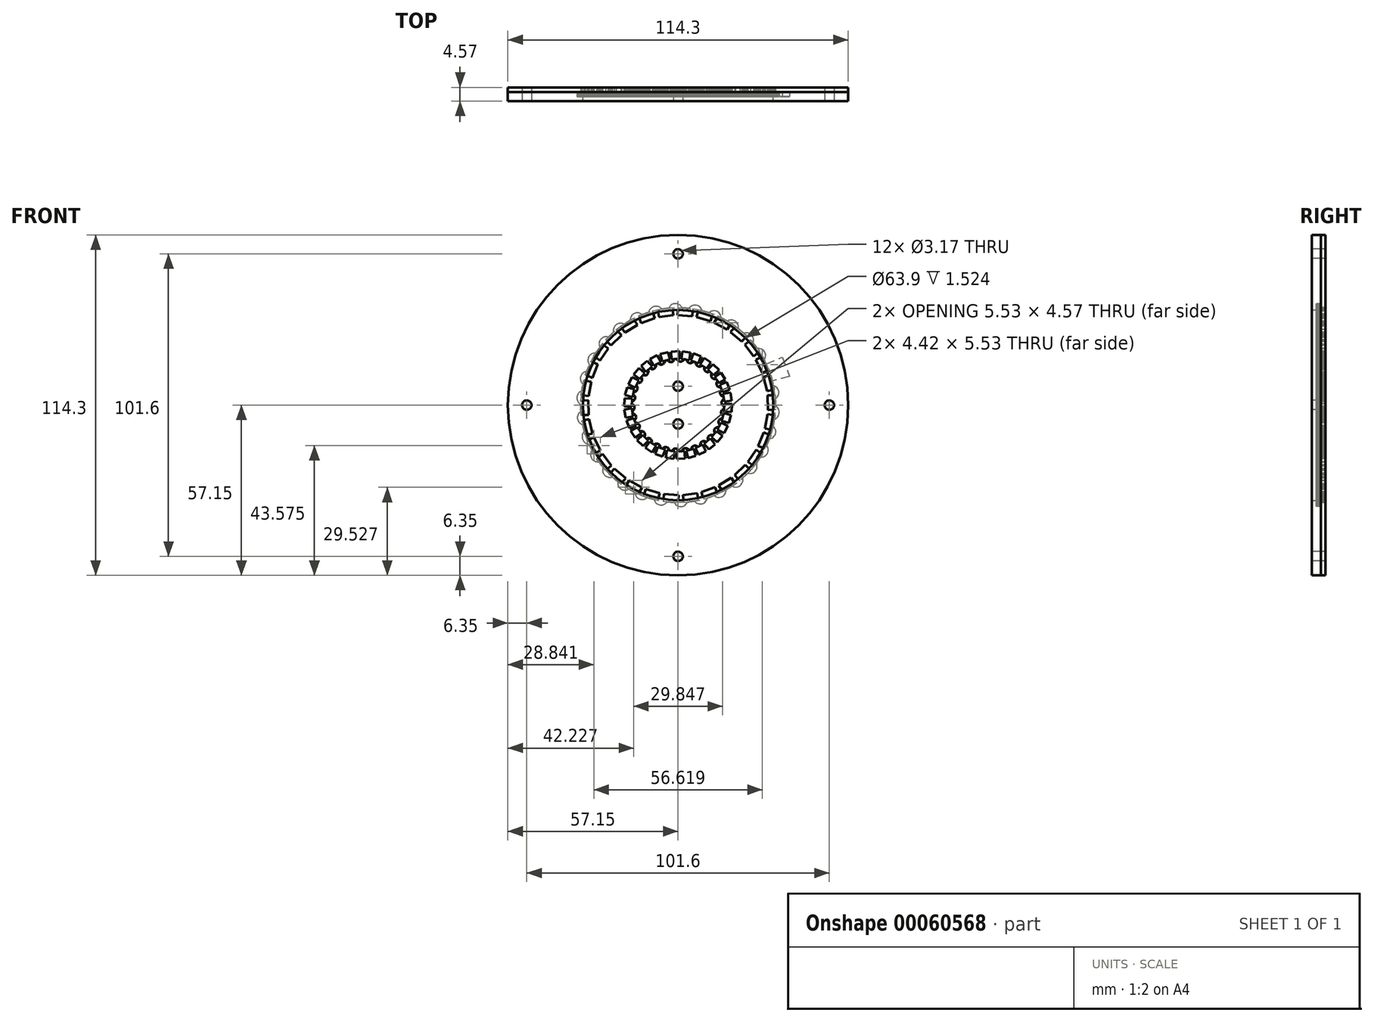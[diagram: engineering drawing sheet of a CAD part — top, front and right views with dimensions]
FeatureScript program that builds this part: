
annotation { "Feature Type Name" : "Feature", "Feature Type Description" : "" }
export const myFeature = defineFeature(function(context is Context, id is Id, definition is map)
    precondition{}
    {
        {
            var Q0;
            Q0=qCreatedBy(makeId("Front.planeOp"),FACE);
            var sketch = newSketch(context, id + "F0", { "sketchPlane" : qUnion([Q0])});
            skCircle(sketch, "E0", {"center": v(0, 0) * mm, "radius": 57.15 * mm});
            skCircle(sketch, "E1", {"center": v(50.8, 0) * mm, "radius": 1.59 * mm});
            skCircle(sketch, "E2", {"center": v(-50.8, 0) * mm, "radius": 1.59 * mm});
            skCircle(sketch, "E3", {"center": v(0, -50.8) * mm, "radius": 1.59 * mm});
            skCircle(sketch, "E4", {"center": v(0, 50.8) * mm, "radius": 1.59 * mm});
            skCircle(sketch, "E5", {"center": v(0, 6.35) * mm, "radius": 1.59 * mm});
            skCircle(sketch, "E6", {"center": v(0, -6.35) * mm, "radius": 1.59 * mm});
            skLineSegment(sketch, "E7", {"start": v(15.83, -1.28) * mm, "end": v(15.67, -1.27) * mm});
            skLineSegment(sketch, "E8", {"start": v(15.67, -1.27) * mm, "end": v(15.51, -1.27) * mm});
            skLineSegment(sketch, "E9", {"start": v(15.51, -1.27) * mm, "end": v(15.36, -1.3) * mm});
            skLineSegment(sketch, "E10", {"start": v(15.36, -1.3) * mm, "end": v(15.2, -1.35) * mm});
            skLineSegment(sketch, "E11", {"start": v(15.2, -1.35) * mm, "end": v(15.06, -1.41) * mm});
            skLineSegment(sketch, "E12", {"start": v(15.06, -1.41) * mm, "end": v(14.93, -1.5) * mm});
            skLineSegment(sketch, "E13", {"start": v(14.93, -1.5) * mm, "end": v(14.8, -1.6) * mm});
            skLineSegment(sketch, "E14", {"start": v(14.8, -1.6) * mm, "end": v(14.7, -1.71) * mm});
            skLineSegment(sketch, "E15", {"start": v(14.7, -1.71) * mm, "end": v(14.6, -1.85) * mm});
            skLineSegment(sketch, "E16", {"start": v(14.6, -1.85) * mm, "end": v(14.53, -1.99) * mm});
            skLineSegment(sketch, "E17", {"start": v(14.53, -1.99) * mm, "end": v(14.48, -2.13) * mm});
            skLineSegment(sketch, "E18", {"start": v(14.48, -2.13) * mm, "end": v(14.44, -2.29) * mm});
            skLineSegment(sketch, "E19", {"start": v(14.44, -2.29) * mm, "end": v(14.43, -2.44) * mm});
            skLineSegment(sketch, "E20", {"start": v(14.43, -2.44) * mm, "end": v(14.44, -2.6) * mm});
            skLineSegment(sketch, "E21", {"start": v(14.44, -2.6) * mm, "end": v(14.46, -2.76) * mm});
            skLineSegment(sketch, "E22", {"start": v(14.46, -2.76) * mm, "end": v(14.5, -2.91) * mm});
            skLineSegment(sketch, "E23", {"start": v(14.5, -2.91) * mm, "end": v(14.58, -3.06) * mm});
            skLineSegment(sketch, "E24", {"start": v(14.58, -3.06) * mm, "end": v(14.66, -3.2) * mm});
            skLineSegment(sketch, "E25", {"start": v(14.66, -3.2) * mm, "end": v(14.76, -3.31) * mm});
            skLineSegment(sketch, "E26", {"start": v(14.76, -3.31) * mm, "end": v(14.88, -3.42) * mm});
            skLineSegment(sketch, "E27", {"start": v(14.88, -3.42) * mm, "end": v(15, -3.5) * mm});
            skLineSegment(sketch, "E28", {"start": v(15, -3.5) * mm, "end": v(15.15, -3.58) * mm});
            skLineSegment(sketch, "E29", {"start": v(15.15, -3.58) * mm, "end": v(15.3, -3.64) * mm});
            skLineSegment(sketch, "E30", {"start": v(15.3, -3.64) * mm, "end": v(15.45, -3.67) * mm});
            skLineSegment(sketch, "E31", {"start": v(31.7, 1.8) * mm, "end": v(32.19, 1.91) * mm});
            skLineSegment(sketch, "E32", {"start": v(32.19, 1.91) * mm, "end": v(32.62, 2.11) * mm});
            skLineSegment(sketch, "E33", {"start": v(32.62, 2.11) * mm, "end": v(33, 2.39) * mm});
            skLineSegment(sketch, "E34", {"start": v(33, 2.39) * mm, "end": v(33.31, 2.73) * mm});
            skLineSegment(sketch, "E35", {"start": v(33.31, 2.73) * mm, "end": v(33.56, 3.12) * mm});
            skLineSegment(sketch, "E36", {"start": v(33.56, 3.12) * mm, "end": v(33.73, 3.56) * mm});
            skLineSegment(sketch, "E37", {"start": v(33.73, 3.56) * mm, "end": v(33.8, 4.03) * mm});
            skLineSegment(sketch, "E38", {"start": v(33.8, 4.03) * mm, "end": v(33.8, 4.52) * mm});
            skLineSegment(sketch, "E39", {"start": v(33.8, 4.52) * mm, "end": v(33.68, 5) * mm});
            skLineSegment(sketch, "E40", {"start": v(33.68, 5) * mm, "end": v(33.48, 5.43) * mm});
            skLineSegment(sketch, "E41", {"start": v(33.48, 5.43) * mm, "end": v(33.2, 5.8) * mm});
            skLineSegment(sketch, "E42", {"start": v(33.2, 5.8) * mm, "end": v(32.86, 6.12) * mm});
            skLineSegment(sketch, "E43", {"start": v(32.86, 6.12) * mm, "end": v(32.47, 6.37) * mm});
            skLineSegment(sketch, "E44", {"start": v(32.47, 6.37) * mm, "end": v(32.03, 6.54) * mm});
            skLineSegment(sketch, "E45", {"start": v(32.03, 6.54) * mm, "end": v(31.56, 6.62) * mm});
            skLineSegment(sketch, "E46", {"start": v(31.56, 6.62) * mm, "end": v(31.07, 6.6) * mm});
            skLineSegment(sketch, "E47", {"start": v(15.22, -4.54) * mm, "end": v(15.06, -4.5) * mm});
            skLineSegment(sketch, "E48", {"start": v(15.06, -4.5) * mm, "end": v(14.9, -4.47) * mm});
            skLineSegment(sketch, "E49", {"start": v(14.9, -4.47) * mm, "end": v(14.75, -4.46) * mm});
            skLineSegment(sketch, "E50", {"start": v(14.75, -4.46) * mm, "end": v(14.6, -4.48) * mm});
            skLineSegment(sketch, "E51", {"start": v(14.6, -4.48) * mm, "end": v(14.44, -4.51) * mm});
            skLineSegment(sketch, "E52", {"start": v(14.44, -4.51) * mm, "end": v(14.3, -4.57) * mm});
            skLineSegment(sketch, "E53", {"start": v(14.3, -4.57) * mm, "end": v(14.15, -4.64) * mm});
            skLineSegment(sketch, "E54", {"start": v(14.15, -4.64) * mm, "end": v(14.02, -4.73) * mm});
            skLineSegment(sketch, "E55", {"start": v(14.02, -4.73) * mm, "end": v(13.9, -4.84) * mm});
            skLineSegment(sketch, "E56", {"start": v(13.9, -4.84) * mm, "end": v(13.8, -4.96) * mm});
            skLineSegment(sketch, "E57", {"start": v(13.8, -4.96) * mm, "end": v(13.72, -5.1) * mm});
            skLineSegment(sketch, "E58", {"start": v(13.72, -5.1) * mm, "end": v(13.65, -5.24) * mm});
            skLineSegment(sketch, "E59", {"start": v(13.65, -5.24) * mm, "end": v(13.6, -5.39) * mm});
            skLineSegment(sketch, "E60", {"start": v(13.6, -5.39) * mm, "end": v(13.58, -5.54) * mm});
            skLineSegment(sketch, "E61", {"start": v(13.58, -5.54) * mm, "end": v(13.57, -5.7) * mm});
            skLineSegment(sketch, "E62", {"start": v(13.57, -5.7) * mm, "end": v(13.59, -5.86) * mm});
            skLineSegment(sketch, "E63", {"start": v(13.59, -5.86) * mm, "end": v(13.62, -6.02) * mm});
            skLineSegment(sketch, "E64", {"start": v(13.62, -6.02) * mm, "end": v(13.68, -6.17) * mm});
            skLineSegment(sketch, "E65", {"start": v(13.68, -6.17) * mm, "end": v(13.75, -6.3) * mm});
            skLineSegment(sketch, "E66", {"start": v(13.75, -6.3) * mm, "end": v(13.84, -6.44) * mm});
            skLineSegment(sketch, "E67", {"start": v(13.84, -6.44) * mm, "end": v(13.95, -6.55) * mm});
            skLineSegment(sketch, "E68", {"start": v(13.95, -6.55) * mm, "end": v(14.07, -6.65) * mm});
            skLineSegment(sketch, "E69", {"start": v(14.07, -6.65) * mm, "end": v(14.2, -6.74) * mm});
            skLineSegment(sketch, "E70", {"start": v(14.2, -6.74) * mm, "end": v(14.35, -6.8) * mm});
            skLineSegment(sketch, "E71", {"start": v(31.4, -4.83) * mm, "end": v(31.88, -4.82) * mm});
            skLineSegment(sketch, "E72", {"start": v(31.88, -4.82) * mm, "end": v(32.35, -4.72) * mm});
            skLineSegment(sketch, "E73", {"start": v(32.35, -4.72) * mm, "end": v(32.77, -4.53) * mm});
            skLineSegment(sketch, "E74", {"start": v(32.77, -4.53) * mm, "end": v(33.15, -4.26) * mm});
            skLineSegment(sketch, "E75", {"start": v(33.15, -4.26) * mm, "end": v(33.48, -3.92) * mm});
            skLineSegment(sketch, "E76", {"start": v(33.48, -3.92) * mm, "end": v(33.73, -3.53) * mm});
            skLineSegment(sketch, "E77", {"start": v(33.73, -3.53) * mm, "end": v(33.9, -3.09) * mm});
            skLineSegment(sketch, "E78", {"start": v(33.9, -3.09) * mm, "end": v(34, -2.6) * mm});
            skLineSegment(sketch, "E79", {"start": v(34, -2.6) * mm, "end": v(33.98, -2.11) * mm});
            skLineSegment(sketch, "E80", {"start": v(33.98, -2.11) * mm, "end": v(33.87, -1.65) * mm});
            skLineSegment(sketch, "E81", {"start": v(33.87, -1.65) * mm, "end": v(33.68, -1.22) * mm});
            skLineSegment(sketch, "E82", {"start": v(33.68, -1.22) * mm, "end": v(33.41, -0.84) * mm});
            skLineSegment(sketch, "E83", {"start": v(33.41, -0.84) * mm, "end": v(33.08, -0.52) * mm});
            skLineSegment(sketch, "E84", {"start": v(33.08, -0.52) * mm, "end": v(32.69, -0.27) * mm});
            skLineSegment(sketch, "E85", {"start": v(32.69, -0.27) * mm, "end": v(32.24, -0.09) * mm});
            skLineSegment(sketch, "E86", {"start": v(32.24, -0.09) * mm, "end": v(31.76, 0) * mm});
            skLineSegment(sketch, "E87", {"start": v(13.94, -7.6) * mm, "end": v(13.8, -7.53) * mm});
            skLineSegment(sketch, "E88", {"start": v(13.8, -7.53) * mm, "end": v(13.65, -7.47) * mm});
            skLineSegment(sketch, "E89", {"start": v(13.65, -7.47) * mm, "end": v(13.5, -7.43) * mm});
            skLineSegment(sketch, "E90", {"start": v(13.5, -7.43) * mm, "end": v(13.34, -7.41) * mm});
            skLineSegment(sketch, "E91", {"start": v(13.34, -7.41) * mm, "end": v(13.19, -7.42) * mm});
            skLineSegment(sketch, "E92", {"start": v(13.19, -7.42) * mm, "end": v(13.03, -7.44) * mm});
            skLineSegment(sketch, "E93", {"start": v(13.03, -7.44) * mm, "end": v(12.88, -7.48) * mm});
            skLineSegment(sketch, "E94", {"start": v(12.88, -7.48) * mm, "end": v(12.73, -7.54) * mm});
            skLineSegment(sketch, "E95", {"start": v(12.73, -7.54) * mm, "end": v(12.6, -7.63) * mm});
            skLineSegment(sketch, "E96", {"start": v(12.6, -7.63) * mm, "end": v(12.47, -7.73) * mm});
            skLineSegment(sketch, "E97", {"start": v(12.47, -7.73) * mm, "end": v(12.36, -7.84) * mm});
            skLineSegment(sketch, "E98", {"start": v(12.36, -7.84) * mm, "end": v(12.26, -7.96) * mm});
            skLineSegment(sketch, "E99", {"start": v(12.26, -7.96) * mm, "end": v(12.19, -8.1) * mm});
            skLineSegment(sketch, "E100", {"start": v(12.19, -8.1) * mm, "end": v(12.13, -8.25) * mm});
            skLineSegment(sketch, "E101", {"start": v(12.13, -8.25) * mm, "end": v(12.1, -8.4) * mm});
            skLineSegment(sketch, "E102", {"start": v(12.1, -8.4) * mm, "end": v(12.07, -8.56) * mm});
            skLineSegment(sketch, "E103", {"start": v(12.07, -8.56) * mm, "end": v(12.07, -8.72) * mm});
            skLineSegment(sketch, "E104", {"start": v(12.07, -8.72) * mm, "end": v(12.1, -8.88) * mm});
            skLineSegment(sketch, "E105", {"start": v(12.1, -8.88) * mm, "end": v(12.14, -9.03) * mm});
            skLineSegment(sketch, "E106", {"start": v(12.14, -9.03) * mm, "end": v(12.2, -9.17) * mm});
            skLineSegment(sketch, "E107", {"start": v(12.2, -9.17) * mm, "end": v(12.28, -9.3) * mm});
            skLineSegment(sketch, "E108", {"start": v(12.28, -9.3) * mm, "end": v(12.38, -9.43) * mm});
            skLineSegment(sketch, "E109", {"start": v(12.38, -9.43) * mm, "end": v(12.5, -9.54) * mm});
            skLineSegment(sketch, "E110", {"start": v(12.5, -9.54) * mm, "end": v(12.62, -9.64) * mm});
            skLineSegment(sketch, "E111", {"start": v(29.7, -11.25) * mm, "end": v(30.18, -11.35) * mm});
            skLineSegment(sketch, "E112", {"start": v(30.18, -11.35) * mm, "end": v(30.66, -11.34) * mm});
            skLineSegment(sketch, "E113", {"start": v(30.66, -11.34) * mm, "end": v(31.12, -11.24) * mm});
            skLineSegment(sketch, "E114", {"start": v(31.12, -11.24) * mm, "end": v(31.54, -11.06) * mm});
            skLineSegment(sketch, "E115", {"start": v(31.54, -11.06) * mm, "end": v(31.93, -10.8) * mm});
            skLineSegment(sketch, "E116", {"start": v(31.93, -10.8) * mm, "end": v(32.26, -10.46) * mm});
            skLineSegment(sketch, "E117", {"start": v(32.26, -10.46) * mm, "end": v(32.52, -10.07) * mm});
            skLineSegment(sketch, "E118", {"start": v(32.52, -10.07) * mm, "end": v(32.7, -9.61) * mm});
            skLineSegment(sketch, "E119", {"start": v(32.7, -9.61) * mm, "end": v(32.8, -9.13) * mm});
            skLineSegment(sketch, "E120", {"start": v(32.8, -9.13) * mm, "end": v(32.8, -8.66) * mm});
            skLineSegment(sketch, "E121", {"start": v(32.8, -8.66) * mm, "end": v(32.7, -8.2) * mm});
            skLineSegment(sketch, "E122", {"start": v(32.7, -8.2) * mm, "end": v(32.5, -7.77) * mm});
            skLineSegment(sketch, "E123", {"start": v(32.5, -7.77) * mm, "end": v(32.25, -7.39) * mm});
            skLineSegment(sketch, "E124", {"start": v(32.25, -7.39) * mm, "end": v(31.92, -7.05) * mm});
            skLineSegment(sketch, "E125", {"start": v(31.92, -7.05) * mm, "end": v(31.52, -6.8) * mm});
            skLineSegment(sketch, "E126", {"start": v(31.52, -6.8) * mm, "end": v(31.07, -6.6) * mm});
            skLineSegment(sketch, "E127", {"start": v(12.05, -10.34) * mm, "end": v(11.93, -10.23) * mm});
            skLineSegment(sketch, "E128", {"start": v(11.93, -10.23) * mm, "end": v(11.8, -10.15) * mm});
            skLineSegment(sketch, "E129", {"start": v(11.8, -10.15) * mm, "end": v(11.66, -10.08) * mm});
            skLineSegment(sketch, "E130", {"start": v(11.66, -10.08) * mm, "end": v(11.51, -10.03) * mm});
            skLineSegment(sketch, "E131", {"start": v(11.51, -10.03) * mm, "end": v(11.36, -10) * mm});
            skLineSegment(sketch, "E132", {"start": v(11.36, -10) * mm, "end": v(11.2, -9.98) * mm});
            skLineSegment(sketch, "E133", {"start": v(11.2, -9.98) * mm, "end": v(11.04, -10) * mm});
            skLineSegment(sketch, "E134", {"start": v(11.04, -10) * mm, "end": v(10.88, -10.03) * mm});
            skLineSegment(sketch, "E135", {"start": v(10.88, -10.03) * mm, "end": v(10.73, -10.08) * mm});
            skLineSegment(sketch, "E136", {"start": v(10.73, -10.08) * mm, "end": v(10.59, -10.15) * mm});
            skLineSegment(sketch, "E137", {"start": v(10.59, -10.15) * mm, "end": v(10.46, -10.24) * mm});
            skLineSegment(sketch, "E138", {"start": v(10.46, -10.24) * mm, "end": v(10.34, -10.34) * mm});
            skLineSegment(sketch, "E139", {"start": v(10.34, -10.34) * mm, "end": v(10.24, -10.46) * mm});
            skLineSegment(sketch, "E140", {"start": v(10.24, -10.46) * mm, "end": v(10.15, -10.59) * mm});
            skLineSegment(sketch, "E141", {"start": v(10.15, -10.59) * mm, "end": v(10.08, -10.73) * mm});
            skLineSegment(sketch, "E142", {"start": v(10.08, -10.73) * mm, "end": v(10.03, -10.88) * mm});
            skLineSegment(sketch, "E143", {"start": v(10.03, -10.88) * mm, "end": v(10, -11.04) * mm});
            skLineSegment(sketch, "E144", {"start": v(10, -11.04) * mm, "end": v(9.99, -11.2) * mm});
            skLineSegment(sketch, "E145", {"start": v(9.99, -11.2) * mm, "end": v(10, -11.36) * mm});
            skLineSegment(sketch, "E146", {"start": v(10, -11.36) * mm, "end": v(10.03, -11.5) * mm});
            skLineSegment(sketch, "E147", {"start": v(10.03, -11.5) * mm, "end": v(10.08, -11.66) * mm});
            skLineSegment(sketch, "E148", {"start": v(10.08, -11.66) * mm, "end": v(10.15, -11.8) * mm});
            skLineSegment(sketch, "E149", {"start": v(10.15, -11.8) * mm, "end": v(10.24, -11.93) * mm});
            skLineSegment(sketch, "E150", {"start": v(10.24, -11.93) * mm, "end": v(10.34, -12.05) * mm});
            skLineSegment(sketch, "E151", {"start": v(26.71, -17.18) * mm, "end": v(27.16, -17.37) * mm});
            skLineSegment(sketch, "E152", {"start": v(27.16, -17.37) * mm, "end": v(27.63, -17.46) * mm});
            skLineSegment(sketch, "E153", {"start": v(27.63, -17.46) * mm, "end": v(28.1, -17.46) * mm});
            skLineSegment(sketch, "E154", {"start": v(28.1, -17.46) * mm, "end": v(28.56, -17.37) * mm});
            skLineSegment(sketch, "E155", {"start": v(28.56, -17.37) * mm, "end": v(28.99, -17.2) * mm});
            skLineSegment(sketch, "E156", {"start": v(28.99, -17.2) * mm, "end": v(29.38, -16.94) * mm});
            skLineSegment(sketch, "E157", {"start": v(29.38, -16.94) * mm, "end": v(29.72, -16.6) * mm});
            skLineSegment(sketch, "E158", {"start": v(29.72, -16.6) * mm, "end": v(30, -16.2) * mm});
            skLineSegment(sketch, "E159", {"start": v(30, -16.2) * mm, "end": v(30.18, -15.75) * mm});
            skLineSegment(sketch, "E160", {"start": v(30.18, -15.75) * mm, "end": v(30.27, -15.28) * mm});
            skLineSegment(sketch, "E161", {"start": v(30.27, -15.28) * mm, "end": v(30.27, -14.82) * mm});
            skLineSegment(sketch, "E162", {"start": v(30.27, -14.82) * mm, "end": v(30.18, -14.36) * mm});
            skLineSegment(sketch, "E163", {"start": v(30.18, -14.36) * mm, "end": v(30, -13.93) * mm});
            skLineSegment(sketch, "E164", {"start": v(30, -13.93) * mm, "end": v(29.75, -13.54) * mm});
            skLineSegment(sketch, "E165", {"start": v(29.75, -13.54) * mm, "end": v(29.42, -13.2) * mm});
            skLineSegment(sketch, "E166", {"start": v(29.42, -13.2) * mm, "end": v(29.01, -12.92) * mm});
            skLineSegment(sketch, "E167", {"start": v(9.64, -12.62) * mm, "end": v(9.54, -12.5) * mm});
            skLineSegment(sketch, "E168", {"start": v(9.54, -12.5) * mm, "end": v(9.43, -12.38) * mm});
            skLineSegment(sketch, "E169", {"start": v(9.43, -12.38) * mm, "end": v(9.31, -12.28) * mm});
            skLineSegment(sketch, "E170", {"start": v(9.31, -12.28) * mm, "end": v(9.18, -12.2) * mm});
            skLineSegment(sketch, "E171", {"start": v(9.18, -12.2) * mm, "end": v(9.03, -12.14) * mm});
            skLineSegment(sketch, "E172", {"start": v(9.03, -12.14) * mm, "end": v(8.88, -12.1) * mm});
            skLineSegment(sketch, "E173", {"start": v(8.88, -12.1) * mm, "end": v(8.72, -12.07) * mm});
            skLineSegment(sketch, "E174", {"start": v(8.72, -12.07) * mm, "end": v(8.56, -12.07) * mm});
            skLineSegment(sketch, "E175", {"start": v(8.56, -12.07) * mm, "end": v(8.4, -12.09) * mm});
            skLineSegment(sketch, "E176", {"start": v(8.4, -12.09) * mm, "end": v(8.25, -12.13) * mm});
            skLineSegment(sketch, "E177", {"start": v(8.25, -12.13) * mm, "end": v(8.1, -12.19) * mm});
            skLineSegment(sketch, "E178", {"start": v(8.1, -12.19) * mm, "end": v(7.97, -12.26) * mm});
            skLineSegment(sketch, "E179", {"start": v(7.97, -12.26) * mm, "end": v(7.84, -12.36) * mm});
            skLineSegment(sketch, "E180", {"start": v(7.84, -12.36) * mm, "end": v(7.73, -12.47) * mm});
            skLineSegment(sketch, "E181", {"start": v(7.73, -12.47) * mm, "end": v(7.63, -12.6) * mm});
            skLineSegment(sketch, "E182", {"start": v(7.63, -12.6) * mm, "end": v(7.55, -12.73) * mm});
            skLineSegment(sketch, "E183", {"start": v(7.55, -12.73) * mm, "end": v(7.48, -12.88) * mm});
            skLineSegment(sketch, "E184", {"start": v(7.48, -12.88) * mm, "end": v(7.44, -13.03) * mm});
            skLineSegment(sketch, "E185", {"start": v(7.44, -13.03) * mm, "end": v(7.42, -13.19) * mm});
            skLineSegment(sketch, "E186", {"start": v(7.42, -13.19) * mm, "end": v(7.42, -13.34) * mm});
            skLineSegment(sketch, "E187", {"start": v(7.42, -13.34) * mm, "end": v(7.43, -13.5) * mm});
            skLineSegment(sketch, "E188", {"start": v(7.43, -13.5) * mm, "end": v(7.47, -13.65) * mm});
            skLineSegment(sketch, "E189", {"start": v(7.47, -13.65) * mm, "end": v(7.53, -13.8) * mm});
            skLineSegment(sketch, "E190", {"start": v(7.53, -13.8) * mm, "end": v(7.6, -13.94) * mm});
            skLineSegment(sketch, "E191", {"start": v(22.55, -22.36) * mm, "end": v(22.96, -22.64) * mm});
            skLineSegment(sketch, "E192", {"start": v(22.96, -22.64) * mm, "end": v(23.4, -22.83) * mm});
            skLineSegment(sketch, "E193", {"start": v(23.4, -22.83) * mm, "end": v(23.85, -22.92) * mm});
            skLineSegment(sketch, "E194", {"start": v(23.85, -22.92) * mm, "end": v(24.32, -22.93) * mm});
            skLineSegment(sketch, "E195", {"start": v(24.32, -22.93) * mm, "end": v(24.78, -22.85) * mm});
            skLineSegment(sketch, "E196", {"start": v(24.78, -22.85) * mm, "end": v(25.21, -22.68) * mm});
            skLineSegment(sketch, "E197", {"start": v(25.21, -22.68) * mm, "end": v(25.62, -22.43) * mm});
            skLineSegment(sketch, "E198", {"start": v(25.62, -22.43) * mm, "end": v(25.97, -22.09) * mm});
            skLineSegment(sketch, "E199", {"start": v(25.97, -22.09) * mm, "end": v(26.25, -21.68) * mm});
            skLineSegment(sketch, "E200", {"start": v(26.25, -21.68) * mm, "end": v(26.44, -21.24) * mm});
            skLineSegment(sketch, "E201", {"start": v(26.44, -21.24) * mm, "end": v(26.53, -20.79) * mm});
            skLineSegment(sketch, "E202", {"start": v(26.53, -20.79) * mm, "end": v(26.54, -20.32) * mm});
            skLineSegment(sketch, "E203", {"start": v(26.54, -20.32) * mm, "end": v(26.46, -19.86) * mm});
            skLineSegment(sketch, "E204", {"start": v(26.46, -19.86) * mm, "end": v(26.29, -19.43) * mm});
            skLineSegment(sketch, "E205", {"start": v(26.29, -19.43) * mm, "end": v(26.03, -19.02) * mm});
            skLineSegment(sketch, "E206", {"start": v(26.03, -19.02) * mm, "end": v(25.7, -18.67) * mm});
            skLineSegment(sketch, "E207", {"start": v(6.8, -14.35) * mm, "end": v(6.74, -14.2) * mm});
            skLineSegment(sketch, "E208", {"start": v(6.74, -14.2) * mm, "end": v(6.65, -14.07) * mm});
            skLineSegment(sketch, "E209", {"start": v(6.65, -14.07) * mm, "end": v(6.55, -13.95) * mm});
            skLineSegment(sketch, "E210", {"start": v(6.55, -13.95) * mm, "end": v(6.44, -13.84) * mm});
            skLineSegment(sketch, "E211", {"start": v(6.44, -13.84) * mm, "end": v(6.31, -13.75) * mm});
            skLineSegment(sketch, "E212", {"start": v(6.31, -13.75) * mm, "end": v(6.17, -13.68) * mm});
            skLineSegment(sketch, "E213", {"start": v(6.17, -13.68) * mm, "end": v(6.02, -13.62) * mm});
            skLineSegment(sketch, "E214", {"start": v(6.02, -13.62) * mm, "end": v(5.87, -13.59) * mm});
            skLineSegment(sketch, "E215", {"start": v(5.87, -13.59) * mm, "end": v(5.7, -13.57) * mm});
            skLineSegment(sketch, "E216", {"start": v(5.7, -13.57) * mm, "end": v(5.55, -13.58) * mm});
            skLineSegment(sketch, "E217", {"start": v(5.55, -13.58) * mm, "end": v(5.4, -13.6) * mm});
            skLineSegment(sketch, "E218", {"start": v(5.4, -13.6) * mm, "end": v(5.24, -13.65) * mm});
            skLineSegment(sketch, "E219", {"start": v(5.24, -13.65) * mm, "end": v(5.1, -13.72) * mm});
            skLineSegment(sketch, "E220", {"start": v(5.1, -13.72) * mm, "end": v(4.97, -13.8) * mm});
            skLineSegment(sketch, "E221", {"start": v(4.97, -13.8) * mm, "end": v(4.84, -13.9) * mm});
            skLineSegment(sketch, "E222", {"start": v(4.84, -13.9) * mm, "end": v(4.73, -14.02) * mm});
            skLineSegment(sketch, "E223", {"start": v(4.73, -14.02) * mm, "end": v(4.64, -14.15) * mm});
            skLineSegment(sketch, "E224", {"start": v(4.64, -14.15) * mm, "end": v(4.57, -14.3) * mm});
            skLineSegment(sketch, "E225", {"start": v(4.57, -14.3) * mm, "end": v(4.51, -14.44) * mm});
            skLineSegment(sketch, "E226", {"start": v(4.51, -14.44) * mm, "end": v(4.48, -14.6) * mm});
            skLineSegment(sketch, "E227", {"start": v(4.48, -14.6) * mm, "end": v(4.47, -14.75) * mm});
            skLineSegment(sketch, "E228", {"start": v(4.47, -14.75) * mm, "end": v(4.47, -14.9) * mm});
            skLineSegment(sketch, "E229", {"start": v(4.47, -14.9) * mm, "end": v(4.5, -15.06) * mm});
            skLineSegment(sketch, "E230", {"start": v(4.5, -15.06) * mm, "end": v(4.55, -15.22) * mm});
            skLineSegment(sketch, "E231", {"start": v(17.41, -26.56) * mm, "end": v(17.75, -26.92) * mm});
            skLineSegment(sketch, "E232", {"start": v(17.75, -26.92) * mm, "end": v(18.14, -27.2) * mm});
            skLineSegment(sketch, "E233", {"start": v(18.14, -27.2) * mm, "end": v(18.57, -27.38) * mm});
            skLineSegment(sketch, "E234", {"start": v(18.57, -27.38) * mm, "end": v(19.02, -27.49) * mm});
            skLineSegment(sketch, "E235", {"start": v(19.02, -27.49) * mm, "end": v(19.49, -27.5) * mm});
            skLineSegment(sketch, "E236", {"start": v(19.49, -27.5) * mm, "end": v(19.95, -27.43) * mm});
            skLineSegment(sketch, "E237", {"start": v(19.95, -27.43) * mm, "end": v(20.4, -27.26) * mm});
            skLineSegment(sketch, "E238", {"start": v(20.4, -27.26) * mm, "end": v(20.81, -27) * mm});
            skLineSegment(sketch, "E239", {"start": v(20.81, -27) * mm, "end": v(21.17, -26.66) * mm});
            skLineSegment(sketch, "E240", {"start": v(21.17, -26.66) * mm, "end": v(21.44, -26.28) * mm});
            skLineSegment(sketch, "E241", {"start": v(21.44, -26.28) * mm, "end": v(21.63, -25.85) * mm});
            skLineSegment(sketch, "E242", {"start": v(21.63, -25.85) * mm, "end": v(21.73, -25.4) * mm});
            skLineSegment(sketch, "E243", {"start": v(21.73, -25.4) * mm, "end": v(21.75, -24.93) * mm});
            skLineSegment(sketch, "E244", {"start": v(21.75, -24.93) * mm, "end": v(21.68, -24.47) * mm});
            skLineSegment(sketch, "E245", {"start": v(21.68, -24.47) * mm, "end": v(21.5, -24.02) * mm});
            skLineSegment(sketch, "E246", {"start": v(21.5, -24.02) * mm, "end": v(21.25, -23.6) * mm});
            skLineSegment(sketch, "E247", {"start": v(3.68, -15.45) * mm, "end": v(3.64, -15.3) * mm});
            skLineSegment(sketch, "E248", {"start": v(3.64, -15.3) * mm, "end": v(3.58, -15.14) * mm});
            skLineSegment(sketch, "E249", {"start": v(3.58, -15.14) * mm, "end": v(3.51, -15) * mm});
            skLineSegment(sketch, "E250", {"start": v(3.51, -15) * mm, "end": v(3.42, -14.88) * mm});
            skLineSegment(sketch, "E251", {"start": v(3.42, -14.88) * mm, "end": v(3.31, -14.76) * mm});
            skLineSegment(sketch, "E252", {"start": v(3.31, -14.76) * mm, "end": v(3.2, -14.66) * mm});
            skLineSegment(sketch, "E253", {"start": v(3.2, -14.66) * mm, "end": v(3.06, -14.58) * mm});
            skLineSegment(sketch, "E254", {"start": v(3.06, -14.58) * mm, "end": v(2.91, -14.5) * mm});
            skLineSegment(sketch, "E255", {"start": v(2.91, -14.5) * mm, "end": v(2.76, -14.46) * mm});
            skLineSegment(sketch, "E256", {"start": v(2.76, -14.46) * mm, "end": v(2.6, -14.43) * mm});
            skLineSegment(sketch, "E257", {"start": v(2.6, -14.43) * mm, "end": v(2.45, -14.43) * mm});
            skLineSegment(sketch, "E258", {"start": v(2.45, -14.43) * mm, "end": v(2.29, -14.44) * mm});
            skLineSegment(sketch, "E259", {"start": v(2.29, -14.44) * mm, "end": v(2.14, -14.48) * mm});
            skLineSegment(sketch, "E260", {"start": v(2.14, -14.48) * mm, "end": v(1.99, -14.53) * mm});
            skLineSegment(sketch, "E261", {"start": v(1.99, -14.53) * mm, "end": v(1.85, -14.6) * mm});
            skLineSegment(sketch, "E262", {"start": v(1.85, -14.6) * mm, "end": v(1.72, -14.7) * mm});
            skLineSegment(sketch, "E263", {"start": v(1.72, -14.7) * mm, "end": v(1.6, -14.8) * mm});
            skLineSegment(sketch, "E264", {"start": v(1.6, -14.8) * mm, "end": v(1.5, -14.93) * mm});
            skLineSegment(sketch, "E265", {"start": v(1.5, -14.93) * mm, "end": v(1.41, -15.06) * mm});
            skLineSegment(sketch, "E266", {"start": v(1.41, -15.06) * mm, "end": v(1.35, -15.2) * mm});
            skLineSegment(sketch, "E267", {"start": v(1.35, -15.2) * mm, "end": v(1.3, -15.35) * mm});
            skLineSegment(sketch, "E268", {"start": v(1.3, -15.35) * mm, "end": v(1.27, -15.5) * mm});
            skLineSegment(sketch, "E269", {"start": v(1.27, -15.5) * mm, "end": v(1.27, -15.67) * mm});
            skLineSegment(sketch, "E270", {"start": v(1.27, -15.67) * mm, "end": v(1.28, -15.83) * mm});
            skLineSegment(sketch, "E271", {"start": v(11.5, -29.6) * mm, "end": v(11.77, -30.02) * mm});
            skLineSegment(sketch, "E272", {"start": v(11.77, -30.02) * mm, "end": v(12.09, -30.37) * mm});
            skLineSegment(sketch, "E273", {"start": v(12.09, -30.37) * mm, "end": v(12.47, -30.64) * mm});
            skLineSegment(sketch, "E274", {"start": v(12.47, -30.64) * mm, "end": v(12.9, -30.84) * mm});
            skLineSegment(sketch, "E275", {"start": v(12.9, -30.84) * mm, "end": v(13.34, -30.95) * mm});
            skLineSegment(sketch, "E276", {"start": v(13.34, -30.95) * mm, "end": v(13.8, -30.97) * mm});
            skLineSegment(sketch, "E277", {"start": v(13.8, -30.97) * mm, "end": v(14.28, -30.9) * mm});
            skLineSegment(sketch, "E278", {"start": v(14.28, -30.9) * mm, "end": v(14.74, -30.74) * mm});
            skLineSegment(sketch, "E279", {"start": v(14.74, -30.74) * mm, "end": v(15.16, -30.48) * mm});
            skLineSegment(sketch, "E280", {"start": v(15.16, -30.48) * mm, "end": v(15.5, -30.16) * mm});
            skLineSegment(sketch, "E281", {"start": v(15.5, -30.16) * mm, "end": v(15.78, -29.78) * mm});
            skLineSegment(sketch, "E282", {"start": v(15.78, -29.78) * mm, "end": v(15.98, -29.36) * mm});
            skLineSegment(sketch, "E283", {"start": v(15.98, -29.36) * mm, "end": v(16.1, -28.9) * mm});
            skLineSegment(sketch, "E284", {"start": v(16.1, -28.9) * mm, "end": v(16.11, -28.44) * mm});
            skLineSegment(sketch, "E285", {"start": v(16.11, -28.44) * mm, "end": v(16.05, -27.97) * mm});
            skLineSegment(sketch, "E286", {"start": v(16.05, -27.97) * mm, "end": v(15.88, -27.5) * mm});
            skLineSegment(sketch, "E287", {"start": v(0.38, -15.88) * mm, "end": v(0.37, -15.63) * mm});
            skLineSegment(sketch, "E288", {"start": v(0.37, -15.63) * mm, "end": v(0.31, -15.4) * mm});
            skLineSegment(sketch, "E289", {"start": v(0.31, -15.4) * mm, "end": v(0.21, -15.19) * mm});
            skLineSegment(sketch, "E290", {"start": v(0.21, -15.19) * mm, "end": v(0.07, -15) * mm});
            skLineSegment(sketch, "E291", {"start": v(0.07, -15) * mm, "end": v(-0.1, -14.84) * mm});
            skLineSegment(sketch, "E292", {"start": v(-0.1, -14.84) * mm, "end": v(-0.3, -14.72) * mm});
            skLineSegment(sketch, "E293", {"start": v(-0.3, -14.72) * mm, "end": v(-0.52, -14.64) * mm});
            skLineSegment(sketch, "E294", {"start": v(-0.52, -14.64) * mm, "end": v(-0.76, -14.6) * mm});
            skLineSegment(sketch, "E295", {"start": v(-0.76, -14.6) * mm, "end": v(-1, -14.61) * mm});
            skLineSegment(sketch, "E296", {"start": v(-1, -14.61) * mm, "end": v(-1.24, -14.67) * mm});
            skLineSegment(sketch, "E297", {"start": v(-1.24, -14.67) * mm, "end": v(-1.45, -14.77) * mm});
            skLineSegment(sketch, "E298", {"start": v(-1.45, -14.77) * mm, "end": v(-1.64, -14.91) * mm});
            skLineSegment(sketch, "E299", {"start": v(-1.64, -14.91) * mm, "end": v(-1.8, -15.08) * mm});
            skLineSegment(sketch, "E300", {"start": v(-1.8, -15.08) * mm, "end": v(-1.92, -15.28) * mm});
            skLineSegment(sketch, "E301", {"start": v(-1.92, -15.28) * mm, "end": v(-2, -15.5) * mm});
            skLineSegment(sketch, "E302", {"start": v(-2, -15.5) * mm, "end": v(-2.04, -15.75) * mm});
            skLineSegment(sketch, "E303", {"start": v(5.1, -31.35) * mm, "end": v(5.27, -31.8) * mm});
            skLineSegment(sketch, "E304", {"start": v(5.27, -31.8) * mm, "end": v(5.51, -32.22) * mm});
            skLineSegment(sketch, "E305", {"start": v(5.51, -32.22) * mm, "end": v(5.83, -32.57) * mm});
            skLineSegment(sketch, "E306", {"start": v(5.83, -32.57) * mm, "end": v(6.2, -32.84) * mm});
            skLineSegment(sketch, "E307", {"start": v(6.2, -32.84) * mm, "end": v(6.62, -33.05) * mm});
            skLineSegment(sketch, "E308", {"start": v(6.62, -33.05) * mm, "end": v(7.07, -33.17) * mm});
            skLineSegment(sketch, "E309", {"start": v(7.07, -33.17) * mm, "end": v(7.54, -33.2) * mm});
            skLineSegment(sketch, "E310", {"start": v(7.54, -33.2) * mm, "end": v(8.03, -33.13) * mm});
            skLineSegment(sketch, "E311", {"start": v(8.03, -33.13) * mm, "end": v(8.5, -32.97) * mm});
            skLineSegment(sketch, "E312", {"start": v(8.5, -32.97) * mm, "end": v(8.9, -32.72) * mm});
            skLineSegment(sketch, "E313", {"start": v(8.9, -32.72) * mm, "end": v(9.25, -32.4) * mm});
            skLineSegment(sketch, "E314", {"start": v(9.25, -32.4) * mm, "end": v(9.53, -32.04) * mm});
            skLineSegment(sketch, "E315", {"start": v(9.53, -32.04) * mm, "end": v(9.73, -31.62) * mm});
            skLineSegment(sketch, "E316", {"start": v(9.73, -31.62) * mm, "end": v(9.85, -31.17) * mm});
            skLineSegment(sketch, "E317", {"start": v(9.85, -31.17) * mm, "end": v(9.88, -30.7) * mm});
            skLineSegment(sketch, "E318", {"start": v(9.88, -30.7) * mm, "end": v(9.81, -30.2) * mm});
            skLineSegment(sketch, "E319", {"start": v(-2.93, -15.6) * mm, "end": v(-2.89, -15.37) * mm});
            skLineSegment(sketch, "E320", {"start": v(-2.89, -15.37) * mm, "end": v(-2.9, -15.13) * mm});
            skLineSegment(sketch, "E321", {"start": v(-2.9, -15.13) * mm, "end": v(-2.95, -14.9) * mm});
            skLineSegment(sketch, "E322", {"start": v(-2.95, -14.9) * mm, "end": v(-3.05, -14.69) * mm});
            skLineSegment(sketch, "E323", {"start": v(-3.05, -14.69) * mm, "end": v(-3.18, -14.5) * mm});
            skLineSegment(sketch, "E324", {"start": v(-3.18, -14.5) * mm, "end": v(-3.35, -14.34) * mm});
            skLineSegment(sketch, "E325", {"start": v(-3.35, -14.34) * mm, "end": v(-3.55, -14.21) * mm});
            skLineSegment(sketch, "E326", {"start": v(-3.55, -14.21) * mm, "end": v(-3.78, -14.12) * mm});
            skLineSegment(sketch, "E327", {"start": v(-3.78, -14.12) * mm, "end": v(-4.02, -14.08) * mm});
            skLineSegment(sketch, "E328", {"start": v(-4.02, -14.08) * mm, "end": v(-4.26, -14.1) * mm});
            skLineSegment(sketch, "E329", {"start": v(-4.26, -14.1) * mm, "end": v(-4.5, -14.15) * mm});
            skLineSegment(sketch, "E330", {"start": v(-4.5, -14.15) * mm, "end": v(-4.7, -14.24) * mm});
            skLineSegment(sketch, "E331", {"start": v(-4.7, -14.24) * mm, "end": v(-4.9, -14.38) * mm});
            skLineSegment(sketch, "E332", {"start": v(-4.9, -14.38) * mm, "end": v(-5.05, -14.55) * mm});
            skLineSegment(sketch, "E333", {"start": v(-5.05, -14.55) * mm, "end": v(-5.18, -14.75) * mm});
            skLineSegment(sketch, "E334", {"start": v(-5.18, -14.75) * mm, "end": v(-5.27, -14.98) * mm});
            skLineSegment(sketch, "E335", {"start": v(-1.52, -31.72) * mm, "end": v(-1.46, -32.2) * mm});
            skLineSegment(sketch, "E336", {"start": v(-1.46, -32.2) * mm, "end": v(-1.3, -32.66) * mm});
            skLineSegment(sketch, "E337", {"start": v(-1.3, -32.66) * mm, "end": v(-1.07, -33.06) * mm});
            skLineSegment(sketch, "E338", {"start": v(-1.07, -33.06) * mm, "end": v(-0.77, -33.41) * mm});
            skLineSegment(sketch, "E339", {"start": v(-0.77, -33.41) * mm, "end": v(-0.4, -33.7) * mm});
            skLineSegment(sketch, "E340", {"start": v(-0.4, -33.7) * mm, "end": v(0.02, -33.91) * mm});
            skLineSegment(sketch, "E341", {"start": v(0.02, -33.91) * mm, "end": v(0.48, -34.04) * mm});
            skLineSegment(sketch, "E342", {"start": v(0.48, -34.04) * mm, "end": v(0.97, -34.08) * mm});
            skLineSegment(sketch, "E343", {"start": v(0.97, -34.08) * mm, "end": v(1.45, -34.01) * mm});
            skLineSegment(sketch, "E344", {"start": v(1.45, -34.01) * mm, "end": v(1.9, -33.86) * mm});
            skLineSegment(sketch, "E345", {"start": v(1.9, -33.86) * mm, "end": v(2.3, -33.62) * mm});
            skLineSegment(sketch, "E346", {"start": v(2.3, -33.62) * mm, "end": v(2.66, -33.32) * mm});
            skLineSegment(sketch, "E347", {"start": v(2.66, -33.32) * mm, "end": v(2.94, -32.95) * mm});
            skLineSegment(sketch, "E348", {"start": v(2.94, -32.95) * mm, "end": v(3.15, -32.53) * mm});
            skLineSegment(sketch, "E349", {"start": v(3.15, -32.53) * mm, "end": v(3.28, -32.07) * mm});
            skLineSegment(sketch, "E350", {"start": v(3.28, -32.07) * mm, "end": v(3.32, -31.59) * mm});
            skLineSegment(sketch, "E351", {"start": v(-6.1, -14.66) * mm, "end": v(-6.02, -14.43) * mm});
            skLineSegment(sketch, "E352", {"start": v(-6.02, -14.43) * mm, "end": v(-5.98, -14.2) * mm});
            skLineSegment(sketch, "E353", {"start": v(-5.98, -14.2) * mm, "end": v(-5.98, -13.96) * mm});
            skLineSegment(sketch, "E354", {"start": v(-5.98, -13.96) * mm, "end": v(-6.03, -13.73) * mm});
            skLineSegment(sketch, "E355", {"start": v(-6.03, -13.73) * mm, "end": v(-6.13, -13.52) * mm});
            skLineSegment(sketch, "E356", {"start": v(-6.13, -13.52) * mm, "end": v(-6.26, -13.33) * mm});
            skLineSegment(sketch, "E357", {"start": v(-6.26, -13.33) * mm, "end": v(-6.43, -13.16) * mm});
            skLineSegment(sketch, "E358", {"start": v(-6.43, -13.16) * mm, "end": v(-6.64, -13.03) * mm});
            skLineSegment(sketch, "E359", {"start": v(-6.64, -13.03) * mm, "end": v(-6.87, -12.94) * mm});
            skLineSegment(sketch, "E360", {"start": v(-6.87, -12.94) * mm, "end": v(-7.1, -12.9) * mm});
            skLineSegment(sketch, "E361", {"start": v(-7.1, -12.9) * mm, "end": v(-7.33, -12.9) * mm});
            skLineSegment(sketch, "E362", {"start": v(-7.33, -12.9) * mm, "end": v(-7.56, -12.96) * mm});
            skLineSegment(sketch, "E363", {"start": v(-7.56, -12.96) * mm, "end": v(-7.77, -13.05) * mm});
            skLineSegment(sketch, "E364", {"start": v(-7.77, -13.05) * mm, "end": v(-7.97, -13.18) * mm});
            skLineSegment(sketch, "E365", {"start": v(-7.97, -13.18) * mm, "end": v(-8.13, -13.35) * mm});
            skLineSegment(sketch, "E366", {"start": v(-8.13, -13.35) * mm, "end": v(-8.27, -13.56) * mm});
            skLineSegment(sketch, "E367", {"start": v(-8.09, -30.71) * mm, "end": v(-8.12, -31.03) * mm});
            skLineSegment(sketch, "E368", {"start": v(-8.12, -31.03) * mm, "end": v(-8.12, -31.35) * mm});
            skLineSegment(sketch, "E369", {"start": v(-8.12, -31.35) * mm, "end": v(-8.07, -31.66) * mm});
            skLineSegment(sketch, "E370", {"start": v(-8.07, -31.66) * mm, "end": v(-7.99, -31.96) * mm});
            skLineSegment(sketch, "E371", {"start": v(-7.99, -31.96) * mm, "end": v(-7.86, -32.25) * mm});
            skLineSegment(sketch, "E372", {"start": v(-7.86, -32.25) * mm, "end": v(-7.7, -32.52) * mm});
            skLineSegment(sketch, "E373", {"start": v(-7.7, -32.52) * mm, "end": v(-7.5, -32.77) * mm});
            skLineSegment(sketch, "E374", {"start": v(-7.5, -32.77) * mm, "end": v(-7.27, -33) * mm});
            skLineSegment(sketch, "E375", {"start": v(-7.27, -33) * mm, "end": v(-7.02, -33.19) * mm});
            skLineSegment(sketch, "E376", {"start": v(-7.02, -33.19) * mm, "end": v(-6.74, -33.34) * mm});
            skLineSegment(sketch, "E377", {"start": v(-6.74, -33.34) * mm, "end": v(-6.44, -33.45) * mm});
            skLineSegment(sketch, "E378", {"start": v(-6.44, -33.45) * mm, "end": v(-6.14, -33.53) * mm});
            skLineSegment(sketch, "E379", {"start": v(-6.14, -33.53) * mm, "end": v(-5.83, -33.57) * mm});
            skLineSegment(sketch, "E380", {"start": v(-5.83, -33.57) * mm, "end": v(-5.51, -33.56) * mm});
            skLineSegment(sketch, "E381", {"start": v(-5.51, -33.56) * mm, "end": v(-5.2, -33.52) * mm});
            skLineSegment(sketch, "E382", {"start": v(-5.2, -33.52) * mm, "end": v(-4.9, -33.43) * mm});
            skLineSegment(sketch, "E383", {"start": v(-4.9, -33.43) * mm, "end": v(-4.6, -33.3) * mm});
            skLineSegment(sketch, "E384", {"start": v(-4.6, -33.3) * mm, "end": v(-4.32, -33.14) * mm});
            skLineSegment(sketch, "E385", {"start": v(-4.32, -33.14) * mm, "end": v(-4.08, -32.94) * mm});
            skLineSegment(sketch, "E386", {"start": v(-4.08, -32.94) * mm, "end": v(-3.86, -32.72) * mm});
            skLineSegment(sketch, "E387", {"start": v(-3.86, -32.72) * mm, "end": v(-3.67, -32.47) * mm});
            skLineSegment(sketch, "E388", {"start": v(-3.67, -32.47) * mm, "end": v(-3.52, -32.2) * mm});
            skLineSegment(sketch, "E389", {"start": v(-3.52, -32.2) * mm, "end": v(-3.4, -31.9) * mm});
            skLineSegment(sketch, "E390", {"start": v(-3.4, -31.9) * mm, "end": v(-3.32, -31.58) * mm});
            skLineSegment(sketch, "E391", {"start": v(-9.02, -13.07) * mm, "end": v(-8.89, -12.86) * mm});
            skLineSegment(sketch, "E392", {"start": v(-8.89, -12.86) * mm, "end": v(-8.8, -12.64) * mm});
            skLineSegment(sketch, "E393", {"start": v(-8.8, -12.64) * mm, "end": v(-8.76, -12.41) * mm});
            skLineSegment(sketch, "E394", {"start": v(-8.76, -12.41) * mm, "end": v(-8.76, -12.18) * mm});
            skLineSegment(sketch, "E395", {"start": v(-8.76, -12.18) * mm, "end": v(-8.8, -11.95) * mm});
            skLineSegment(sketch, "E396", {"start": v(-8.8, -11.95) * mm, "end": v(-8.9, -11.73) * mm});
            skLineSegment(sketch, "E397", {"start": v(-8.9, -11.73) * mm, "end": v(-9.03, -11.54) * mm});
            skLineSegment(sketch, "E398", {"start": v(-9.03, -11.54) * mm, "end": v(-9.2, -11.36) * mm});
            skLineSegment(sketch, "E399", {"start": v(-9.2, -11.36) * mm, "end": v(-9.4, -11.23) * mm});
            skLineSegment(sketch, "E400", {"start": v(-9.4, -11.23) * mm, "end": v(-9.63, -11.14) * mm});
            skLineSegment(sketch, "E401", {"start": v(-9.63, -11.14) * mm, "end": v(-9.86, -11.1) * mm});
            skLineSegment(sketch, "E402", {"start": v(-9.86, -11.1) * mm, "end": v(-10.09, -11.1) * mm});
            skLineSegment(sketch, "E403", {"start": v(-10.09, -11.1) * mm, "end": v(-10.32, -11.15) * mm});
            skLineSegment(sketch, "E404", {"start": v(-10.32, -11.15) * mm, "end": v(-10.53, -11.24) * mm});
            skLineSegment(sketch, "E405", {"start": v(-10.53, -11.24) * mm, "end": v(-10.73, -11.37) * mm});
            skLineSegment(sketch, "E406", {"start": v(-10.73, -11.37) * mm, "end": v(-10.9, -11.54) * mm});
            skLineSegment(sketch, "E407", {"start": v(-14.3, -28.36) * mm, "end": v(-14.4, -28.66) * mm});
            skLineSegment(sketch, "E408", {"start": v(-14.4, -28.66) * mm, "end": v(-14.46, -28.98) * mm});
            skLineSegment(sketch, "E409", {"start": v(-14.46, -28.98) * mm, "end": v(-14.48, -29.29) * mm});
            skLineSegment(sketch, "E410", {"start": v(-14.48, -29.29) * mm, "end": v(-14.46, -29.6) * mm});
            skLineSegment(sketch, "E411", {"start": v(-14.46, -29.6) * mm, "end": v(-14.4, -29.91) * mm});
            skLineSegment(sketch, "E412", {"start": v(-14.4, -29.91) * mm, "end": v(-14.3, -30.2) * mm});
            skLineSegment(sketch, "E413", {"start": v(-14.3, -30.2) * mm, "end": v(-14.15, -30.5) * mm});
            skLineSegment(sketch, "E414", {"start": v(-14.15, -30.5) * mm, "end": v(-13.97, -30.76) * mm});
            skLineSegment(sketch, "E415", {"start": v(-13.97, -30.76) * mm, "end": v(-13.76, -31) * mm});
            skLineSegment(sketch, "E416", {"start": v(-13.76, -31) * mm, "end": v(-13.52, -31.2) * mm});
            skLineSegment(sketch, "E417", {"start": v(-13.52, -31.2) * mm, "end": v(-13.26, -31.38) * mm});
            skLineSegment(sketch, "E418", {"start": v(-13.26, -31.38) * mm, "end": v(-12.98, -31.52) * mm});
            skLineSegment(sketch, "E419", {"start": v(-12.98, -31.52) * mm, "end": v(-12.68, -31.62) * mm});
            skLineSegment(sketch, "E420", {"start": v(-12.68, -31.62) * mm, "end": v(-12.37, -31.68) * mm});
            skLineSegment(sketch, "E421", {"start": v(-12.37, -31.68) * mm, "end": v(-12.06, -31.7) * mm});
            skLineSegment(sketch, "E422", {"start": v(-12.06, -31.7) * mm, "end": v(-11.73, -31.68) * mm});
            skLineSegment(sketch, "E423", {"start": v(-11.73, -31.68) * mm, "end": v(-11.42, -31.62) * mm});
            skLineSegment(sketch, "E424", {"start": v(-11.42, -31.62) * mm, "end": v(-11.12, -31.52) * mm});
            skLineSegment(sketch, "E425", {"start": v(-11.12, -31.52) * mm, "end": v(-10.84, -31.38) * mm});
            skLineSegment(sketch, "E426", {"start": v(-10.84, -31.38) * mm, "end": v(-10.58, -31.2) * mm});
            skLineSegment(sketch, "E427", {"start": v(-10.58, -31.2) * mm, "end": v(-10.34, -31) * mm});
            skLineSegment(sketch, "E428", {"start": v(-10.34, -31) * mm, "end": v(-10.13, -30.76) * mm});
            skLineSegment(sketch, "E429", {"start": v(-10.13, -30.76) * mm, "end": v(-9.96, -30.5) * mm});
            skLineSegment(sketch, "E430", {"start": v(-9.96, -30.5) * mm, "end": v(-9.82, -30.2) * mm});
            skLineSegment(sketch, "E431", {"start": v(-11.54, -10.9) * mm, "end": v(-11.37, -10.73) * mm});
            skLineSegment(sketch, "E432", {"start": v(-11.37, -10.73) * mm, "end": v(-11.23, -10.53) * mm});
            skLineSegment(sketch, "E433", {"start": v(-11.23, -10.53) * mm, "end": v(-11.14, -10.32) * mm});
            skLineSegment(sketch, "E434", {"start": v(-11.14, -10.32) * mm, "end": v(-11.1, -10.1) * mm});
            skLineSegment(sketch, "E435", {"start": v(-11.1, -10.1) * mm, "end": v(-11.1, -9.86) * mm});
            skLineSegment(sketch, "E436", {"start": v(-11.1, -9.86) * mm, "end": v(-11.14, -9.63) * mm});
            skLineSegment(sketch, "E437", {"start": v(-11.14, -9.63) * mm, "end": v(-11.23, -9.4) * mm});
            skLineSegment(sketch, "E438", {"start": v(-11.23, -9.4) * mm, "end": v(-11.36, -9.2) * mm});
            skLineSegment(sketch, "E439", {"start": v(-11.36, -9.2) * mm, "end": v(-11.53, -9.03) * mm});
            skLineSegment(sketch, "E440", {"start": v(-11.53, -9.03) * mm, "end": v(-11.73, -8.9) * mm});
            skLineSegment(sketch, "E441", {"start": v(-11.73, -8.9) * mm, "end": v(-11.95, -8.8) * mm});
            skLineSegment(sketch, "E442", {"start": v(-11.95, -8.8) * mm, "end": v(-12.18, -8.76) * mm});
            skLineSegment(sketch, "E443", {"start": v(-12.18, -8.76) * mm, "end": v(-12.4, -8.76) * mm});
            skLineSegment(sketch, "E444", {"start": v(-12.4, -8.76) * mm, "end": v(-12.64, -8.8) * mm});
            skLineSegment(sketch, "E445", {"start": v(-12.64, -8.8) * mm, "end": v(-12.86, -8.89) * mm});
            skLineSegment(sketch, "E446", {"start": v(-12.86, -8.89) * mm, "end": v(-13.07, -9.02) * mm});
            skLineSegment(sketch, "E447", {"start": v(-19.88, -24.77) * mm, "end": v(-20.04, -25.04) * mm});
            skLineSegment(sketch, "E448", {"start": v(-20.04, -25.04) * mm, "end": v(-20.17, -25.34) * mm});
            skLineSegment(sketch, "E449", {"start": v(-20.17, -25.34) * mm, "end": v(-20.25, -25.64) * mm});
            skLineSegment(sketch, "E450", {"start": v(-20.25, -25.64) * mm, "end": v(-20.3, -25.95) * mm});
            skLineSegment(sketch, "E451", {"start": v(-20.3, -25.95) * mm, "end": v(-20.3, -26.26) * mm});
            skLineSegment(sketch, "E452", {"start": v(-20.3, -26.26) * mm, "end": v(-20.26, -26.58) * mm});
            skLineSegment(sketch, "E453", {"start": v(-20.26, -26.58) * mm, "end": v(-20.18, -26.88) * mm});
            skLineSegment(sketch, "E454", {"start": v(-20.18, -26.88) * mm, "end": v(-20.06, -27.18) * mm});
            skLineSegment(sketch, "E455", {"start": v(-20.06, -27.18) * mm, "end": v(-19.9, -27.46) * mm});
            skLineSegment(sketch, "E456", {"start": v(-19.9, -27.46) * mm, "end": v(-19.72, -27.72) * mm});
            skLineSegment(sketch, "E457", {"start": v(-19.72, -27.72) * mm, "end": v(-19.5, -27.94) * mm});
            skLineSegment(sketch, "E458", {"start": v(-19.5, -27.94) * mm, "end": v(-19.25, -28.13) * mm});
            skLineSegment(sketch, "E459", {"start": v(-19.25, -28.13) * mm, "end": v(-18.98, -28.3) * mm});
            skLineSegment(sketch, "E460", {"start": v(-18.98, -28.3) * mm, "end": v(-18.69, -28.42) * mm});
            skLineSegment(sketch, "E461", {"start": v(-18.69, -28.42) * mm, "end": v(-18.38, -28.5) * mm});
            skLineSegment(sketch, "E462", {"start": v(-18.38, -28.5) * mm, "end": v(-18.07, -28.55) * mm});
            skLineSegment(sketch, "E463", {"start": v(-18.07, -28.55) * mm, "end": v(-17.74, -28.55) * mm});
            skLineSegment(sketch, "E464", {"start": v(-17.74, -28.55) * mm, "end": v(-17.43, -28.52) * mm});
            skLineSegment(sketch, "E465", {"start": v(-17.43, -28.52) * mm, "end": v(-17.12, -28.44) * mm});
            skLineSegment(sketch, "E466", {"start": v(-17.12, -28.44) * mm, "end": v(-16.83, -28.32) * mm});
            skLineSegment(sketch, "E467", {"start": v(-16.83, -28.32) * mm, "end": v(-16.56, -28.17) * mm});
            skLineSegment(sketch, "E468", {"start": v(-16.56, -28.17) * mm, "end": v(-16.3, -27.98) * mm});
            skLineSegment(sketch, "E469", {"start": v(-16.3, -27.98) * mm, "end": v(-16.08, -27.76) * mm});
            skLineSegment(sketch, "E470", {"start": v(-16.08, -27.76) * mm, "end": v(-15.88, -27.5) * mm});
            skLineSegment(sketch, "E471", {"start": v(-13.56, -8.27) * mm, "end": v(-13.35, -8.13) * mm});
            skLineSegment(sketch, "E472", {"start": v(-13.35, -8.13) * mm, "end": v(-13.18, -7.97) * mm});
            skLineSegment(sketch, "E473", {"start": v(-13.18, -7.97) * mm, "end": v(-13.05, -7.78) * mm});
            skLineSegment(sketch, "E474", {"start": v(-13.05, -7.78) * mm, "end": v(-12.95, -7.56) * mm});
            skLineSegment(sketch, "E475", {"start": v(-12.95, -7.56) * mm, "end": v(-12.9, -7.34) * mm});
            skLineSegment(sketch, "E476", {"start": v(-12.9, -7.34) * mm, "end": v(-12.9, -7.1) * mm});
            skLineSegment(sketch, "E477", {"start": v(-12.9, -7.1) * mm, "end": v(-12.94, -6.87) * mm});
            skLineSegment(sketch, "E478", {"start": v(-12.94, -6.87) * mm, "end": v(-13.03, -6.64) * mm});
            skLineSegment(sketch, "E479", {"start": v(-13.03, -6.64) * mm, "end": v(-13.16, -6.43) * mm});
            skLineSegment(sketch, "E480", {"start": v(-13.16, -6.43) * mm, "end": v(-13.33, -6.26) * mm});
            skLineSegment(sketch, "E481", {"start": v(-13.33, -6.26) * mm, "end": v(-13.52, -6.13) * mm});
            skLineSegment(sketch, "E482", {"start": v(-13.52, -6.13) * mm, "end": v(-13.73, -6.04) * mm});
            skLineSegment(sketch, "E483", {"start": v(-13.73, -6.04) * mm, "end": v(-13.96, -5.99) * mm});
            skLineSegment(sketch, "E484", {"start": v(-13.96, -5.99) * mm, "end": v(-14.2, -5.98) * mm});
            skLineSegment(sketch, "E485", {"start": v(-14.2, -5.98) * mm, "end": v(-14.43, -6.02) * mm});
            skLineSegment(sketch, "E486", {"start": v(-14.43, -6.02) * mm, "end": v(-14.66, -6.1) * mm});
            skLineSegment(sketch, "E487", {"start": v(-24.6, -20.1) * mm, "end": v(-24.81, -20.33) * mm});
            skLineSegment(sketch, "E488", {"start": v(-24.81, -20.33) * mm, "end": v(-25, -20.59) * mm});
            skLineSegment(sketch, "E489", {"start": v(-25, -20.59) * mm, "end": v(-25.14, -20.87) * mm});
            skLineSegment(sketch, "E490", {"start": v(-25.14, -20.87) * mm, "end": v(-25.25, -21.16) * mm});
            skLineSegment(sketch, "E491", {"start": v(-25.25, -21.16) * mm, "end": v(-25.32, -21.47) * mm});
            skLineSegment(sketch, "E492", {"start": v(-25.32, -21.47) * mm, "end": v(-25.34, -21.78) * mm});
            skLineSegment(sketch, "E493", {"start": v(-25.34, -21.78) * mm, "end": v(-25.33, -22.1) * mm});
            skLineSegment(sketch, "E494", {"start": v(-25.33, -22.1) * mm, "end": v(-25.28, -22.42) * mm});
            skLineSegment(sketch, "E495", {"start": v(-25.28, -22.42) * mm, "end": v(-25.18, -22.72) * mm});
            skLineSegment(sketch, "E496", {"start": v(-25.18, -22.72) * mm, "end": v(-25.05, -23.01) * mm});
            skLineSegment(sketch, "E497", {"start": v(-25.05, -23.01) * mm, "end": v(-24.88, -23.28) * mm});
            skLineSegment(sketch, "E498", {"start": v(-24.88, -23.28) * mm, "end": v(-24.68, -23.52) * mm});
            skLineSegment(sketch, "E499", {"start": v(-24.68, -23.52) * mm, "end": v(-24.45, -23.73) * mm});
            skLineSegment(sketch, "E500", {"start": v(-24.45, -23.73) * mm, "end": v(-24.19, -23.91) * mm});
            skLineSegment(sketch, "E501", {"start": v(-24.19, -23.91) * mm, "end": v(-23.9, -24.06) * mm});
            skLineSegment(sketch, "E502", {"start": v(-23.9, -24.06) * mm, "end": v(-23.6, -24.17) * mm});
            skLineSegment(sketch, "E503", {"start": v(-23.6, -24.17) * mm, "end": v(-23.3, -24.24) * mm});
            skLineSegment(sketch, "E504", {"start": v(-23.3, -24.24) * mm, "end": v(-22.98, -24.27) * mm});
            skLineSegment(sketch, "E505", {"start": v(-22.98, -24.27) * mm, "end": v(-22.66, -24.25) * mm});
            skLineSegment(sketch, "E506", {"start": v(-22.66, -24.25) * mm, "end": v(-22.35, -24.2) * mm});
            skLineSegment(sketch, "E507", {"start": v(-22.35, -24.2) * mm, "end": v(-22.05, -24.1) * mm});
            skLineSegment(sketch, "E508", {"start": v(-22.05, -24.1) * mm, "end": v(-21.77, -23.97) * mm});
            skLineSegment(sketch, "E509", {"start": v(-21.77, -23.97) * mm, "end": v(-21.5, -23.8) * mm});
            skLineSegment(sketch, "E510", {"start": v(-21.5, -23.8) * mm, "end": v(-21.25, -23.6) * mm});
            skLineSegment(sketch, "E511", {"start": v(-14.98, -5.27) * mm, "end": v(-14.75, -5.18) * mm});
            skLineSegment(sketch, "E512", {"start": v(-14.75, -5.18) * mm, "end": v(-14.55, -5.05) * mm});
            skLineSegment(sketch, "E513", {"start": v(-14.55, -5.05) * mm, "end": v(-14.38, -4.9) * mm});
            skLineSegment(sketch, "E514", {"start": v(-14.38, -4.9) * mm, "end": v(-14.24, -4.7) * mm});
            skLineSegment(sketch, "E515", {"start": v(-14.24, -4.7) * mm, "end": v(-14.15, -4.5) * mm});
            skLineSegment(sketch, "E516", {"start": v(-14.15, -4.5) * mm, "end": v(-14.1, -4.26) * mm});
            skLineSegment(sketch, "E517", {"start": v(-14.1, -4.26) * mm, "end": v(-14.08, -4.03) * mm});
            skLineSegment(sketch, "E518", {"start": v(-14.08, -4.03) * mm, "end": v(-14.12, -3.78) * mm});
            skLineSegment(sketch, "E519", {"start": v(-14.12, -3.78) * mm, "end": v(-14.2, -3.56) * mm});
            skLineSegment(sketch, "E520", {"start": v(-14.2, -3.56) * mm, "end": v(-14.34, -3.35) * mm});
            skLineSegment(sketch, "E521", {"start": v(-14.34, -3.35) * mm, "end": v(-14.5, -3.18) * mm});
            skLineSegment(sketch, "E522", {"start": v(-14.5, -3.18) * mm, "end": v(-14.69, -3.05) * mm});
            skLineSegment(sketch, "E523", {"start": v(-14.69, -3.05) * mm, "end": v(-14.9, -2.95) * mm});
            skLineSegment(sketch, "E524", {"start": v(-14.9, -2.95) * mm, "end": v(-15.13, -2.9) * mm});
            skLineSegment(sketch, "E525", {"start": v(-15.13, -2.9) * mm, "end": v(-15.36, -2.89) * mm});
            skLineSegment(sketch, "E526", {"start": v(-15.36, -2.89) * mm, "end": v(-15.6, -2.93) * mm});
            skLineSegment(sketch, "E527", {"start": v(-28.23, -14.54) * mm, "end": v(-28.5, -14.73) * mm});
            skLineSegment(sketch, "E528", {"start": v(-28.5, -14.73) * mm, "end": v(-28.73, -14.94) * mm});
            skLineSegment(sketch, "E529", {"start": v(-28.73, -14.94) * mm, "end": v(-28.93, -15.18) * mm});
            skLineSegment(sketch, "E530", {"start": v(-28.93, -15.18) * mm, "end": v(-29.1, -15.45) * mm});
            skLineSegment(sketch, "E531", {"start": v(-29.1, -15.45) * mm, "end": v(-29.23, -15.74) * mm});
            skLineSegment(sketch, "E532", {"start": v(-29.23, -15.74) * mm, "end": v(-29.32, -16.04) * mm});
            skLineSegment(sketch, "E533", {"start": v(-29.32, -16.04) * mm, "end": v(-29.37, -16.35) * mm});
            skLineSegment(sketch, "E534", {"start": v(-29.37, -16.35) * mm, "end": v(-29.39, -16.67) * mm});
            skLineSegment(sketch, "E535", {"start": v(-29.39, -16.67) * mm, "end": v(-29.36, -17) * mm});
            skLineSegment(sketch, "E536", {"start": v(-29.36, -17) * mm, "end": v(-29.28, -17.3) * mm});
            skLineSegment(sketch, "E537", {"start": v(-29.28, -17.3) * mm, "end": v(-29.17, -17.6) * mm});
            skLineSegment(sketch, "E538", {"start": v(-29.17, -17.6) * mm, "end": v(-29.03, -17.87) * mm});
            skLineSegment(sketch, "E539", {"start": v(-29.03, -17.87) * mm, "end": v(-28.85, -18.13) * mm});
            skLineSegment(sketch, "E540", {"start": v(-28.85, -18.13) * mm, "end": v(-28.63, -18.36) * mm});
            skLineSegment(sketch, "E541", {"start": v(-28.63, -18.36) * mm, "end": v(-28.39, -18.56) * mm});
            skLineSegment(sketch, "E542", {"start": v(-28.39, -18.56) * mm, "end": v(-28.12, -18.73) * mm});
            skLineSegment(sketch, "E543", {"start": v(-28.12, -18.73) * mm, "end": v(-27.82, -18.87) * mm});
            skLineSegment(sketch, "E544", {"start": v(-27.82, -18.87) * mm, "end": v(-27.52, -18.96) * mm});
            skLineSegment(sketch, "E545", {"start": v(-27.52, -18.96) * mm, "end": v(-27.2, -19.01) * mm});
            skLineSegment(sketch, "E546", {"start": v(-27.2, -19.01) * mm, "end": v(-26.9, -19.02) * mm});
            skLineSegment(sketch, "E547", {"start": v(-26.9, -19.02) * mm, "end": v(-26.58, -19) * mm});
            skLineSegment(sketch, "E548", {"start": v(-26.58, -19) * mm, "end": v(-26.28, -18.93) * mm});
            skLineSegment(sketch, "E549", {"start": v(-26.28, -18.93) * mm, "end": v(-25.98, -18.82) * mm});
            skLineSegment(sketch, "E550", {"start": v(-25.98, -18.82) * mm, "end": v(-25.7, -18.66) * mm});
            skLineSegment(sketch, "E551", {"start": v(-15.75, -2.04) * mm, "end": v(-15.5, -2) * mm});
            skLineSegment(sketch, "E552", {"start": v(-15.5, -2) * mm, "end": v(-15.28, -1.92) * mm});
            skLineSegment(sketch, "E553", {"start": v(-15.28, -1.92) * mm, "end": v(-15.08, -1.8) * mm});
            skLineSegment(sketch, "E554", {"start": v(-15.08, -1.8) * mm, "end": v(-14.9, -1.64) * mm});
            skLineSegment(sketch, "E555", {"start": v(-14.9, -1.64) * mm, "end": v(-14.77, -1.45) * mm});
            skLineSegment(sketch, "E556", {"start": v(-14.77, -1.45) * mm, "end": v(-14.67, -1.24) * mm});
            skLineSegment(sketch, "E557", {"start": v(-14.67, -1.24) * mm, "end": v(-14.61, -1.01) * mm});
            skLineSegment(sketch, "E558", {"start": v(-14.61, -1.01) * mm, "end": v(-14.6, -0.77) * mm});
            skLineSegment(sketch, "E559", {"start": v(-14.6, -0.77) * mm, "end": v(-14.64, -0.52) * mm});
            skLineSegment(sketch, "E560", {"start": v(-14.64, -0.52) * mm, "end": v(-14.72, -0.3) * mm});
            skLineSegment(sketch, "E561", {"start": v(-14.72, -0.3) * mm, "end": v(-14.84, -0.1) * mm});
            skLineSegment(sketch, "E562", {"start": v(-14.84, -0.1) * mm, "end": v(-15, 0.07) * mm});
            skLineSegment(sketch, "E563", {"start": v(-15, 0.07) * mm, "end": v(-15.19, 0.2) * mm});
            skLineSegment(sketch, "E564", {"start": v(-15.19, 0.2) * mm, "end": v(-15.4, 0.31) * mm});
            skLineSegment(sketch, "E565", {"start": v(-15.4, 0.31) * mm, "end": v(-15.63, 0.37) * mm});
            skLineSegment(sketch, "E566", {"start": v(-15.63, 0.37) * mm, "end": v(-15.87, 0.38) * mm});
            skLineSegment(sketch, "E567", {"start": v(-30.64, -8.35) * mm, "end": v(-30.93, -8.48) * mm});
            skLineSegment(sketch, "E568", {"start": v(-30.93, -8.48) * mm, "end": v(-31.2, -8.64) * mm});
            skLineSegment(sketch, "E569", {"start": v(-31.2, -8.64) * mm, "end": v(-31.45, -8.84) * mm});
            skLineSegment(sketch, "E570", {"start": v(-31.45, -8.84) * mm, "end": v(-31.67, -9.06) * mm});
            skLineSegment(sketch, "E571", {"start": v(-31.67, -9.06) * mm, "end": v(-31.86, -9.31) * mm});
            skLineSegment(sketch, "E572", {"start": v(-31.86, -9.31) * mm, "end": v(-32.01, -9.59) * mm});
            skLineSegment(sketch, "E573", {"start": v(-32.01, -9.59) * mm, "end": v(-32.13, -9.88) * mm});
            skLineSegment(sketch, "E574", {"start": v(-32.13, -9.88) * mm, "end": v(-32.2, -10.2) * mm});
            skLineSegment(sketch, "E575", {"start": v(-32.2, -10.2) * mm, "end": v(-32.25, -10.52) * mm});
            skLineSegment(sketch, "E576", {"start": v(-32.25, -10.52) * mm, "end": v(-32.24, -10.83) * mm});
            skLineSegment(sketch, "E577", {"start": v(-32.24, -10.83) * mm, "end": v(-32.2, -11.14) * mm});
            skLineSegment(sketch, "E578", {"start": v(-32.2, -11.14) * mm, "end": v(-32.1, -11.45) * mm});
            skLineSegment(sketch, "E579", {"start": v(-32.1, -11.45) * mm, "end": v(-31.98, -11.73) * mm});
            skLineSegment(sketch, "E580", {"start": v(-31.98, -11.73) * mm, "end": v(-31.82, -12) * mm});
            skLineSegment(sketch, "E581", {"start": v(-31.82, -12) * mm, "end": v(-31.63, -12.25) * mm});
            skLineSegment(sketch, "E582", {"start": v(-31.63, -12.25) * mm, "end": v(-31.4, -12.48) * mm});
            skLineSegment(sketch, "E583", {"start": v(-31.4, -12.48) * mm, "end": v(-31.14, -12.67) * mm});
            skLineSegment(sketch, "E584", {"start": v(-31.14, -12.67) * mm, "end": v(-30.86, -12.82) * mm});
            skLineSegment(sketch, "E585", {"start": v(-30.86, -12.82) * mm, "end": v(-30.57, -12.94) * mm});
            skLineSegment(sketch, "E586", {"start": v(-30.57, -12.94) * mm, "end": v(-30.26, -13.02) * mm});
            skLineSegment(sketch, "E587", {"start": v(-30.26, -13.02) * mm, "end": v(-29.95, -13.05) * mm});
            skLineSegment(sketch, "E588", {"start": v(-29.95, -13.05) * mm, "end": v(-29.64, -13.05) * mm});
            skLineSegment(sketch, "E589", {"start": v(-29.64, -13.05) * mm, "end": v(-29.32, -13) * mm});
            skLineSegment(sketch, "E590", {"start": v(-29.32, -13) * mm, "end": v(-29.01, -12.91) * mm});
            skLineSegment(sketch, "E591", {"start": v(-15.83, 1.28) * mm, "end": v(-15.58, 1.27) * mm});
            skLineSegment(sketch, "E592", {"start": v(-15.58, 1.27) * mm, "end": v(-15.35, 1.3) * mm});
            skLineSegment(sketch, "E593", {"start": v(-15.35, 1.3) * mm, "end": v(-15.12, 1.38) * mm});
            skLineSegment(sketch, "E594", {"start": v(-15.12, 1.38) * mm, "end": v(-14.92, 1.5) * mm});
            skLineSegment(sketch, "E595", {"start": v(-14.92, 1.5) * mm, "end": v(-14.75, 1.65) * mm});
            skLineSegment(sketch, "E596", {"start": v(-14.75, 1.65) * mm, "end": v(-14.6, 1.84) * mm});
            skLineSegment(sketch, "E597", {"start": v(-14.6, 1.84) * mm, "end": v(-14.5, 2.05) * mm});
            skLineSegment(sketch, "E598", {"start": v(-14.5, 2.05) * mm, "end": v(-14.44, 2.29) * mm});
            skLineSegment(sketch, "E599", {"start": v(-14.44, 2.29) * mm, "end": v(-14.43, 2.53) * mm});
            skLineSegment(sketch, "E600", {"start": v(-14.43, 2.53) * mm, "end": v(-14.46, 2.77) * mm});
            skLineSegment(sketch, "E601", {"start": v(-14.46, 2.77) * mm, "end": v(-14.54, 2.99) * mm});
            skLineSegment(sketch, "E602", {"start": v(-14.54, 2.99) * mm, "end": v(-14.66, 3.19) * mm});
            skLineSegment(sketch, "E603", {"start": v(-14.66, 3.19) * mm, "end": v(-14.81, 3.36) * mm});
            skLineSegment(sketch, "E604", {"start": v(-14.81, 3.36) * mm, "end": v(-15, 3.5) * mm});
            skLineSegment(sketch, "E605", {"start": v(-15, 3.5) * mm, "end": v(-15.2, 3.61) * mm});
            skLineSegment(sketch, "E606", {"start": v(-15.2, 3.61) * mm, "end": v(-15.45, 3.67) * mm});
            skLineSegment(sketch, "E607", {"start": v(-31.7, -1.8) * mm, "end": v(-32.02, -1.86) * mm});
            skLineSegment(sketch, "E608", {"start": v(-32.02, -1.86) * mm, "end": v(-32.32, -1.96) * mm});
            skLineSegment(sketch, "E609", {"start": v(-32.32, -1.96) * mm, "end": v(-32.6, -2.1) * mm});
            skLineSegment(sketch, "E610", {"start": v(-32.6, -2.1) * mm, "end": v(-32.86, -2.28) * mm});
            skLineSegment(sketch, "E611", {"start": v(-32.86, -2.28) * mm, "end": v(-33.1, -2.49) * mm});
            skLineSegment(sketch, "E612", {"start": v(-33.1, -2.49) * mm, "end": v(-33.3, -2.72) * mm});
            skLineSegment(sketch, "E613", {"start": v(-33.3, -2.72) * mm, "end": v(-33.48, -2.99) * mm});
            skLineSegment(sketch, "E614", {"start": v(-33.48, -2.99) * mm, "end": v(-33.63, -3.28) * mm});
            skLineSegment(sketch, "E615", {"start": v(-33.63, -3.28) * mm, "end": v(-33.73, -3.58) * mm});
            skLineSegment(sketch, "E616", {"start": v(-33.73, -3.58) * mm, "end": v(-33.79, -3.9) * mm});
            skLineSegment(sketch, "E617", {"start": v(-33.79, -3.9) * mm, "end": v(-33.8, -4.2) * mm});
            skLineSegment(sketch, "E618", {"start": v(-33.8, -4.2) * mm, "end": v(-33.79, -4.52) * mm});
            skLineSegment(sketch, "E619", {"start": v(-33.79, -4.52) * mm, "end": v(-33.72, -4.83) * mm});
            skLineSegment(sketch, "E620", {"start": v(-33.72, -4.83) * mm, "end": v(-33.62, -5.13) * mm});
            skLineSegment(sketch, "E621", {"start": v(-33.62, -5.13) * mm, "end": v(-33.48, -5.41) * mm});
            skLineSegment(sketch, "E622", {"start": v(-33.48, -5.41) * mm, "end": v(-33.3, -5.68) * mm});
            skLineSegment(sketch, "E623", {"start": v(-33.3, -5.68) * mm, "end": v(-33.1, -5.92) * mm});
            skLineSegment(sketch, "E624", {"start": v(-33.1, -5.92) * mm, "end": v(-32.85, -6.13) * mm});
            skLineSegment(sketch, "E625", {"start": v(-32.85, -6.13) * mm, "end": v(-32.59, -6.3) * mm});
            skLineSegment(sketch, "E626", {"start": v(-32.59, -6.3) * mm, "end": v(-32.3, -6.44) * mm});
            skLineSegment(sketch, "E627", {"start": v(-32.3, -6.44) * mm, "end": v(-32.01, -6.54) * mm});
            skLineSegment(sketch, "E628", {"start": v(-32.01, -6.54) * mm, "end": v(-31.7, -6.6) * mm});
            skLineSegment(sketch, "E629", {"start": v(-31.7, -6.6) * mm, "end": v(-31.38, -6.62) * mm});
            skLineSegment(sketch, "E630", {"start": v(-31.38, -6.62) * mm, "end": v(-31.06, -6.6) * mm});
            skLineSegment(sketch, "E631", {"start": v(-15.21, 4.54) * mm, "end": v(-14.98, 4.48) * mm});
            skLineSegment(sketch, "E632", {"start": v(-14.98, 4.48) * mm, "end": v(-14.74, 4.46) * mm});
            skLineSegment(sketch, "E633", {"start": v(-14.74, 4.46) * mm, "end": v(-14.5, 4.5) * mm});
            skLineSegment(sketch, "E634", {"start": v(-14.5, 4.5) * mm, "end": v(-14.29, 4.57) * mm});
            skLineSegment(sketch, "E635", {"start": v(-14.29, 4.57) * mm, "end": v(-14.08, 4.68) * mm});
            skLineSegment(sketch, "E636", {"start": v(-14.08, 4.68) * mm, "end": v(-13.9, 4.83) * mm});
            skLineSegment(sketch, "E637", {"start": v(-13.9, 4.83) * mm, "end": v(-13.76, 5.02) * mm});
            skLineSegment(sketch, "E638", {"start": v(-13.76, 5.02) * mm, "end": v(-13.65, 5.24) * mm});
            skLineSegment(sketch, "E639", {"start": v(-13.65, 5.24) * mm, "end": v(-13.58, 5.48) * mm});
            skLineSegment(sketch, "E640", {"start": v(-13.58, 5.48) * mm, "end": v(-13.57, 5.71) * mm});
            skLineSegment(sketch, "E641", {"start": v(-13.57, 5.71) * mm, "end": v(-13.6, 5.95) * mm});
            skLineSegment(sketch, "E642", {"start": v(-13.6, 5.95) * mm, "end": v(-13.67, 6.17) * mm});
            skLineSegment(sketch, "E643", {"start": v(-13.67, 6.17) * mm, "end": v(-13.79, 6.37) * mm});
            skLineSegment(sketch, "E644", {"start": v(-13.79, 6.37) * mm, "end": v(-13.94, 6.55) * mm});
            skLineSegment(sketch, "E645", {"start": v(-13.94, 6.55) * mm, "end": v(-14.13, 6.7) * mm});
            skLineSegment(sketch, "E646", {"start": v(-14.13, 6.7) * mm, "end": v(-14.35, 6.8) * mm});
            skLineSegment(sketch, "E647", {"start": v(-31.39, 4.83) * mm, "end": v(-31.7, 4.84) * mm});
            skLineSegment(sketch, "E648", {"start": v(-31.7, 4.84) * mm, "end": v(-32.02, 4.8) * mm});
            skLineSegment(sketch, "E649", {"start": v(-32.02, 4.8) * mm, "end": v(-32.33, 4.72) * mm});
            skLineSegment(sketch, "E650", {"start": v(-32.33, 4.72) * mm, "end": v(-32.62, 4.6) * mm});
            skLineSegment(sketch, "E651", {"start": v(-32.62, 4.6) * mm, "end": v(-32.9, 4.45) * mm});
            skLineSegment(sketch, "E652", {"start": v(-32.9, 4.45) * mm, "end": v(-33.15, 4.26) * mm});
            skLineSegment(sketch, "E653", {"start": v(-33.15, 4.26) * mm, "end": v(-33.37, 4.04) * mm});
            skLineSegment(sketch, "E654", {"start": v(-33.37, 4.04) * mm, "end": v(-33.57, 3.79) * mm});
            skLineSegment(sketch, "E655", {"start": v(-33.57, 3.79) * mm, "end": v(-33.74, 3.5) * mm});
            skLineSegment(sketch, "E656", {"start": v(-33.74, 3.5) * mm, "end": v(-33.86, 3.22) * mm});
            skLineSegment(sketch, "E657", {"start": v(-33.86, 3.22) * mm, "end": v(-33.94, 2.91) * mm});
            skLineSegment(sketch, "E658", {"start": v(-33.94, 2.91) * mm, "end": v(-33.99, 2.6) * mm});
            skLineSegment(sketch, "E659", {"start": v(-33.99, 2.6) * mm, "end": v(-34, 2.3) * mm});
            skLineSegment(sketch, "E660", {"start": v(-34, 2.3) * mm, "end": v(-33.95, 1.98) * mm});
            skLineSegment(sketch, "E661", {"start": v(-33.95, 1.98) * mm, "end": v(-33.88, 1.67) * mm});
            skLineSegment(sketch, "E662", {"start": v(-33.88, 1.67) * mm, "end": v(-33.76, 1.37) * mm});
            skLineSegment(sketch, "E663", {"start": v(-33.76, 1.37) * mm, "end": v(-33.6, 1.1) * mm});
            skLineSegment(sketch, "E664", {"start": v(-33.6, 1.1) * mm, "end": v(-33.4, 0.84) * mm});
            skLineSegment(sketch, "E665", {"start": v(-33.4, 0.84) * mm, "end": v(-33.19, 0.61) * mm});
            skLineSegment(sketch, "E666", {"start": v(-33.19, 0.61) * mm, "end": v(-32.94, 0.42) * mm});
            skLineSegment(sketch, "E667", {"start": v(-32.94, 0.42) * mm, "end": v(-32.67, 0.26) * mm});
            skLineSegment(sketch, "E668", {"start": v(-32.67, 0.26) * mm, "end": v(-32.38, 0.14) * mm});
            skLineSegment(sketch, "E669", {"start": v(-32.38, 0.14) * mm, "end": v(-32.08, 0.05) * mm});
            skLineSegment(sketch, "E670", {"start": v(-32.08, 0.05) * mm, "end": v(-31.76, 0) * mm});
            skLineSegment(sketch, "E671", {"start": v(-13.94, 7.6) * mm, "end": v(-13.72, 7.5) * mm});
            skLineSegment(sketch, "E672", {"start": v(-13.72, 7.5) * mm, "end": v(-13.49, 7.43) * mm});
            skLineSegment(sketch, "E673", {"start": v(-13.49, 7.43) * mm, "end": v(-13.26, 7.41) * mm});
            skLineSegment(sketch, "E674", {"start": v(-13.26, 7.41) * mm, "end": v(-13.03, 7.44) * mm});
            skLineSegment(sketch, "E675", {"start": v(-13.03, 7.44) * mm, "end": v(-12.8, 7.5) * mm});
            skLineSegment(sketch, "E676", {"start": v(-12.8, 7.5) * mm, "end": v(-12.6, 7.62) * mm});
            skLineSegment(sketch, "E677", {"start": v(-12.6, 7.62) * mm, "end": v(-12.41, 7.77) * mm});
            skLineSegment(sketch, "E678", {"start": v(-12.41, 7.77) * mm, "end": v(-12.26, 7.96) * mm});
            skLineSegment(sketch, "E679", {"start": v(-12.26, 7.96) * mm, "end": v(-12.15, 8.18) * mm});
            skLineSegment(sketch, "E680", {"start": v(-12.15, 8.18) * mm, "end": v(-12.08, 8.41) * mm});
            skLineSegment(sketch, "E681", {"start": v(-12.08, 8.41) * mm, "end": v(-12.07, 8.64) * mm});
            skLineSegment(sketch, "E682", {"start": v(-12.07, 8.64) * mm, "end": v(-12.1, 8.88) * mm});
            skLineSegment(sketch, "E683", {"start": v(-12.1, 8.88) * mm, "end": v(-12.16, 9.1) * mm});
            skLineSegment(sketch, "E684", {"start": v(-12.16, 9.1) * mm, "end": v(-12.27, 9.3) * mm});
            skLineSegment(sketch, "E685", {"start": v(-12.27, 9.3) * mm, "end": v(-12.43, 9.49) * mm});
            skLineSegment(sketch, "E686", {"start": v(-12.43, 9.49) * mm, "end": v(-12.62, 9.64) * mm});
            skLineSegment(sketch, "E687", {"start": v(-29.7, 11.25) * mm, "end": v(-30.01, 11.32) * mm});
            skLineSegment(sketch, "E688", {"start": v(-30.01, 11.32) * mm, "end": v(-30.33, 11.35) * mm});
            skLineSegment(sketch, "E689", {"start": v(-30.33, 11.35) * mm, "end": v(-30.64, 11.34) * mm});
            skLineSegment(sketch, "E690", {"start": v(-30.64, 11.34) * mm, "end": v(-30.95, 11.28) * mm});
            skLineSegment(sketch, "E691", {"start": v(-30.95, 11.28) * mm, "end": v(-31.25, 11.2) * mm});
            skLineSegment(sketch, "E692", {"start": v(-31.25, 11.2) * mm, "end": v(-31.54, 11.06) * mm});
            skLineSegment(sketch, "E693", {"start": v(-31.54, 11.06) * mm, "end": v(-31.8, 10.9) * mm});
            skLineSegment(sketch, "E694", {"start": v(-31.8, 10.9) * mm, "end": v(-32.05, 10.68) * mm});
            skLineSegment(sketch, "E695", {"start": v(-32.05, 10.68) * mm, "end": v(-32.27, 10.45) * mm});
            skLineSegment(sketch, "E696", {"start": v(-32.27, 10.45) * mm, "end": v(-32.45, 10.19) * mm});
            skLineSegment(sketch, "E697", {"start": v(-32.45, 10.19) * mm, "end": v(-32.6, 9.9) * mm});
            skLineSegment(sketch, "E698", {"start": v(-32.6, 9.9) * mm, "end": v(-32.7, 9.61) * mm});
            skLineSegment(sketch, "E699", {"start": v(-32.7, 9.61) * mm, "end": v(-32.77, 9.3) * mm});
            skLineSegment(sketch, "E700", {"start": v(-32.77, 9.3) * mm, "end": v(-32.8, 9) * mm});
            skLineSegment(sketch, "E701", {"start": v(-32.8, 9) * mm, "end": v(-32.79, 8.68) * mm});
            skLineSegment(sketch, "E702", {"start": v(-32.79, 8.68) * mm, "end": v(-32.73, 8.36) * mm});
            skLineSegment(sketch, "E703", {"start": v(-32.73, 8.36) * mm, "end": v(-32.64, 8.05) * mm});
            skLineSegment(sketch, "E704", {"start": v(-32.64, 8.05) * mm, "end": v(-32.5, 7.77) * mm});
            skLineSegment(sketch, "E705", {"start": v(-32.5, 7.77) * mm, "end": v(-32.33, 7.5) * mm});
            skLineSegment(sketch, "E706", {"start": v(-32.33, 7.5) * mm, "end": v(-32.13, 7.26) * mm});
            skLineSegment(sketch, "E707", {"start": v(-32.13, 7.26) * mm, "end": v(-31.9, 7.05) * mm});
            skLineSegment(sketch, "E708", {"start": v(-31.9, 7.05) * mm, "end": v(-31.65, 6.86) * mm});
            skLineSegment(sketch, "E709", {"start": v(-31.65, 6.86) * mm, "end": v(-31.36, 6.72) * mm});
            skLineSegment(sketch, "E710", {"start": v(-31.36, 6.72) * mm, "end": v(-31.06, 6.6) * mm});
            skLineSegment(sketch, "E711", {"start": v(-12.05, 10.34) * mm, "end": v(-11.86, 10.18) * mm});
            skLineSegment(sketch, "E712", {"start": v(-11.86, 10.18) * mm, "end": v(-11.65, 10.07) * mm});
            skLineSegment(sketch, "E713", {"start": v(-11.65, 10.07) * mm, "end": v(-11.43, 10) * mm});
            skLineSegment(sketch, "E714", {"start": v(-11.43, 10) * mm, "end": v(-11.2, 9.98) * mm});
            skLineSegment(sketch, "E715", {"start": v(-11.2, 9.98) * mm, "end": v(-10.96, 10) * mm});
            skLineSegment(sketch, "E716", {"start": v(-10.96, 10) * mm, "end": v(-10.74, 10.07) * mm});
            skLineSegment(sketch, "E717", {"start": v(-10.74, 10.07) * mm, "end": v(-10.53, 10.18) * mm});
            skLineSegment(sketch, "E718", {"start": v(-10.53, 10.18) * mm, "end": v(-10.34, 10.34) * mm});
            skLineSegment(sketch, "E719", {"start": v(-10.34, 10.34) * mm, "end": v(-10.18, 10.53) * mm});
            skLineSegment(sketch, "E720", {"start": v(-10.18, 10.53) * mm, "end": v(-10.07, 10.74) * mm});
            skLineSegment(sketch, "E721", {"start": v(-10.07, 10.74) * mm, "end": v(-10, 10.96) * mm});
            skLineSegment(sketch, "E722", {"start": v(-10, 10.96) * mm, "end": v(-9.98, 11.2) * mm});
            skLineSegment(sketch, "E723", {"start": v(-9.98, 11.2) * mm, "end": v(-10, 11.43) * mm});
            skLineSegment(sketch, "E724", {"start": v(-10, 11.43) * mm, "end": v(-10.07, 11.65) * mm});
            skLineSegment(sketch, "E725", {"start": v(-10.07, 11.65) * mm, "end": v(-10.18, 11.86) * mm});
            skLineSegment(sketch, "E726", {"start": v(-10.18, 11.86) * mm, "end": v(-10.34, 12.05) * mm});
            skLineSegment(sketch, "E727", {"start": v(-26.7, 17.18) * mm, "end": v(-27, 17.32) * mm});
            skLineSegment(sketch, "E728", {"start": v(-27, 17.32) * mm, "end": v(-27.3, 17.41) * mm});
            skLineSegment(sketch, "E729", {"start": v(-27.3, 17.41) * mm, "end": v(-27.61, 17.46) * mm});
            skLineSegment(sketch, "E730", {"start": v(-27.61, 17.46) * mm, "end": v(-27.93, 17.47) * mm});
            skLineSegment(sketch, "E731", {"start": v(-27.93, 17.47) * mm, "end": v(-28.24, 17.44) * mm});
            skLineSegment(sketch, "E732", {"start": v(-28.24, 17.44) * mm, "end": v(-28.55, 17.37) * mm});
            skLineSegment(sketch, "E733", {"start": v(-28.55, 17.37) * mm, "end": v(-28.84, 17.27) * mm});
            skLineSegment(sketch, "E734", {"start": v(-28.84, 17.27) * mm, "end": v(-29.13, 17.11) * mm});
            skLineSegment(sketch, "E735", {"start": v(-29.13, 17.11) * mm, "end": v(-29.4, 16.93) * mm});
            skLineSegment(sketch, "E736", {"start": v(-29.4, 16.93) * mm, "end": v(-29.62, 16.71) * mm});
            skLineSegment(sketch, "E737", {"start": v(-29.62, 16.71) * mm, "end": v(-29.82, 16.47) * mm});
            skLineSegment(sketch, "E738", {"start": v(-29.82, 16.47) * mm, "end": v(-30, 16.2) * mm});
            skLineSegment(sketch, "E739", {"start": v(-30, 16.2) * mm, "end": v(-30.12, 15.92) * mm});
            skLineSegment(sketch, "E740", {"start": v(-30.12, 15.92) * mm, "end": v(-30.21, 15.62) * mm});
            skLineSegment(sketch, "E741", {"start": v(-30.21, 15.62) * mm, "end": v(-30.27, 15.3) * mm});
            skLineSegment(sketch, "E742", {"start": v(-30.27, 15.3) * mm, "end": v(-30.28, 14.98) * mm});
            skLineSegment(sketch, "E743", {"start": v(-30.28, 14.98) * mm, "end": v(-30.25, 14.66) * mm});
            skLineSegment(sketch, "E744", {"start": v(-30.25, 14.66) * mm, "end": v(-30.18, 14.35) * mm});
            skLineSegment(sketch, "E745", {"start": v(-30.18, 14.35) * mm, "end": v(-30.07, 14.06) * mm});
            skLineSegment(sketch, "E746", {"start": v(-30.07, 14.06) * mm, "end": v(-29.92, 13.78) * mm});
            skLineSegment(sketch, "E747", {"start": v(-29.92, 13.78) * mm, "end": v(-29.74, 13.53) * mm});
            skLineSegment(sketch, "E748", {"start": v(-29.74, 13.53) * mm, "end": v(-29.53, 13.3) * mm});
            skLineSegment(sketch, "E749", {"start": v(-29.53, 13.3) * mm, "end": v(-29.28, 13.1) * mm});
            skLineSegment(sketch, "E750", {"start": v(-29.28, 13.1) * mm, "end": v(-29.01, 12.92) * mm});
            skLineSegment(sketch, "E751", {"start": v(-9.64, 12.62) * mm, "end": v(-9.48, 12.43) * mm});
            skLineSegment(sketch, "E752", {"start": v(-9.48, 12.43) * mm, "end": v(-9.3, 12.28) * mm});
            skLineSegment(sketch, "E753", {"start": v(-9.3, 12.28) * mm, "end": v(-9.1, 12.16) * mm});
            skLineSegment(sketch, "E754", {"start": v(-9.1, 12.16) * mm, "end": v(-8.87, 12.1) * mm});
            skLineSegment(sketch, "E755", {"start": v(-8.87, 12.1) * mm, "end": v(-8.64, 12.07) * mm});
            skLineSegment(sketch, "E756", {"start": v(-8.64, 12.07) * mm, "end": v(-8.4, 12.09) * mm});
            skLineSegment(sketch, "E757", {"start": v(-8.4, 12.09) * mm, "end": v(-8.18, 12.15) * mm});
            skLineSegment(sketch, "E758", {"start": v(-8.18, 12.15) * mm, "end": v(-7.96, 12.26) * mm});
            skLineSegment(sketch, "E759", {"start": v(-7.96, 12.26) * mm, "end": v(-7.77, 12.42) * mm});
            skLineSegment(sketch, "E760", {"start": v(-7.77, 12.42) * mm, "end": v(-7.62, 12.6) * mm});
            skLineSegment(sketch, "E761", {"start": v(-7.62, 12.6) * mm, "end": v(-7.5, 12.8) * mm});
            skLineSegment(sketch, "E762", {"start": v(-7.5, 12.8) * mm, "end": v(-7.44, 13.03) * mm});
            skLineSegment(sketch, "E763", {"start": v(-7.44, 13.03) * mm, "end": v(-7.41, 13.26) * mm});
            skLineSegment(sketch, "E764", {"start": v(-7.41, 13.26) * mm, "end": v(-7.43, 13.5) * mm});
            skLineSegment(sketch, "E765", {"start": v(-7.43, 13.5) * mm, "end": v(-7.5, 13.72) * mm});
            skLineSegment(sketch, "E766", {"start": v(-7.5, 13.72) * mm, "end": v(-7.6, 13.94) * mm});
            skLineSegment(sketch, "E767", {"start": v(-22.55, 22.36) * mm, "end": v(-22.8, 22.55) * mm});
            skLineSegment(sketch, "E768", {"start": v(-22.8, 22.55) * mm, "end": v(-23.09, 22.7) * mm});
            skLineSegment(sketch, "E769", {"start": v(-23.09, 22.7) * mm, "end": v(-23.38, 22.82) * mm});
            skLineSegment(sketch, "E770", {"start": v(-23.38, 22.82) * mm, "end": v(-23.68, 22.9) * mm});
            skLineSegment(sketch, "E771", {"start": v(-23.68, 22.9) * mm, "end": v(-24, 22.94) * mm});
            skLineSegment(sketch, "E772", {"start": v(-24, 22.94) * mm, "end": v(-24.31, 22.93) * mm});
            skLineSegment(sketch, "E773", {"start": v(-24.31, 22.93) * mm, "end": v(-24.62, 22.89) * mm});
            skLineSegment(sketch, "E774", {"start": v(-24.62, 22.89) * mm, "end": v(-24.93, 22.8) * mm});
            skLineSegment(sketch, "E775", {"start": v(-24.93, 22.8) * mm, "end": v(-25.23, 22.67) * mm});
            skLineSegment(sketch, "E776", {"start": v(-25.23, 22.67) * mm, "end": v(-25.5, 22.5) * mm});
            skLineSegment(sketch, "E777", {"start": v(-25.5, 22.5) * mm, "end": v(-25.75, 22.31) * mm});
            skLineSegment(sketch, "E778", {"start": v(-25.75, 22.31) * mm, "end": v(-25.97, 22.09) * mm});
            skLineSegment(sketch, "E779", {"start": v(-25.97, 22.09) * mm, "end": v(-26.15, 21.83) * mm});
            skLineSegment(sketch, "E780", {"start": v(-26.15, 21.83) * mm, "end": v(-26.3, 21.56) * mm});
            skLineSegment(sketch, "E781", {"start": v(-26.3, 21.56) * mm, "end": v(-26.42, 21.26) * mm});
            skLineSegment(sketch, "E782", {"start": v(-26.42, 21.26) * mm, "end": v(-26.5, 20.95) * mm});
            skLineSegment(sketch, "E783", {"start": v(-26.5, 20.95) * mm, "end": v(-26.54, 20.63) * mm});
            skLineSegment(sketch, "E784", {"start": v(-26.54, 20.63) * mm, "end": v(-26.53, 20.32) * mm});
            skLineSegment(sketch, "E785", {"start": v(-26.53, 20.32) * mm, "end": v(-26.49, 20) * mm});
            skLineSegment(sketch, "E786", {"start": v(-26.49, 20) * mm, "end": v(-26.4, 19.7) * mm});
            skLineSegment(sketch, "E787", {"start": v(-26.4, 19.7) * mm, "end": v(-26.28, 19.41) * mm});
            skLineSegment(sketch, "E788", {"start": v(-26.28, 19.41) * mm, "end": v(-26.12, 19.14) * mm});
            skLineSegment(sketch, "E789", {"start": v(-26.12, 19.14) * mm, "end": v(-25.92, 18.9) * mm});
            skLineSegment(sketch, "E790", {"start": v(-25.92, 18.9) * mm, "end": v(-25.7, 18.67) * mm});
            skLineSegment(sketch, "E791", {"start": v(-6.8, 14.35) * mm, "end": v(-6.7, 14.13) * mm});
            skLineSegment(sketch, "E792", {"start": v(-6.7, 14.13) * mm, "end": v(-6.55, 13.94) * mm});
            skLineSegment(sketch, "E793", {"start": v(-6.55, 13.94) * mm, "end": v(-6.37, 13.79) * mm});
            skLineSegment(sketch, "E794", {"start": v(-6.37, 13.79) * mm, "end": v(-6.17, 13.68) * mm});
            skLineSegment(sketch, "E795", {"start": v(-6.17, 13.68) * mm, "end": v(-5.94, 13.6) * mm});
            skLineSegment(sketch, "E796", {"start": v(-5.94, 13.6) * mm, "end": v(-5.71, 13.57) * mm});
            skLineSegment(sketch, "E797", {"start": v(-5.71, 13.57) * mm, "end": v(-5.47, 13.59) * mm});
            skLineSegment(sketch, "E798", {"start": v(-5.47, 13.59) * mm, "end": v(-5.24, 13.65) * mm});
            skLineSegment(sketch, "E799", {"start": v(-5.24, 13.65) * mm, "end": v(-5.02, 13.76) * mm});
            skLineSegment(sketch, "E800", {"start": v(-5.02, 13.76) * mm, "end": v(-4.83, 13.9) * mm});
            skLineSegment(sketch, "E801", {"start": v(-4.83, 13.9) * mm, "end": v(-4.68, 14.09) * mm});
            skLineSegment(sketch, "E802", {"start": v(-4.68, 14.09) * mm, "end": v(-4.57, 14.29) * mm});
            skLineSegment(sketch, "E803", {"start": v(-4.57, 14.29) * mm, "end": v(-4.5, 14.5) * mm});
            skLineSegment(sketch, "E804", {"start": v(-4.5, 14.5) * mm, "end": v(-4.46, 14.74) * mm});
            skLineSegment(sketch, "E805", {"start": v(-4.46, 14.74) * mm, "end": v(-4.48, 14.98) * mm});
            skLineSegment(sketch, "E806", {"start": v(-4.48, 14.98) * mm, "end": v(-4.54, 15.22) * mm});
            skLineSegment(sketch, "E807", {"start": v(-17.4, 26.56) * mm, "end": v(-17.62, 26.8) * mm});
            skLineSegment(sketch, "E808", {"start": v(-17.62, 26.8) * mm, "end": v(-17.86, 27.01) * mm});
            skLineSegment(sketch, "E809", {"start": v(-17.86, 27.01) * mm, "end": v(-18.12, 27.18) * mm});
            skLineSegment(sketch, "E810", {"start": v(-18.12, 27.18) * mm, "end": v(-18.4, 27.32) * mm});
            skLineSegment(sketch, "E811", {"start": v(-18.4, 27.32) * mm, "end": v(-18.7, 27.42) * mm});
            skLineSegment(sketch, "E812", {"start": v(-18.7, 27.42) * mm, "end": v(-19.01, 27.48) * mm});
            skLineSegment(sketch, "E813", {"start": v(-19.01, 27.48) * mm, "end": v(-19.33, 27.5) * mm});
            skLineSegment(sketch, "E814", {"start": v(-19.33, 27.5) * mm, "end": v(-19.65, 27.48) * mm});
            skLineSegment(sketch, "E815", {"start": v(-19.65, 27.48) * mm, "end": v(-19.96, 27.42) * mm});
            skLineSegment(sketch, "E816", {"start": v(-19.96, 27.42) * mm, "end": v(-20.26, 27.32) * mm});
            skLineSegment(sketch, "E817", {"start": v(-20.26, 27.32) * mm, "end": v(-20.55, 27.18) * mm});
            skLineSegment(sketch, "E818", {"start": v(-20.55, 27.18) * mm, "end": v(-20.8, 27) * mm});
            skLineSegment(sketch, "E819", {"start": v(-20.8, 27) * mm, "end": v(-21.04, 26.8) * mm});
            skLineSegment(sketch, "E820", {"start": v(-21.04, 26.8) * mm, "end": v(-21.25, 26.56) * mm});
            skLineSegment(sketch, "E821", {"start": v(-21.25, 26.56) * mm, "end": v(-21.43, 26.3) * mm});
            skLineSegment(sketch, "E822", {"start": v(-21.43, 26.3) * mm, "end": v(-21.57, 26) * mm});
            skLineSegment(sketch, "E823", {"start": v(-21.57, 26) * mm, "end": v(-21.67, 25.7) * mm});
            skLineSegment(sketch, "E824", {"start": v(-21.67, 25.7) * mm, "end": v(-21.73, 25.39) * mm});
            skLineSegment(sketch, "E825", {"start": v(-21.73, 25.39) * mm, "end": v(-21.75, 25.07) * mm});
            skLineSegment(sketch, "E826", {"start": v(-21.75, 25.07) * mm, "end": v(-21.73, 24.76) * mm});
            skLineSegment(sketch, "E827", {"start": v(-21.73, 24.76) * mm, "end": v(-21.67, 24.45) * mm});
            skLineSegment(sketch, "E828", {"start": v(-21.67, 24.45) * mm, "end": v(-21.57, 24.16) * mm});
            skLineSegment(sketch, "E829", {"start": v(-21.57, 24.16) * mm, "end": v(-21.43, 23.87) * mm});
            skLineSegment(sketch, "E830", {"start": v(-21.43, 23.87) * mm, "end": v(-21.25, 23.6) * mm});
            skLineSegment(sketch, "E831", {"start": v(-3.67, 15.45) * mm, "end": v(-3.6, 15.21) * mm});
            skLineSegment(sketch, "E832", {"start": v(-3.6, 15.21) * mm, "end": v(-3.5, 15) * mm});
            skLineSegment(sketch, "E833", {"start": v(-3.5, 15) * mm, "end": v(-3.36, 14.81) * mm});
            skLineSegment(sketch, "E834", {"start": v(-3.36, 14.81) * mm, "end": v(-3.19, 14.66) * mm});
            skLineSegment(sketch, "E835", {"start": v(-3.19, 14.66) * mm, "end": v(-2.99, 14.54) * mm});
            skLineSegment(sketch, "E836", {"start": v(-2.99, 14.54) * mm, "end": v(-2.77, 14.46) * mm});
            skLineSegment(sketch, "E837", {"start": v(-2.77, 14.46) * mm, "end": v(-2.53, 14.43) * mm});
            skLineSegment(sketch, "E838", {"start": v(-2.53, 14.43) * mm, "end": v(-2.29, 14.44) * mm});
            skLineSegment(sketch, "E839", {"start": v(-2.29, 14.44) * mm, "end": v(-2.05, 14.5) * mm});
            skLineSegment(sketch, "E840", {"start": v(-2.05, 14.5) * mm, "end": v(-1.83, 14.6) * mm});
            skLineSegment(sketch, "E841", {"start": v(-1.83, 14.6) * mm, "end": v(-1.65, 14.75) * mm});
            skLineSegment(sketch, "E842", {"start": v(-1.65, 14.75) * mm, "end": v(-1.5, 14.93) * mm});
            skLineSegment(sketch, "E843", {"start": v(-1.5, 14.93) * mm, "end": v(-1.38, 15.13) * mm});
            skLineSegment(sketch, "E844", {"start": v(-1.38, 15.13) * mm, "end": v(-1.3, 15.35) * mm});
            skLineSegment(sketch, "E845", {"start": v(-1.3, 15.35) * mm, "end": v(-1.26, 15.58) * mm});
            skLineSegment(sketch, "E846", {"start": v(-1.26, 15.58) * mm, "end": v(-1.28, 15.83) * mm});
            skLineSegment(sketch, "E847", {"start": v(-11.5, 29.6) * mm, "end": v(-11.66, 29.88) * mm});
            skLineSegment(sketch, "E848", {"start": v(-11.66, 29.88) * mm, "end": v(-11.86, 30.13) * mm});
            skLineSegment(sketch, "E849", {"start": v(-11.86, 30.13) * mm, "end": v(-12.08, 30.36) * mm});
            skLineSegment(sketch, "E850", {"start": v(-12.08, 30.36) * mm, "end": v(-12.32, 30.55) * mm});
            skLineSegment(sketch, "E851", {"start": v(-12.32, 30.55) * mm, "end": v(-12.6, 30.71) * mm});
            skLineSegment(sketch, "E852", {"start": v(-12.6, 30.71) * mm, "end": v(-12.88, 30.84) * mm});
            skLineSegment(sketch, "E853", {"start": v(-12.88, 30.84) * mm, "end": v(-13.19, 30.92) * mm});
            skLineSegment(sketch, "E854", {"start": v(-13.19, 30.92) * mm, "end": v(-13.5, 30.97) * mm});
            skLineSegment(sketch, "E855", {"start": v(-13.5, 30.97) * mm, "end": v(-13.83, 30.97) * mm});
            skLineSegment(sketch, "E856", {"start": v(-13.83, 30.97) * mm, "end": v(-14.14, 30.93) * mm});
            skLineSegment(sketch, "E857", {"start": v(-14.14, 30.93) * mm, "end": v(-14.45, 30.85) * mm});
            skLineSegment(sketch, "E858", {"start": v(-14.45, 30.85) * mm, "end": v(-14.74, 30.74) * mm});
            skLineSegment(sketch, "E859", {"start": v(-14.74, 30.74) * mm, "end": v(-15.01, 30.58) * mm});
            skLineSegment(sketch, "E860", {"start": v(-15.01, 30.58) * mm, "end": v(-15.26, 30.4) * mm});
            skLineSegment(sketch, "E861", {"start": v(-15.26, 30.4) * mm, "end": v(-15.5, 30.17) * mm});
            skLineSegment(sketch, "E862", {"start": v(-15.5, 30.17) * mm, "end": v(-15.7, 29.92) * mm});
            skLineSegment(sketch, "E863", {"start": v(-15.7, 29.92) * mm, "end": v(-15.85, 29.64) * mm});
            skLineSegment(sketch, "E864", {"start": v(-15.85, 29.64) * mm, "end": v(-15.98, 29.35) * mm});
            skLineSegment(sketch, "E865", {"start": v(-15.98, 29.35) * mm, "end": v(-16.06, 29.05) * mm});
            skLineSegment(sketch, "E866", {"start": v(-16.06, 29.05) * mm, "end": v(-16.1, 28.74) * mm});
            skLineSegment(sketch, "E867", {"start": v(-16.1, 28.74) * mm, "end": v(-16.1, 28.42) * mm});
            skLineSegment(sketch, "E868", {"start": v(-16.1, 28.42) * mm, "end": v(-16.07, 28.11) * mm});
            skLineSegment(sketch, "E869", {"start": v(-16.07, 28.11) * mm, "end": v(-16, 27.8) * mm});
            skLineSegment(sketch, "E870", {"start": v(-16, 27.8) * mm, "end": v(-15.88, 27.5) * mm});
            skLineSegment(sketch, "E871", {"start": v(-0.38, 15.88) * mm, "end": v(-0.38, 15.71) * mm});
            skLineSegment(sketch, "E872", {"start": v(-0.38, 15.71) * mm, "end": v(-0.35, 15.56) * mm});
            skLineSegment(sketch, "E873", {"start": v(-0.35, 15.56) * mm, "end": v(-0.31, 15.4) * mm});
            skLineSegment(sketch, "E874", {"start": v(-0.31, 15.4) * mm, "end": v(-0.25, 15.26) * mm});
            skLineSegment(sketch, "E875", {"start": v(-0.25, 15.26) * mm, "end": v(-0.17, 15.13) * mm});
            skLineSegment(sketch, "E876", {"start": v(-0.17, 15.13) * mm, "end": v(-0.07, 15) * mm});
            skLineSegment(sketch, "E877", {"start": v(-0.07, 15) * mm, "end": v(0.04, 14.9) * mm});
            skLineSegment(sketch, "E878", {"start": v(0.04, 14.9) * mm, "end": v(0.17, 14.8) * mm});
            skLineSegment(sketch, "E879", {"start": v(0.17, 14.8) * mm, "end": v(0.31, 14.72) * mm});
            skLineSegment(sketch, "E880", {"start": v(0.31, 14.72) * mm, "end": v(0.46, 14.66) * mm});
            skLineSegment(sketch, "E881", {"start": v(0.46, 14.66) * mm, "end": v(0.61, 14.62) * mm});
            skLineSegment(sketch, "E882", {"start": v(0.61, 14.62) * mm, "end": v(0.77, 14.6) * mm});
            skLineSegment(sketch, "E883", {"start": v(0.77, 14.6) * mm, "end": v(0.92, 14.6) * mm});
            skLineSegment(sketch, "E884", {"start": v(0.92, 14.6) * mm, "end": v(1.08, 14.63) * mm});
            skLineSegment(sketch, "E885", {"start": v(1.08, 14.63) * mm, "end": v(1.23, 14.67) * mm});
            skLineSegment(sketch, "E886", {"start": v(1.23, 14.67) * mm, "end": v(1.38, 14.73) * mm});
            skLineSegment(sketch, "E887", {"start": v(1.38, 14.73) * mm, "end": v(1.52, 14.81) * mm});
            skLineSegment(sketch, "E888", {"start": v(1.52, 14.81) * mm, "end": v(1.64, 14.91) * mm});
            skLineSegment(sketch, "E889", {"start": v(1.64, 14.91) * mm, "end": v(1.75, 15.03) * mm});
            skLineSegment(sketch, "E890", {"start": v(1.75, 15.03) * mm, "end": v(1.85, 15.15) * mm});
            skLineSegment(sketch, "E891", {"start": v(1.85, 15.15) * mm, "end": v(1.92, 15.29) * mm});
            skLineSegment(sketch, "E892", {"start": v(1.92, 15.29) * mm, "end": v(1.98, 15.43) * mm});
            skLineSegment(sketch, "E893", {"start": v(1.98, 15.43) * mm, "end": v(2.02, 15.59) * mm});
            skLineSegment(sketch, "E894", {"start": v(2.02, 15.59) * mm, "end": v(2.04, 15.75) * mm});
            skLineSegment(sketch, "E895", {"start": v(-5.1, 31.35) * mm, "end": v(-5.2, 31.65) * mm});
            skLineSegment(sketch, "E896", {"start": v(-5.2, 31.65) * mm, "end": v(-5.33, 31.94) * mm});
            skLineSegment(sketch, "E897", {"start": v(-5.33, 31.94) * mm, "end": v(-5.5, 32.2) * mm});
            skLineSegment(sketch, "E898", {"start": v(-5.5, 32.2) * mm, "end": v(-5.7, 32.45) * mm});
            skLineSegment(sketch, "E899", {"start": v(-5.7, 32.45) * mm, "end": v(-5.93, 32.66) * mm});
            skLineSegment(sketch, "E900", {"start": v(-5.93, 32.66) * mm, "end": v(-6.19, 32.84) * mm});
            skLineSegment(sketch, "E901", {"start": v(-6.19, 32.84) * mm, "end": v(-6.47, 32.99) * mm});
            skLineSegment(sketch, "E902", {"start": v(-6.47, 32.99) * mm, "end": v(-6.77, 33.1) * mm});
            skLineSegment(sketch, "E903", {"start": v(-6.77, 33.1) * mm, "end": v(-7.09, 33.17) * mm});
            skLineSegment(sketch, "E904", {"start": v(-7.09, 33.17) * mm, "end": v(-7.4, 33.2) * mm});
            skLineSegment(sketch, "E905", {"start": v(-7.4, 33.2) * mm, "end": v(-7.72, 33.18) * mm});
            skLineSegment(sketch, "E906", {"start": v(-7.72, 33.18) * mm, "end": v(-8.03, 33.13) * mm});
            skLineSegment(sketch, "E907", {"start": v(-8.03, 33.13) * mm, "end": v(-8.32, 33.04) * mm});
            skLineSegment(sketch, "E908", {"start": v(-8.32, 33.04) * mm, "end": v(-8.61, 32.9) * mm});
            skLineSegment(sketch, "E909", {"start": v(-8.61, 32.9) * mm, "end": v(-8.88, 32.74) * mm});
            skLineSegment(sketch, "E910", {"start": v(-8.88, 32.74) * mm, "end": v(-9.13, 32.53) * mm});
            skLineSegment(sketch, "E911", {"start": v(-9.13, 32.53) * mm, "end": v(-9.34, 32.3) * mm});
            skLineSegment(sketch, "E912", {"start": v(-9.34, 32.3) * mm, "end": v(-9.53, 32.03) * mm});
            skLineSegment(sketch, "E913", {"start": v(-9.53, 32.03) * mm, "end": v(-9.67, 31.75) * mm});
            skLineSegment(sketch, "E914", {"start": v(-9.67, 31.75) * mm, "end": v(-9.78, 31.46) * mm});
            skLineSegment(sketch, "E915", {"start": v(-9.78, 31.46) * mm, "end": v(-9.85, 31.15) * mm});
            skLineSegment(sketch, "E916", {"start": v(-9.85, 31.15) * mm, "end": v(-9.88, 30.84) * mm});
            skLineSegment(sketch, "E917", {"start": v(-9.88, 30.84) * mm, "end": v(-9.86, 30.52) * mm});
            skLineSegment(sketch, "E918", {"start": v(-9.86, 30.52) * mm, "end": v(-9.8, 30.2) * mm});
            skLineSegment(sketch, "E919", {"start": v(2.93, 15.6) * mm, "end": v(2.9, 15.45) * mm});
            skLineSegment(sketch, "E920", {"start": v(2.9, 15.45) * mm, "end": v(2.89, 15.3) * mm});
            skLineSegment(sketch, "E921", {"start": v(2.89, 15.3) * mm, "end": v(2.9, 15.13) * mm});
            skLineSegment(sketch, "E922", {"start": v(2.9, 15.13) * mm, "end": v(2.93, 14.98) * mm});
            skLineSegment(sketch, "E923", {"start": v(2.93, 14.98) * mm, "end": v(2.98, 14.83) * mm});
            skLineSegment(sketch, "E924", {"start": v(2.98, 14.83) * mm, "end": v(3.05, 14.7) * mm});
            skLineSegment(sketch, "E925", {"start": v(3.05, 14.7) * mm, "end": v(3.14, 14.56) * mm});
            skLineSegment(sketch, "E926", {"start": v(3.14, 14.56) * mm, "end": v(3.24, 14.44) * mm});
            skLineSegment(sketch, "E927", {"start": v(3.24, 14.44) * mm, "end": v(3.36, 14.33) * mm});
            skLineSegment(sketch, "E928", {"start": v(3.36, 14.33) * mm, "end": v(3.5, 14.24) * mm});
            skLineSegment(sketch, "E929", {"start": v(3.5, 14.24) * mm, "end": v(3.64, 14.17) * mm});
            skLineSegment(sketch, "E930", {"start": v(3.64, 14.17) * mm, "end": v(3.79, 14.12) * mm});
            skLineSegment(sketch, "E931", {"start": v(3.79, 14.12) * mm, "end": v(3.94, 14.1) * mm});
            skLineSegment(sketch, "E932", {"start": v(3.94, 14.1) * mm, "end": v(4.1, 14.08) * mm});
            skLineSegment(sketch, "E933", {"start": v(4.1, 14.08) * mm, "end": v(4.26, 14.1) * mm});
            skLineSegment(sketch, "E934", {"start": v(4.26, 14.1) * mm, "end": v(4.41, 14.12) * mm});
            skLineSegment(sketch, "E935", {"start": v(4.41, 14.12) * mm, "end": v(4.57, 14.18) * mm});
            skLineSegment(sketch, "E936", {"start": v(4.57, 14.18) * mm, "end": v(4.7, 14.25) * mm});
            skLineSegment(sketch, "E937", {"start": v(4.7, 14.25) * mm, "end": v(4.84, 14.33) * mm});
            skLineSegment(sketch, "E938", {"start": v(4.84, 14.33) * mm, "end": v(4.96, 14.44) * mm});
            skLineSegment(sketch, "E939", {"start": v(4.96, 14.44) * mm, "end": v(5.06, 14.56) * mm});
            skLineSegment(sketch, "E940", {"start": v(5.06, 14.56) * mm, "end": v(5.15, 14.69) * mm});
            skLineSegment(sketch, "E941", {"start": v(5.15, 14.69) * mm, "end": v(5.22, 14.83) * mm});
            skLineSegment(sketch, "E942", {"start": v(5.22, 14.83) * mm, "end": v(5.27, 14.98) * mm});
            skLineSegment(sketch, "E943", {"start": v(1.53, 31.72) * mm, "end": v(1.5, 32.04) * mm});
            skLineSegment(sketch, "E944", {"start": v(1.5, 32.04) * mm, "end": v(1.43, 32.35) * mm});
            skLineSegment(sketch, "E945", {"start": v(1.43, 32.35) * mm, "end": v(1.32, 32.65) * mm});
            skLineSegment(sketch, "E946", {"start": v(1.32, 32.65) * mm, "end": v(1.17, 32.92) * mm});
            skLineSegment(sketch, "E947", {"start": v(1.17, 32.92) * mm, "end": v(0.99, 33.18) * mm});
            skLineSegment(sketch, "E948", {"start": v(0.99, 33.18) * mm, "end": v(0.77, 33.41) * mm});
            skLineSegment(sketch, "E949", {"start": v(0.77, 33.41) * mm, "end": v(0.53, 33.61) * mm});
            skLineSegment(sketch, "E950", {"start": v(0.53, 33.61) * mm, "end": v(0.26, 33.79) * mm});
            skLineSegment(sketch, "E951", {"start": v(0.26, 33.79) * mm, "end": v(-0.03, 33.92) * mm});
            skLineSegment(sketch, "E952", {"start": v(-0.03, 33.92) * mm, "end": v(-0.34, 34.01) * mm});
            skLineSegment(sketch, "E953", {"start": v(-0.34, 34.01) * mm, "end": v(-0.65, 34.06) * mm});
            skLineSegment(sketch, "E954", {"start": v(-0.65, 34.06) * mm, "end": v(-0.96, 34.08) * mm});
            skLineSegment(sketch, "E955", {"start": v(-0.96, 34.08) * mm, "end": v(-1.27, 34.05) * mm});
            skLineSegment(sketch, "E956", {"start": v(-1.27, 34.05) * mm, "end": v(-1.58, 33.98) * mm});
            skLineSegment(sketch, "E957", {"start": v(-1.58, 33.98) * mm, "end": v(-1.88, 33.87) * mm});
            skLineSegment(sketch, "E958", {"start": v(-1.88, 33.87) * mm, "end": v(-2.16, 33.72) * mm});
            skLineSegment(sketch, "E959", {"start": v(-2.16, 33.72) * mm, "end": v(-2.43, 33.53) * mm});
            skLineSegment(sketch, "E960", {"start": v(-2.43, 33.53) * mm, "end": v(-2.66, 33.31) * mm});
            skLineSegment(sketch, "E961", {"start": v(-2.66, 33.31) * mm, "end": v(-2.86, 33.07) * mm});
            skLineSegment(sketch, "E962", {"start": v(-2.86, 33.07) * mm, "end": v(-3.02, 32.8) * mm});
            skLineSegment(sketch, "E963", {"start": v(-3.02, 32.8) * mm, "end": v(-3.16, 32.52) * mm});
            skLineSegment(sketch, "E964", {"start": v(-3.16, 32.52) * mm, "end": v(-3.25, 32.22) * mm});
            skLineSegment(sketch, "E965", {"start": v(-3.25, 32.22) * mm, "end": v(-3.3, 31.9) * mm});
            skLineSegment(sketch, "E966", {"start": v(-3.3, 31.9) * mm, "end": v(-3.31, 31.59) * mm});
            skLineSegment(sketch, "E967", {"start": v(6.11, 14.66) * mm, "end": v(6.05, 14.5) * mm});
            skLineSegment(sketch, "E968", {"start": v(6.05, 14.5) * mm, "end": v(6, 14.36) * mm});
            skLineSegment(sketch, "E969", {"start": v(6, 14.36) * mm, "end": v(5.98, 14.2) * mm});
            skLineSegment(sketch, "E970", {"start": v(5.98, 14.2) * mm, "end": v(5.98, 14.04) * mm});
            skLineSegment(sketch, "E971", {"start": v(5.98, 14.04) * mm, "end": v(6, 13.89) * mm});
            skLineSegment(sketch, "E972", {"start": v(6, 13.89) * mm, "end": v(6.04, 13.74) * mm});
            skLineSegment(sketch, "E973", {"start": v(6.04, 13.74) * mm, "end": v(6.1, 13.59) * mm});
            skLineSegment(sketch, "E974", {"start": v(6.1, 13.59) * mm, "end": v(6.17, 13.45) * mm});
            skLineSegment(sketch, "E975", {"start": v(6.17, 13.45) * mm, "end": v(6.27, 13.32) * mm});
            skLineSegment(sketch, "E976", {"start": v(6.27, 13.32) * mm, "end": v(6.38, 13.2) * mm});
            skLineSegment(sketch, "E977", {"start": v(6.38, 13.2) * mm, "end": v(6.5, 13.1) * mm});
            skLineSegment(sketch, "E978", {"start": v(6.5, 13.1) * mm, "end": v(6.64, 13.03) * mm});
            skLineSegment(sketch, "E979", {"start": v(6.64, 13.03) * mm, "end": v(6.78, 12.97) * mm});
            skLineSegment(sketch, "E980", {"start": v(6.78, 12.97) * mm, "end": v(6.94, 12.92) * mm});
            skLineSegment(sketch, "E981", {"start": v(6.94, 12.92) * mm, "end": v(7.1, 12.9) * mm});
            skLineSegment(sketch, "E982", {"start": v(7.1, 12.9) * mm, "end": v(7.25, 12.9) * mm});
            skLineSegment(sketch, "E983", {"start": v(7.25, 12.9) * mm, "end": v(7.41, 12.92) * mm});
            skLineSegment(sketch, "E984", {"start": v(7.41, 12.92) * mm, "end": v(7.57, 12.96) * mm});
            skLineSegment(sketch, "E985", {"start": v(7.57, 12.96) * mm, "end": v(7.71, 13.02) * mm});
            skLineSegment(sketch, "E986", {"start": v(7.71, 13.02) * mm, "end": v(7.85, 13.1) * mm});
            skLineSegment(sketch, "E987", {"start": v(7.85, 13.1) * mm, "end": v(7.98, 13.19) * mm});
            skLineSegment(sketch, "E988", {"start": v(7.98, 13.19) * mm, "end": v(8.09, 13.3) * mm});
            skLineSegment(sketch, "E989", {"start": v(8.09, 13.3) * mm, "end": v(8.19, 13.42) * mm});
            skLineSegment(sketch, "E990", {"start": v(8.19, 13.42) * mm, "end": v(8.27, 13.56) * mm});
            skLineSegment(sketch, "E991", {"start": v(8.1, 30.71) * mm, "end": v(8.13, 31.2) * mm});
            skLineSegment(sketch, "E992", {"start": v(8.13, 31.2) * mm, "end": v(8.07, 31.67) * mm});
            skLineSegment(sketch, "E993", {"start": v(8.07, 31.67) * mm, "end": v(7.93, 32.12) * mm});
            skLineSegment(sketch, "E994", {"start": v(7.93, 32.12) * mm, "end": v(7.7, 32.52) * mm});
            skLineSegment(sketch, "E995", {"start": v(7.7, 32.52) * mm, "end": v(7.4, 32.88) * mm});
            skLineSegment(sketch, "E996", {"start": v(7.4, 32.88) * mm, "end": v(7.04, 33.17) * mm});
            skLineSegment(sketch, "E997", {"start": v(7.04, 33.17) * mm, "end": v(6.62, 33.4) * mm});
            skLineSegment(sketch, "E998", {"start": v(6.62, 33.4) * mm, "end": v(6.14, 33.53) * mm});
            skLineSegment(sketch, "E999", {"start": v(6.14, 33.53) * mm, "end": v(5.66, 33.57) * mm});
            skLineSegment(sketch, "E1000", {"start": v(5.66, 33.57) * mm, "end": v(5.18, 33.51) * mm});
            skLineSegment(sketch, "E1001", {"start": v(5.18, 33.51) * mm, "end": v(4.74, 33.37) * mm});
            skLineSegment(sketch, "E1002", {"start": v(4.74, 33.37) * mm, "end": v(4.33, 33.14) * mm});
            skLineSegment(sketch, "E1003", {"start": v(4.33, 33.14) * mm, "end": v(3.98, 32.84) * mm});
            skLineSegment(sketch, "E1004", {"start": v(3.98, 32.84) * mm, "end": v(3.68, 32.48) * mm});
            skLineSegment(sketch, "E1005", {"start": v(3.68, 32.48) * mm, "end": v(3.46, 32.06) * mm});
            skLineSegment(sketch, "E1006", {"start": v(3.46, 32.06) * mm, "end": v(3.32, 31.59) * mm});
            skLineSegment(sketch, "E1007", {"start": v(9.02, 13.07) * mm, "end": v(8.93, 12.94) * mm});
            skLineSegment(sketch, "E1008", {"start": v(8.93, 12.94) * mm, "end": v(8.86, 12.8) * mm});
            skLineSegment(sketch, "E1009", {"start": v(8.86, 12.8) * mm, "end": v(8.8, 12.65) * mm});
            skLineSegment(sketch, "E1010", {"start": v(8.8, 12.65) * mm, "end": v(8.77, 12.5) * mm});
            skLineSegment(sketch, "E1011", {"start": v(8.77, 12.5) * mm, "end": v(8.76, 12.34) * mm});
            skLineSegment(sketch, "E1012", {"start": v(8.76, 12.34) * mm, "end": v(8.76, 12.18) * mm});
            skLineSegment(sketch, "E1013", {"start": v(8.76, 12.18) * mm, "end": v(8.79, 12.02) * mm});
            skLineSegment(sketch, "E1014", {"start": v(8.79, 12.02) * mm, "end": v(8.84, 11.87) * mm});
            skLineSegment(sketch, "E1015", {"start": v(8.84, 11.87) * mm, "end": v(8.9, 11.72) * mm});
            skLineSegment(sketch, "E1016", {"start": v(8.9, 11.72) * mm, "end": v(8.99, 11.6) * mm});
            skLineSegment(sketch, "E1017", {"start": v(8.99, 11.6) * mm, "end": v(9.09, 11.47) * mm});
            skLineSegment(sketch, "E1018", {"start": v(9.09, 11.47) * mm, "end": v(9.2, 11.36) * mm});
            skLineSegment(sketch, "E1019", {"start": v(9.2, 11.36) * mm, "end": v(9.33, 11.27) * mm});
            skLineSegment(sketch, "E1020", {"start": v(9.33, 11.27) * mm, "end": v(9.47, 11.2) * mm});
            skLineSegment(sketch, "E1021", {"start": v(9.47, 11.2) * mm, "end": v(9.62, 11.14) * mm});
            skLineSegment(sketch, "E1022", {"start": v(9.62, 11.14) * mm, "end": v(9.78, 11.1) * mm});
            skLineSegment(sketch, "E1023", {"start": v(9.78, 11.1) * mm, "end": v(9.94, 11.1) * mm});
            skLineSegment(sketch, "E1024", {"start": v(9.94, 11.1) * mm, "end": v(10.1, 11.1) * mm});
            skLineSegment(sketch, "E1025", {"start": v(10.1, 11.1) * mm, "end": v(10.25, 11.13) * mm});
            skLineSegment(sketch, "E1026", {"start": v(10.25, 11.13) * mm, "end": v(10.4, 11.17) * mm});
            skLineSegment(sketch, "E1027", {"start": v(10.4, 11.17) * mm, "end": v(10.54, 11.24) * mm});
            skLineSegment(sketch, "E1028", {"start": v(10.54, 11.24) * mm, "end": v(10.68, 11.32) * mm});
            skLineSegment(sketch, "E1029", {"start": v(10.68, 11.32) * mm, "end": v(10.8, 11.42) * mm});
            skLineSegment(sketch, "E1030", {"start": v(10.8, 11.42) * mm, "end": v(10.9, 11.54) * mm});
            skLineSegment(sketch, "E1031", {"start": v(14.3, 28.36) * mm, "end": v(14.44, 28.83) * mm});
            skLineSegment(sketch, "E1032", {"start": v(14.44, 28.83) * mm, "end": v(14.48, 29.3) * mm});
            skLineSegment(sketch, "E1033", {"start": v(14.48, 29.3) * mm, "end": v(14.43, 29.77) * mm});
            skLineSegment(sketch, "E1034", {"start": v(14.43, 29.77) * mm, "end": v(14.3, 30.21) * mm});
            skLineSegment(sketch, "E1035", {"start": v(14.3, 30.21) * mm, "end": v(14.08, 30.62) * mm});
            skLineSegment(sketch, "E1036", {"start": v(14.08, 30.62) * mm, "end": v(13.78, 30.99) * mm});
            skLineSegment(sketch, "E1037", {"start": v(13.78, 30.99) * mm, "end": v(13.41, 31.3) * mm});
            skLineSegment(sketch, "E1038", {"start": v(13.41, 31.3) * mm, "end": v(12.98, 31.52) * mm});
            skLineSegment(sketch, "E1039", {"start": v(12.98, 31.52) * mm, "end": v(12.51, 31.66) * mm});
            skLineSegment(sketch, "E1040", {"start": v(12.51, 31.66) * mm, "end": v(12.04, 31.7) * mm});
            skLineSegment(sketch, "E1041", {"start": v(12.04, 31.7) * mm, "end": v(11.57, 31.65) * mm});
            skLineSegment(sketch, "E1042", {"start": v(11.57, 31.65) * mm, "end": v(11.13, 31.52) * mm});
            skLineSegment(sketch, "E1043", {"start": v(11.13, 31.52) * mm, "end": v(10.72, 31.3) * mm});
            skLineSegment(sketch, "E1044", {"start": v(10.72, 31.3) * mm, "end": v(10.35, 31) * mm});
            skLineSegment(sketch, "E1045", {"start": v(10.35, 31) * mm, "end": v(10.05, 30.64) * mm});
            skLineSegment(sketch, "E1046", {"start": v(10.05, 30.64) * mm, "end": v(9.82, 30.2) * mm});
            skLineSegment(sketch, "E1047", {"start": v(11.54, 10.9) * mm, "end": v(11.43, 10.8) * mm});
            skLineSegment(sketch, "E1048", {"start": v(11.43, 10.8) * mm, "end": v(11.33, 10.67) * mm});
            skLineSegment(sketch, "E1049", {"start": v(11.33, 10.67) * mm, "end": v(11.24, 10.54) * mm});
            skLineSegment(sketch, "E1050", {"start": v(11.24, 10.54) * mm, "end": v(11.18, 10.4) * mm});
            skLineSegment(sketch, "E1051", {"start": v(11.18, 10.4) * mm, "end": v(11.13, 10.25) * mm});
            skLineSegment(sketch, "E1052", {"start": v(11.13, 10.25) * mm, "end": v(11.1, 10.1) * mm});
            skLineSegment(sketch, "E1053", {"start": v(11.1, 10.1) * mm, "end": v(11.1, 9.93) * mm});
            skLineSegment(sketch, "E1054", {"start": v(11.1, 9.93) * mm, "end": v(11.11, 9.77) * mm});
            skLineSegment(sketch, "E1055", {"start": v(11.11, 9.77) * mm, "end": v(11.15, 9.62) * mm});
            skLineSegment(sketch, "E1056", {"start": v(11.15, 9.62) * mm, "end": v(11.2, 9.47) * mm});
            skLineSegment(sketch, "E1057", {"start": v(11.2, 9.47) * mm, "end": v(11.27, 9.33) * mm});
            skLineSegment(sketch, "E1058", {"start": v(11.27, 9.33) * mm, "end": v(11.37, 9.2) * mm});
            skLineSegment(sketch, "E1059", {"start": v(11.37, 9.2) * mm, "end": v(11.47, 9.09) * mm});
            skLineSegment(sketch, "E1060", {"start": v(11.47, 9.09) * mm, "end": v(11.6, 8.99) * mm});
            skLineSegment(sketch, "E1061", {"start": v(11.6, 8.99) * mm, "end": v(11.73, 8.9) * mm});
            skLineSegment(sketch, "E1062", {"start": v(11.73, 8.9) * mm, "end": v(11.87, 8.83) * mm});
            skLineSegment(sketch, "E1063", {"start": v(11.87, 8.83) * mm, "end": v(12.03, 8.79) * mm});
            skLineSegment(sketch, "E1064", {"start": v(12.03, 8.79) * mm, "end": v(12.18, 8.76) * mm});
            skLineSegment(sketch, "E1065", {"start": v(12.18, 8.76) * mm, "end": v(12.34, 8.75) * mm});
            skLineSegment(sketch, "E1066", {"start": v(12.34, 8.75) * mm, "end": v(12.5, 8.77) * mm});
            skLineSegment(sketch, "E1067", {"start": v(12.5, 8.77) * mm, "end": v(12.65, 8.8) * mm});
            skLineSegment(sketch, "E1068", {"start": v(12.65, 8.8) * mm, "end": v(12.8, 8.86) * mm});
            skLineSegment(sketch, "E1069", {"start": v(12.8, 8.86) * mm, "end": v(12.94, 8.93) * mm});
            skLineSegment(sketch, "E1070", {"start": v(12.94, 8.93) * mm, "end": v(13.07, 9.02) * mm});
            skLineSegment(sketch, "E1071", {"start": v(19.88, 24.77) * mm, "end": v(20.12, 25.2) * mm});
            skLineSegment(sketch, "E1072", {"start": v(20.12, 25.2) * mm, "end": v(20.26, 25.65) * mm});
            skLineSegment(sketch, "E1073", {"start": v(20.26, 25.65) * mm, "end": v(20.3, 26.12) * mm});
            skLineSegment(sketch, "E1074", {"start": v(20.3, 26.12) * mm, "end": v(20.26, 26.58) * mm});
            skLineSegment(sketch, "E1075", {"start": v(20.26, 26.58) * mm, "end": v(20.14, 27.03) * mm});
            skLineSegment(sketch, "E1076", {"start": v(20.14, 27.03) * mm, "end": v(19.92, 27.44) * mm});
            skLineSegment(sketch, "E1077", {"start": v(19.92, 27.44) * mm, "end": v(19.63, 27.82) * mm});
            skLineSegment(sketch, "E1078", {"start": v(19.63, 27.82) * mm, "end": v(19.25, 28.13) * mm});
            skLineSegment(sketch, "E1079", {"start": v(19.25, 28.13) * mm, "end": v(18.82, 28.37) * mm});
            skLineSegment(sketch, "E1080", {"start": v(18.82, 28.37) * mm, "end": v(18.37, 28.5) * mm});
            skLineSegment(sketch, "E1081", {"start": v(18.37, 28.5) * mm, "end": v(17.9, 28.56) * mm});
            skLineSegment(sketch, "E1082", {"start": v(17.9, 28.56) * mm, "end": v(17.44, 28.52) * mm});
            skLineSegment(sketch, "E1083", {"start": v(17.44, 28.52) * mm, "end": v(17, 28.39) * mm});
            skLineSegment(sketch, "E1084", {"start": v(17, 28.39) * mm, "end": v(16.57, 28.17) * mm});
            skLineSegment(sketch, "E1085", {"start": v(16.57, 28.17) * mm, "end": v(16.2, 27.88) * mm});
            skLineSegment(sketch, "E1086", {"start": v(16.2, 27.88) * mm, "end": v(15.88, 27.5) * mm});
            skLineSegment(sketch, "E1087", {"start": v(13.56, 8.27) * mm, "end": v(13.42, 8.19) * mm});
            skLineSegment(sketch, "E1088", {"start": v(13.42, 8.19) * mm, "end": v(13.3, 8.09) * mm});
            skLineSegment(sketch, "E1089", {"start": v(13.3, 8.09) * mm, "end": v(13.19, 7.97) * mm});
            skLineSegment(sketch, "E1090", {"start": v(13.19, 7.97) * mm, "end": v(13.1, 7.85) * mm});
            skLineSegment(sketch, "E1091", {"start": v(13.1, 7.85) * mm, "end": v(13.02, 7.71) * mm});
            skLineSegment(sketch, "E1092", {"start": v(13.02, 7.71) * mm, "end": v(12.96, 7.57) * mm});
            skLineSegment(sketch, "E1093", {"start": v(12.96, 7.57) * mm, "end": v(12.92, 7.41) * mm});
            skLineSegment(sketch, "E1094", {"start": v(12.92, 7.41) * mm, "end": v(12.9, 7.25) * mm});
            skLineSegment(sketch, "E1095", {"start": v(12.9, 7.25) * mm, "end": v(12.9, 7.1) * mm});
            skLineSegment(sketch, "E1096", {"start": v(12.9, 7.1) * mm, "end": v(12.93, 6.93) * mm});
            skLineSegment(sketch, "E1097", {"start": v(12.93, 6.93) * mm, "end": v(12.97, 6.78) * mm});
            skLineSegment(sketch, "E1098", {"start": v(12.97, 6.78) * mm, "end": v(13.03, 6.64) * mm});
            skLineSegment(sketch, "E1099", {"start": v(13.03, 6.64) * mm, "end": v(13.11, 6.5) * mm});
            skLineSegment(sketch, "E1100", {"start": v(13.11, 6.5) * mm, "end": v(13.2, 6.38) * mm});
            skLineSegment(sketch, "E1101", {"start": v(13.2, 6.38) * mm, "end": v(13.32, 6.27) * mm});
            skLineSegment(sketch, "E1102", {"start": v(13.32, 6.27) * mm, "end": v(13.45, 6.17) * mm});
            skLineSegment(sketch, "E1103", {"start": v(13.45, 6.17) * mm, "end": v(13.6, 6.1) * mm});
            skLineSegment(sketch, "E1104", {"start": v(13.6, 6.1) * mm, "end": v(13.74, 6.04) * mm});
            skLineSegment(sketch, "E1105", {"start": v(13.74, 6.04) * mm, "end": v(13.9, 6) * mm});
            skLineSegment(sketch, "E1106", {"start": v(13.9, 6) * mm, "end": v(14.05, 5.98) * mm});
            skLineSegment(sketch, "E1107", {"start": v(14.05, 5.98) * mm, "end": v(14.2, 5.98) * mm});
            skLineSegment(sketch, "E1108", {"start": v(14.2, 5.98) * mm, "end": v(14.36, 6) * mm});
            skLineSegment(sketch, "E1109", {"start": v(14.36, 6) * mm, "end": v(14.51, 6.05) * mm});
            skLineSegment(sketch, "E1110", {"start": v(14.51, 6.05) * mm, "end": v(14.66, 6.1) * mm});
            skLineSegment(sketch, "E1111", {"start": v(24.6, 20.1) * mm, "end": v(24.92, 20.46) * mm});
            skLineSegment(sketch, "E1112", {"start": v(24.92, 20.46) * mm, "end": v(25.15, 20.88) * mm});
            skLineSegment(sketch, "E1113", {"start": v(25.15, 20.88) * mm, "end": v(25.3, 21.33) * mm});
            skLineSegment(sketch, "E1114", {"start": v(25.3, 21.33) * mm, "end": v(25.35, 21.79) * mm});
            skLineSegment(sketch, "E1115", {"start": v(25.35, 21.79) * mm, "end": v(25.32, 22.25) * mm});
            skLineSegment(sketch, "E1116", {"start": v(25.32, 22.25) * mm, "end": v(25.2, 22.7) * mm});
            skLineSegment(sketch, "E1117", {"start": v(25.2, 22.7) * mm, "end": v(24.98, 23.13) * mm});
            skLineSegment(sketch, "E1118", {"start": v(24.98, 23.13) * mm, "end": v(24.68, 23.52) * mm});
            skLineSegment(sketch, "E1119", {"start": v(24.68, 23.52) * mm, "end": v(24.3, 23.84) * mm});
            skLineSegment(sketch, "E1120", {"start": v(24.3, 23.84) * mm, "end": v(23.9, 24.07) * mm});
            skLineSegment(sketch, "E1121", {"start": v(23.9, 24.07) * mm, "end": v(23.45, 24.21) * mm});
            skLineSegment(sketch, "E1122", {"start": v(23.45, 24.21) * mm, "end": v(22.99, 24.27) * mm});
            skLineSegment(sketch, "E1123", {"start": v(22.99, 24.27) * mm, "end": v(22.52, 24.23) * mm});
            skLineSegment(sketch, "E1124", {"start": v(22.52, 24.23) * mm, "end": v(22.07, 24.11) * mm});
            skLineSegment(sketch, "E1125", {"start": v(22.07, 24.11) * mm, "end": v(21.64, 23.9) * mm});
            skLineSegment(sketch, "E1126", {"start": v(21.64, 23.9) * mm, "end": v(21.26, 23.6) * mm});
            skLineSegment(sketch, "E1127", {"start": v(14.98, 5.27) * mm, "end": v(14.83, 5.22) * mm});
            skLineSegment(sketch, "E1128", {"start": v(14.83, 5.22) * mm, "end": v(14.69, 5.15) * mm});
            skLineSegment(sketch, "E1129", {"start": v(14.69, 5.15) * mm, "end": v(14.56, 5.06) * mm});
            skLineSegment(sketch, "E1130", {"start": v(14.56, 5.06) * mm, "end": v(14.44, 4.95) * mm});
            skLineSegment(sketch, "E1131", {"start": v(14.44, 4.95) * mm, "end": v(14.34, 4.84) * mm});
            skLineSegment(sketch, "E1132", {"start": v(14.34, 4.84) * mm, "end": v(14.25, 4.7) * mm});
            skLineSegment(sketch, "E1133", {"start": v(14.25, 4.7) * mm, "end": v(14.18, 4.56) * mm});
            skLineSegment(sketch, "E1134", {"start": v(14.18, 4.56) * mm, "end": v(14.13, 4.41) * mm});
            skLineSegment(sketch, "E1135", {"start": v(14.13, 4.41) * mm, "end": v(14.1, 4.25) * mm});
            skLineSegment(sketch, "E1136", {"start": v(14.1, 4.25) * mm, "end": v(14.08, 4.1) * mm});
            skLineSegment(sketch, "E1137", {"start": v(14.08, 4.1) * mm, "end": v(14.1, 3.94) * mm});
            skLineSegment(sketch, "E1138", {"start": v(14.1, 3.94) * mm, "end": v(14.13, 3.78) * mm});
            skLineSegment(sketch, "E1139", {"start": v(14.13, 3.78) * mm, "end": v(14.18, 3.64) * mm});
            skLineSegment(sketch, "E1140", {"start": v(14.18, 3.64) * mm, "end": v(14.25, 3.5) * mm});
            skLineSegment(sketch, "E1141", {"start": v(14.25, 3.5) * mm, "end": v(14.33, 3.36) * mm});
            skLineSegment(sketch, "E1142", {"start": v(14.33, 3.36) * mm, "end": v(14.44, 3.24) * mm});
            skLineSegment(sketch, "E1143", {"start": v(14.44, 3.24) * mm, "end": v(14.56, 3.14) * mm});
            skLineSegment(sketch, "E1144", {"start": v(14.56, 3.14) * mm, "end": v(14.7, 3.05) * mm});
            skLineSegment(sketch, "E1145", {"start": v(14.7, 3.05) * mm, "end": v(14.83, 2.98) * mm});
            skLineSegment(sketch, "E1146", {"start": v(14.83, 2.98) * mm, "end": v(14.98, 2.93) * mm});
            skLineSegment(sketch, "E1147", {"start": v(14.98, 2.93) * mm, "end": v(15.14, 2.9) * mm});
            skLineSegment(sketch, "E1148", {"start": v(15.14, 2.9) * mm, "end": v(15.3, 2.89) * mm});
            skLineSegment(sketch, "E1149", {"start": v(15.3, 2.89) * mm, "end": v(15.45, 2.9) * mm});
            skLineSegment(sketch, "E1150", {"start": v(15.45, 2.9) * mm, "end": v(15.6, 2.93) * mm});
            skLineSegment(sketch, "E1151", {"start": v(28.24, 14.54) * mm, "end": v(28.63, 14.84) * mm});
            skLineSegment(sketch, "E1152", {"start": v(28.63, 14.84) * mm, "end": v(28.94, 15.2) * mm});
            skLineSegment(sketch, "E1153", {"start": v(28.94, 15.2) * mm, "end": v(29.17, 15.6) * mm});
            skLineSegment(sketch, "E1154", {"start": v(29.17, 15.6) * mm, "end": v(29.32, 16.04) * mm});
            skLineSegment(sketch, "E1155", {"start": v(29.32, 16.04) * mm, "end": v(29.39, 16.5) * mm});
            skLineSegment(sketch, "E1156", {"start": v(29.39, 16.5) * mm, "end": v(29.36, 16.97) * mm});
            skLineSegment(sketch, "E1157", {"start": v(29.36, 16.97) * mm, "end": v(29.24, 17.43) * mm});
            skLineSegment(sketch, "E1158", {"start": v(29.24, 17.43) * mm, "end": v(29.03, 17.87) * mm});
            skLineSegment(sketch, "E1159", {"start": v(29.03, 17.87) * mm, "end": v(28.73, 18.26) * mm});
            skLineSegment(sketch, "E1160", {"start": v(28.73, 18.26) * mm, "end": v(28.37, 18.58) * mm});
            skLineSegment(sketch, "E1161", {"start": v(28.37, 18.58) * mm, "end": v(27.97, 18.8) * mm});
            skLineSegment(sketch, "E1162", {"start": v(27.97, 18.8) * mm, "end": v(27.53, 18.96) * mm});
            skLineSegment(sketch, "E1163", {"start": v(27.53, 18.96) * mm, "end": v(27.07, 19.02) * mm});
            skLineSegment(sketch, "E1164", {"start": v(27.07, 19.02) * mm, "end": v(26.6, 19) * mm});
            skLineSegment(sketch, "E1165", {"start": v(26.6, 19) * mm, "end": v(26.14, 18.88) * mm});
            skLineSegment(sketch, "E1166", {"start": v(26.14, 18.88) * mm, "end": v(25.7, 18.67) * mm});
            skLineSegment(sketch, "E1167", {"start": v(15.75, 2.04) * mm, "end": v(15.6, 2.02) * mm});
            skLineSegment(sketch, "E1168", {"start": v(15.6, 2.02) * mm, "end": v(15.44, 1.98) * mm});
            skLineSegment(sketch, "E1169", {"start": v(15.44, 1.98) * mm, "end": v(15.3, 1.92) * mm});
            skLineSegment(sketch, "E1170", {"start": v(15.3, 1.92) * mm, "end": v(15.15, 1.84) * mm});
            skLineSegment(sketch, "E1171", {"start": v(15.15, 1.84) * mm, "end": v(15.03, 1.75) * mm});
            skLineSegment(sketch, "E1172", {"start": v(15.03, 1.75) * mm, "end": v(14.92, 1.64) * mm});
            skLineSegment(sketch, "E1173", {"start": v(14.92, 1.64) * mm, "end": v(14.82, 1.52) * mm});
            skLineSegment(sketch, "E1174", {"start": v(14.82, 1.52) * mm, "end": v(14.73, 1.38) * mm});
            skLineSegment(sketch, "E1175", {"start": v(14.73, 1.38) * mm, "end": v(14.67, 1.23) * mm});
            skLineSegment(sketch, "E1176", {"start": v(14.67, 1.23) * mm, "end": v(14.63, 1.08) * mm});
            skLineSegment(sketch, "E1177", {"start": v(14.63, 1.08) * mm, "end": v(14.6, 0.92) * mm});
            skLineSegment(sketch, "E1178", {"start": v(14.6, 0.92) * mm, "end": v(14.6, 0.77) * mm});
            skLineSegment(sketch, "E1179", {"start": v(14.6, 0.77) * mm, "end": v(14.62, 0.6) * mm});
            skLineSegment(sketch, "E1180", {"start": v(14.62, 0.6) * mm, "end": v(14.66, 0.46) * mm});
            skLineSegment(sketch, "E1181", {"start": v(14.66, 0.46) * mm, "end": v(14.72, 0.3) * mm});
            skLineSegment(sketch, "E1182", {"start": v(14.72, 0.3) * mm, "end": v(14.8, 0.17) * mm});
            skLineSegment(sketch, "E1183", {"start": v(14.8, 0.17) * mm, "end": v(14.9, 0.04) * mm});
            skLineSegment(sketch, "E1184", {"start": v(14.9, 0.04) * mm, "end": v(15, -0.07) * mm});
            skLineSegment(sketch, "E1185", {"start": v(15, -0.07) * mm, "end": v(15.13, -0.17) * mm});
            skLineSegment(sketch, "E1186", {"start": v(15.13, -0.17) * mm, "end": v(15.26, -0.25) * mm});
            skLineSegment(sketch, "E1187", {"start": v(15.26, -0.25) * mm, "end": v(15.4, -0.31) * mm});
            skLineSegment(sketch, "E1188", {"start": v(15.4, -0.31) * mm, "end": v(15.56, -0.36) * mm});
            skLineSegment(sketch, "E1189", {"start": v(15.56, -0.36) * mm, "end": v(15.72, -0.38) * mm});
            skLineSegment(sketch, "E1190", {"start": v(15.72, -0.38) * mm, "end": v(15.88, -0.38) * mm});
            skArc(sketch, "E1191", {"start": v(32.03, 6.54) * mm, "mid": v(31.85, 7.35) * mm, "end": v(31.65, 8.15) * mm});
            skArc(sketch, "E1192.trimOffspring", {"start": v(32.69, -0.27) * mm, "mid": v(32.67, 0.92) * mm, "end": v(32.62, 2.11) * mm});
            skArc(sketch, "E1193.trimOffspring", {"start": v(31.92, -7.05) * mm, "mid": v(32.15, -5.89) * mm, "end": v(32.35, -4.72) * mm});
            skArc(sketch, "E1194.trimOffspring", {"start": v(29.75, -13.54) * mm, "mid": v(30.23, -12.45) * mm, "end": v(30.66, -11.34) * mm});
            skArc(sketch, "E1195.trimOffspring", {"start": v(26.29, -19.43) * mm, "mid": v(26.98, -18.46) * mm, "end": v(27.63, -17.46) * mm});
            skArc(sketch, "E1196.trimOffspring", {"start": v(21.68, -24.47) * mm, "mid": v(22.55, -23.66) * mm, "end": v(23.4, -22.83) * mm});
            skArc(sketch, "E1197.trimOffspring", {"start": v(16.11, -28.44) * mm, "mid": v(17.14, -27.83) * mm, "end": v(18.14, -27.2) * mm});
            skArc(sketch, "E1198.trimOffspring", {"start": v(9.85, -31.17) * mm, "mid": v(10.98, -30.79) * mm, "end": v(12.1, -30.37) * mm});
            skArc(sketch, "E1199.trimOffspring", {"start": v(3.15, -32.54) * mm, "mid": v(4.34, -32.4) * mm, "end": v(5.51, -32.22) * mm});
            skArc(sketch, "E1200.trimOffspring", {"start": v(-3.68, -32.48) * mm, "mid": v(-2.5, -32.6) * mm, "end": v(-1.3, -32.66) * mm});
            skArc(sketch, "E1201.trimOffspring", {"start": v(-10.35, -31) * mm, "mid": v(-9.22, -31.36) * mm, "end": v(-8.07, -31.68) * mm});
            skArc(sketch, "E1202.trimOffspring", {"start": v(-16.57, -28.17) * mm, "mid": v(-15.54, -28.76) * mm, "end": v(-14.48, -29.3) * mm});
            skArc(sketch, "E1203.trimOffspring", {"start": v(-22.07, -24.11) * mm, "mid": v(-21.18, -24.9) * mm, "end": v(-20.25, -25.66) * mm});
            skArc(sketch, "E1204.trimOffspring", {"start": v(-26.6, -19) * mm, "mid": v(-25.9, -19.95) * mm, "end": v(-25.15, -20.88) * mm});
            skArc(sketch, "E1205.trimOffspring", {"start": v(-29.97, -13.05) * mm, "mid": v(-29.47, -14.13) * mm, "end": v(-28.94, -15.2) * mm});
            skArc(sketch, "E1206.trimOffspring", {"start": v(-32.03, -6.53) * mm, "mid": v(-31.77, -7.7) * mm, "end": v(-31.47, -8.85) * mm});
            skArc(sketch, "E1207.trimOffspring", {"start": v(-32.69, 0.27) * mm, "mid": v(-32.67, -0.92) * mm, "end": v(-32.62, -2.12) * mm});
            skArc(sketch, "E1208.trimOffspring", {"start": v(-31.92, 7.06) * mm, "mid": v(-32.15, 5.9) * mm, "end": v(-32.35, 4.71) * mm});
            skArc(sketch, "E1209.trimOffspring", {"start": v(-29.75, 13.54) * mm, "mid": v(-30.23, 12.45) * mm, "end": v(-30.66, 11.34) * mm});
            skArc(sketch, "E1210.trimOffspring", {"start": v(-26.29, 19.43) * mm, "mid": v(-26.98, 18.46) * mm, "end": v(-27.63, 17.46) * mm});
            skArc(sketch, "E1211.trimOffspring", {"start": v(-21.67, 24.47) * mm, "mid": v(-22.55, 23.66) * mm, "end": v(-23.4, 22.83) * mm});
            skArc(sketch, "E1212.trimOffspring", {"start": v(-16.1, 28.44) * mm, "mid": v(-17.14, 27.84) * mm, "end": v(-18.14, 27.2) * mm});
            skArc(sketch, "E1213.trimOffspring", {"start": v(-9.84, 31.17) * mm, "mid": v(-10.97, 30.8) * mm, "end": v(-12.09, 30.37) * mm});
            skArc(sketch, "E1214.trimOffspring", {"start": v(-3.15, 32.54) * mm, "mid": v(-4.33, 32.4) * mm, "end": v(-5.51, 32.22) * mm});
            skArc(sketch, "E1215.trimOffspring", {"start": v(3.68, 32.48) * mm, "mid": v(2.5, 32.6) * mm, "end": v(1.3, 32.66) * mm});
            skArc(sketch, "E1216.trimOffspring", {"start": v(10.36, 31) * mm, "mid": v(9.22, 31.36) * mm, "end": v(8.07, 31.68) * mm});
            skArc(sketch, "E1217.trimOffspring", {"start": v(16.57, 28.17) * mm, "mid": v(15.54, 28.76) * mm, "end": v(14.48, 29.3) * mm});
            skArc(sketch, "E1218.trimOffspring", {"start": v(22.07, 24.11) * mm, "mid": v(21.18, 24.9) * mm, "end": v(20.26, 25.65) * mm});
            skArc(sketch, "E1219.trimOffspring", {"start": v(26.6, 19) * mm, "mid": v(25.9, 19.95) * mm, "end": v(25.15, 20.88) * mm});
            skArc(sketch, "E1220", {"start": v(15.46, -1.28) * mm, "mid": v(15.5, -0.81) * mm, "end": v(15.51, -0.34) * mm});
            skArc(sketch, "E1221.trimOffspring", {"start": v(15.4, 1.96) * mm, "mid": v(15.32, 2.43) * mm, "end": v(15.24, 2.89) * mm});
            skArc(sketch, "E1222.trimOffspring", {"start": v(14.65, 5.12) * mm, "mid": v(14.48, 5.56) * mm, "end": v(14.3, 6) * mm});
            skLineSegment(sketch, "E1223", {"start": v(29.6, 13.86) * mm, "end": v(35.06, 16.18) * mm});
            skLineSegment(sketch, "E1224", {"start": v(35.06, 16.18) * mm, "end": v(37.38, 9.63) * mm});
            skLineSegment(sketch, "E1225", {"start": v(37.38, 9.63) * mm, "end": v(31.65, 8.15) * mm});
            skArc(sketch, "E1226.trimOffspring", {"start": v(29.6, 13.86) * mm, "mid": v(29.28, 14.53) * mm, "end": v(28.94, 15.2) * mm});
            skArc(sketch, "E1227.trimOffspring", {"start": v(13.26, 8.05) * mm, "mid": v(13.01, 8.45) * mm, "end": v(12.75, 8.84) * mm});
            skArc(sketch, "E1228.trimOffspring", {"start": v(11.3, 10.63) * mm, "mid": v(10.97, 10.97) * mm, "end": v(10.63, 11.3) * mm});
            skArc(sketch, "E1229.trimOffspring", {"start": v(8.84, 12.75) * mm, "mid": v(8.45, 13.01) * mm, "end": v(8.05, 13.26) * mm});
            skArc(sketch, "E1230.trimOffspring", {"start": v(6, 14.3) * mm, "mid": v(5.56, 14.48) * mm, "end": v(5.12, 14.65) * mm});
            skArc(sketch, "E1231.trimOffspring", {"start": v(2.9, 15.24) * mm, "mid": v(2.43, 15.32) * mm, "end": v(1.96, 15.4) * mm});
            skArc(sketch, "E1232.trimOffspring", {"start": v(-0.34, 15.51) * mm, "mid": v(-0.81, 15.5) * mm, "end": v(-1.28, 15.46) * mm});
            skArc(sketch, "E1233.trimOffspring", {"start": v(-3.56, 15.1) * mm, "mid": v(-4.01, 14.99) * mm, "end": v(-4.47, 14.86) * mm});
            skArc(sketch, "E1234.trimOffspring", {"start": v(-6.62, 14.03) * mm, "mid": v(-7.04, 13.82) * mm, "end": v(-7.46, 13.6) * mm});
            skArc(sketch, "E1235.trimOffspring", {"start": v(-9.4, 12.35) * mm, "mid": v(-9.76, 12.06) * mm, "end": v(-10.13, 11.76) * mm});
            skArc(sketch, "E1236.trimOffspring", {"start": v(-11.75, 10.13) * mm, "mid": v(-12.06, 9.76) * mm, "end": v(-12.35, 9.4) * mm});
            skArc(sketch, "E1237.trimOffspring", {"start": v(-13.6, 7.46) * mm, "mid": v(-13.82, 7.04) * mm, "end": v(-14.03, 6.62) * mm});
            skArc(sketch, "E1238.trimOffspring", {"start": v(-14.86, 4.47) * mm, "mid": v(-14.99, 4.02) * mm, "end": v(-15.1, 3.56) * mm});
            skArc(sketch, "E1239.trimOffspring", {"start": v(-15.4, -1.96) * mm, "mid": v(-14.99, -4.02) * mm, "end": v(-14.3, -6) * mm});
            skArc(sketch, "E1240.trimOffspring", {"start": v(-13.26, -8.05) * mm, "mid": v(-13.01, -8.45) * mm, "end": v(-12.75, -8.84) * mm});
            skArc(sketch, "E1241.trimOffspring", {"start": v(-11.3, -10.63) * mm, "mid": v(-10.97, -10.97) * mm, "end": v(-10.63, -11.3) * mm});
            skArc(sketch, "E1242.trimOffspring", {"start": v(-8.84, -12.75) * mm, "mid": v(-8.45, -13.01) * mm, "end": v(-8.05, -13.26) * mm});
            skArc(sketch, "E1243.trimOffspring", {"start": v(-6, -14.3) * mm, "mid": v(-5.56, -14.49) * mm, "end": v(-5.11, -14.65) * mm});
            skArc(sketch, "E1244.trimOffspring", {"start": v(-2.9, -15.24) * mm, "mid": v(-2.43, -15.32) * mm, "end": v(-1.96, -15.4) * mm});
            skArc(sketch, "E1245.trimOffspring", {"start": v(0.34, -15.51) * mm, "mid": v(0.81, -15.5) * mm, "end": v(1.28, -15.46) * mm});
            skArc(sketch, "E1246.trimOffspring", {"start": v(3.56, -15.1) * mm, "mid": v(4.02, -14.99) * mm, "end": v(4.47, -14.86) * mm});
            skArc(sketch, "E1247.trimOffspring", {"start": v(6.62, -14.03) * mm, "mid": v(7.05, -13.82) * mm, "end": v(7.46, -13.6) * mm});
            skArc(sketch, "E1248.trimOffspring", {"start": v(9.4, -12.35) * mm, "mid": v(9.77, -12.06) * mm, "end": v(10.13, -11.76) * mm});
            skArc(sketch, "E1249.trimOffspring", {"start": v(11.76, -10.12) * mm, "mid": v(12.06, -9.76) * mm, "end": v(12.35, -9.4) * mm});
            skArc(sketch, "E1250.trimOffspring", {"start": v(13.6, -7.46) * mm, "mid": v(13.82, -7.04) * mm, "end": v(14.03, -6.62) * mm});
            skArc(sketch, "E1251.trimOffspring", {"start": v(14.86, -4.47) * mm, "mid": v(14.99, -4.02) * mm, "end": v(15.1, -3.56) * mm});
            skLineSegment(sketch, "E1252", {"start": v(-15.46, 1.28) * mm, "end": v(-15.51, 0.34) * mm});
            skSolve(sketch);
        }
        {
            var Q0;
            Q0=makeQuery(id+"F0.imprint","IMPRINT",FACE,{"disambiguationData":[TD([[makeQuery(id+"F0.imprint","IMPRINT",EDGE,{"derivedFrom":sQuery(id+"F0.wireOp",EDGE,"E0")}),1.0]])]});
            var Q1;
            Q1=makeQuery(id+"F0.imprint","IMPRINT",FACE,{"disambiguationData":[TD([[makeQuery(id+"F0.imprint","IMPRINT",EDGE,{"derivedFrom":sQuery(id+"F0.wireOp",EDGE,"E5")}),-1.0]])]});
            extrude(context, id + "F1", {"entities" : qUnion([Q0, Q1]), "oppositeDirection" : true, "depth" : 1.52 * mm});
        }
        {
            var Q0;
            Q0=makeQuery(id+"F1.opExtrude","CAP_FACE",FACE,{"disambiguationData":[OSD([sQuery(id+"F0.wireOp",EDGE,"a0ee4e53-7b65-4cc6-b097-e980374bba51"),sQuery(id+"F0.wireOp",EDGE,"28782ac0-7b0e-4891-8199-3a4f1225c46d"),sQuery(id+"F0.wireOp",EDGE,"43ffe4ab-a3be-41a3-bc0c-c6412107e32e"),sQuery(id+"F0.wireOp",EDGE,"dc48e744-2bf8-4d28-8ee7-cce8e2fb5321"),sQuery(id+"F0.wireOp",EDGE,"bf8fdbad-5b4a-41a4-b04b-4c9f6464a9db"),sQuery(id+"F0.wireOp",EDGE,"c0fb4448-2790-4191-9f6e-ebd55608eed1"),sQuery(id+"F0.wireOp",EDGE,"93d0b0e8-c43c-4f3d-a24c-1e9478296678"),sQuery(id+"F0.wireOp",EDGE,"7697e389-9dc3-460e-a292-7d678f4f1f46"),sQuery(id+"F0.wireOp",EDGE,"813d6692-cfe2-4671-8476-199ab0adf0d9"),sQuery(id+"F0.wireOp",EDGE,"7046412e-9f64-4fbd-a4c4-bef392f06694"),sQuery(id+"F0.wireOp",EDGE,"675f2f7f-5611-4529-bcab-d7c1451cd4fa"),sQuery(id+"F0.wireOp",EDGE,"d182c7ab-291f-44e7-a90d-3923d8b53343"),sQuery(id+"F0.wireOp",EDGE,"936cdbd5-7158-42f7-b2bc-9502d12045dd"),sQuery(id+"F0.wireOp",EDGE,"5752c7da-8fc2-4d80-9823-127daa68e405"),sQuery(id+"F0.wireOp",EDGE,"4bcbabae-024d-4715-a612-e5412e92e144"),sQuery(id+"F0.wireOp",EDGE,"0fc41205-7475-48f9-bf52-c23a16a363bf"),sQuery(id+"F0.wireOp",EDGE,"f1db7064-d933-4c26-99cf-68692b19b403"),sQuery(id+"F0.wireOp",EDGE,"0ec743de-02d6-41bf-b949-6e33cf799153"),sQuery(id+"F0.wireOp",EDGE,"deed504f-6629-4c3e-b731-5790958551cc"),sQuery(id+"F0.wireOp",EDGE,"9a4cfbdf-9131-4cb8-b0cc-ffaa8761dad6"),sQuery(id+"F0.wireOp",EDGE,"7d4f937e-aba7-4631-bb69-18a2a736b779"),sQuery(id+"F0.wireOp",EDGE,"99003f90-dbef-4bbf-a855-fc3390bd2bda"),sQuery(id+"F0.wireOp",EDGE,"698dfc52-a86a-49ff-ad8f-042d98267aa1"),sQuery(id+"F0.wireOp",EDGE,"26a38619-e418-4834-bf8f-41458db517ca"),sQuery(id+"F0.wireOp",EDGE,"99986c6a-a6f3-4f5e-bfa0-b9f2e2ee64ed"),sQuery(id+"F0.wireOp",EDGE,"927d7d57-56ba-42a1-be55-3bb78293e291"),sQuery(id+"F0.wireOp",EDGE,"917b3803-a639-43a1-b0b1-d80f0c2bfdf7"),sQuery(id+"F0.wireOp",EDGE,"fac2830c-de90-4a53-83eb-ba410fa5ca71"),sQuery(id+"F0.wireOp",EDGE,"b911d83d-b9a1-4f01-b092-ce727761331b"),sQuery(id+"F0.wireOp",EDGE,"1a262198-34e3-445f-bcdb-42479f9a2192"),sQuery(id+"F0.wireOp",EDGE,"fde727ea-d3f2-4d38-a1d9-f9d9e8608d47"),sQuery(id+"F0.wireOp",EDGE,"7dba479d-2e9f-4ea1-be82-347138dca80f"),sQuery(id+"F0.wireOp",EDGE,"bb5bd3ef-d1c4-42b3-b515-f442d456ab7f"),sQuery(id+"F0.wireOp",EDGE,"49241490-21fc-4964-bb50-688fcb6a107a"),sQuery(id+"F0.wireOp",EDGE,"7bad562f-b72e-4cbc-b13e-860ad0cf9277"),sQuery(id+"F0.wireOp",EDGE,"01a38179-a4ec-4c18-81b7-e22eaecd6366"),sQuery(id+"F0.wireOp",EDGE,"5800b559-6ef2-4f17-b4a8-af959ec671b9"),sQuery(id+"F0.wireOp",EDGE,"4d956042-3511-4874-b9bb-0d4904a742e4"),sQuery(id+"F0.wireOp",EDGE,"c6bcc5a0-b07b-43b9-84d6-51167e28eca0"),sQuery(id+"F0.wireOp",EDGE,"025251d3-07ff-4811-aadc-cf0b2832a614"),sQuery(id+"F0.wireOp",EDGE,"844a8369-a0e8-48f8-ad11-e99884c9d341"),sQuery(id+"F0.wireOp",EDGE,"4305cde0-a5c6-406d-bf74-c08e412d9c01"),sQuery(id+"F0.wireOp",EDGE,"f626a75d-f29d-4dae-b1ed-059d04aca0bb"),sQuery(id+"F0.wireOp",EDGE,"3167a2a2-c5cd-48e4-a576-9c03de96c99d"),sQuery(id+"F0.wireOp",EDGE,"4c9d0dfe-649b-45d2-89bb-e6e2d6144dd4"),sQuery(id+"F0.wireOp",EDGE,"93b8ff5d-ef36-4af5-bf9f-a9f03e630389"),sQuery(id+"F0.wireOp",EDGE,"1885d607-f4dd-4d4e-9b3a-c26a6558c21a"),sQuery(id+"F0.wireOp",EDGE,"fd400388-1826-4c05-92b3-6777b2abc366"),sQuery(id+"F0.wireOp",EDGE,"1cb44d1c-5766-421b-8fef-6cd898336a52"),sQuery(id+"F0.wireOp",EDGE,"a0bcb158-6438-4e12-8a33-a74f335f686b"),sQuery(id+"F0.wireOp",EDGE,"f4bf6fd0-f838-4daa-8398-16fb0174a711"),sQuery(id+"F0.wireOp",EDGE,"d8b35c5f-17c5-4792-9456-c95466667781"),sQuery(id+"F0.wireOp",EDGE,"bfe3515a-151a-421e-82ba-14c4ed01c104"),sQuery(id+"F0.wireOp",EDGE,"ea735a5d-e4a1-4bf0-bc4f-da954ba21756"),sQuery(id+"F0.wireOp",EDGE,"6f267e62-032a-41a0-a47b-0e38db9726c5"),sQuery(id+"F0.wireOp",EDGE,"f3c7efec-2d04-4889-8a84-6e23f8f453a8"),sQuery(id+"F0.wireOp",EDGE,"935b57b8-2ce8-4740-be8f-4c69f6861abc"),sQuery(id+"F0.wireOp",EDGE,"6a37a2fe-1895-4ddd-9acb-bb1008877e29"),sQuery(id+"F0.wireOp",EDGE,"945a5a56-fe4d-47f2-b0aa-3f664f46c8ce"),sQuery(id+"F0.wireOp",EDGE,"ccc36d2f-104f-4017-afb7-f5c232ead2b3"),sQuery(id+"F0.wireOp",EDGE,"74861551-2099-47a1-b3e9-b461e7654287"),sQuery(id+"F0.wireOp",EDGE,"94141ea7-f131-4d6c-9b24-91e97f046ca4"),sQuery(id+"F0.wireOp",EDGE,"6bf83433-f798-478b-ae11-3d14ff05e5f3"),sQuery(id+"F0.wireOp",EDGE,"b96ffd9e-08be-4fa3-b3c1-3a31803a5b98"),sQuery(id+"F0.wireOp",EDGE,"b988f938-0f38-4c7c-9c95-ba21683367cf"),sQuery(id+"F0.wireOp",EDGE,"7f481302-255c-4ead-abc0-9a86e5c75a6c"),sQuery(id+"F0.wireOp",EDGE,"65df0fc2-c32a-402a-83f0-ffb7ead4d9e1"),sQuery(id+"F0.wireOp",EDGE,"1c83dd0f-eeec-4aea-b55d-64ac17ef288b"),sQuery(id+"F0.wireOp",EDGE,"61e7d2f3-8aa3-42f8-be86-1ebe91e02449"),sQuery(id+"F0.wireOp",EDGE,"1f13731c-77a8-4b15-afb5-967201fed954"),sQuery(id+"F0.wireOp",EDGE,"5e3f37b1-bafc-4778-bd7b-9a8112a22db5"),sQuery(id+"F0.wireOp",EDGE,"ee869f63-584a-43a4-9dac-c7bd6a02345a"),sQuery(id+"F0.wireOp",EDGE,"334b3f0f-87ad-43a5-99e9-5ab06b61060d"),sQuery(id+"F0.wireOp",EDGE,"d1695426-a1c5-49ca-b27d-0470f6942fc0"),sQuery(id+"F0.wireOp",EDGE,"1e6db00c-971b-48e3-ad57-b6839dfbcd10"),sQuery(id+"F0.wireOp",EDGE,"6a7fc925-6b68-49f6-a060-aab8e61d80bf"),sQuery(id+"F0.wireOp",EDGE,"a6a50006-6686-43d2-bde7-6996d55a3639"),sQuery(id+"F0.wireOp",EDGE,"47551230-7048-47fa-a27b-3174c446d38c"),sQuery(id+"F0.wireOp",EDGE,"39de9ed5-567b-445e-8a33-ec328456a919"),sQuery(id+"F0.wireOp",EDGE,"616ab9ce-760f-49aa-853c-4c71a6d32f52"),sQuery(id+"F0.wireOp",EDGE,"d46438af-8e10-4ec2-aeb9-396b9f5ef0fe"),sQuery(id+"F0.wireOp",EDGE,"3e4c557b-6bb7-4f54-913b-6ffc9c01923e"),sQuery(id+"F0.wireOp",EDGE,"0561e19c-cec4-463e-b3ca-e07bc53f99fc"),sQuery(id+"F0.wireOp",EDGE,"4f69e275-a90f-42cb-b993-f32d5310bdc2"),sQuery(id+"F0.wireOp",EDGE,"3dceb406-efe1-4fba-b68b-f4750cb478c0"),sQuery(id+"F0.wireOp",EDGE,"6d6b4f68-d82c-4b13-8153-59f03dd766ce"),sQuery(id+"F0.wireOp",EDGE,"3f3f2b81-7944-401d-9760-aefb5adfbdd2"),sQuery(id+"F0.wireOp",EDGE,"6a281107-5eec-4b71-ad6d-7e9851cda6ff"),sQuery(id+"F0.wireOp",EDGE,"24290a7b-1717-49d8-9f8a-11d0b35eb97d"),sQuery(id+"F0.wireOp",EDGE,"96a33a07-8776-4d87-b4cf-5df261abaafc"),sQuery(id+"F0.wireOp",EDGE,"8a754f7d-a2d3-47ec-990a-456960389fdb"),sQuery(id+"F0.wireOp",EDGE,"8a121ea7-0a02-4e91-95be-be751a87abd7"),sQuery(id+"F0.wireOp",EDGE,"ac0b32c6-eb4e-4305-a7e9-c8758a3032db"),sQuery(id+"F0.wireOp",EDGE,"48be6210-4467-4e76-a565-52944eaa5ab4"),sQuery(id+"F0.wireOp",EDGE,"f3841175-05c6-4537-9ebc-bb7576f38844"),sQuery(id+"F0.wireOp",EDGE,"738a4f83-c68a-44fa-856f-3313b712e321"),sQuery(id+"F0.wireOp",EDGE,"8a3c3ad5-7bb9-49ef-9e64-89cea8360ec9"),sQuery(id+"F0.wireOp",EDGE,"3491ef82-f81f-47aa-9efb-fda760c1ba90"),sQuery(id+"F0.wireOp",EDGE,"b0dbeffd-962d-437e-8301-d083e651ea96"),sQuery(id+"F0.wireOp",EDGE,"7bf541af-1cc3-4389-9f99-8affcc4cc06c"),sQuery(id+"F0.wireOp",EDGE,"0f7e6a36-3e6f-4214-8028-9673e23972dd"),sQuery(id+"F0.wireOp",EDGE,"1051ff0f-ef06-47de-ae6e-bbc6304fbfe4"),sQuery(id+"F0.wireOp",EDGE,"2fbf7309-9164-4e4f-b9bc-b90a2e9caa85"),sQuery(id+"F0.wireOp",EDGE,"7bc15c66-0dc6-4fac-9768-d519c7ab8e01"),sQuery(id+"F0.wireOp",EDGE,"f89ba450-3f42-4a19-9785-9c63077fbecb"),sQuery(id+"F0.wireOp",EDGE,"f0963e65-d15b-411e-a95d-49595ba11381"),sQuery(id+"F0.wireOp",EDGE,"1cab81b3-c50b-4e54-bc86-fe5adeff3f4b"),sQuery(id+"F0.wireOp",EDGE,"ac90957a-8136-4a52-99a4-20d8dc54c0fe"),sQuery(id+"F0.wireOp",EDGE,"99f6fa74-8db8-4dd4-9b0c-bfc228d54919"),sQuery(id+"F0.wireOp",EDGE,"d24a3037-63b1-4bde-bc79-7d3fa0d842d3"),sQuery(id+"F0.wireOp",EDGE,"be0ccf9b-9d53-44ad-a3f3-f56c6fdb8398"),sQuery(id+"F0.wireOp",EDGE,"bc538cb2-a427-4704-98b9-65cf2e40820e"),sQuery(id+"F0.wireOp",EDGE,"67486f26-85ba-468f-9cc7-064031b3d75f"),sQuery(id+"F0.wireOp",EDGE,"d1dffca6-a7ca-4465-8ccb-c4d17aeb9077"),sQuery(id+"F0.wireOp",EDGE,"7e919344-1e24-4dd2-bd49-eba118f65d2a"),sQuery(id+"F0.wireOp",EDGE,"13939587-63b0-4985-862b-05d1727cb0af"),sQuery(id+"F0.wireOp",EDGE,"c9fe85e5-755c-4665-ab19-45b6f299e369"),sQuery(id+"F0.wireOp",EDGE,"55a9b869-b362-4b86-b916-68e6c489148d"),sQuery(id+"F0.wireOp",EDGE,"6545422e-9b5f-4873-baf5-974d8a0efad4"),sQuery(id+"F0.wireOp",EDGE,"727e534f-723d-4cc8-84ba-b8d9cfeec071"),sQuery(id+"F0.wireOp",EDGE,"f736439a-afd7-4208-b50a-6dac63be6444"),sQuery(id+"F0.wireOp",EDGE,"e569db09-d282-4a18-9ea9-5d8b2509e23b"),sQuery(id+"F0.wireOp",EDGE,"c94a5938-bd95-4965-a3ba-1913b3aa616f"),sQuery(id+"F0.wireOp",EDGE,"43c68e4c-06b6-4df6-92bc-0e52d15587dd"),sQuery(id+"F0.wireOp",EDGE,"aa297102-daa2-4c0c-ae3a-dd2766206041"),sQuery(id+"F0.wireOp",EDGE,"e7ba9a92-ab4d-46b9-9cca-dc062a8327d1"),sQuery(id+"F0.wireOp",EDGE,"847797e3-3dc9-4971-a848-5569514e7d3c"),sQuery(id+"F0.wireOp",EDGE,"4a320543-99b8-4cf0-bd54-5048a3986884"),sQuery(id+"F0.wireOp",EDGE,"07d6b457-bec7-4bff-b681-0b815d9fe15b"),sQuery(id+"F0.wireOp",EDGE,"c88c16c9-fe87-43de-9813-2d066290cedc"),sQuery(id+"F0.wireOp",EDGE,"1b731034-9c0b-4618-90ef-f5c08baf83c6"),sQuery(id+"F0.wireOp",EDGE,"d5efd0d0-26f2-40de-91e4-a2bdaf0fe06e"),sQuery(id+"F0.wireOp",EDGE,"de69d900-2932-4f84-a5c7-088718f9f242"),sQuery(id+"F0.wireOp",EDGE,"d7a1f0f2-0789-4291-9e79-99522084d9cf"),sQuery(id+"F0.wireOp",EDGE,"aa1a97d6-9360-4391-a3a3-865fd1dd5ae6"),sQuery(id+"F0.wireOp",EDGE,"fb98d708-de0e-4a1a-a63b-dcd059c045cd"),sQuery(id+"F0.wireOp",EDGE,"72f19fba-b03f-47d7-8e86-5aa40006db50"),sQuery(id+"F0.wireOp",EDGE,"16949400-9a0a-479a-b9a8-33db09345c5f"),sQuery(id+"F0.wireOp",EDGE,"7831d9a0-3a9c-447f-935d-1a59c5772436"),sQuery(id+"F0.wireOp",EDGE,"d9304da9-ae36-40fe-9ca2-7891bcdbf2ff"),sQuery(id+"F0.wireOp",EDGE,"7d689b09-a038-49bc-9104-e336cca6a260"),sQuery(id+"F0.wireOp",EDGE,"4dcb15a3-c703-48f5-a823-e4f10e41e73f"),sQuery(id+"F0.wireOp",EDGE,"438c4aff-c944-435f-954c-eff83fbdb4b5"),sQuery(id+"F0.wireOp",EDGE,"d8df2163-25a3-42db-82f8-d0909a75f245"),sQuery(id+"F0.wireOp",EDGE,"ea785a37-a159-4036-853a-24a4ba050102"),sQuery(id+"F0.wireOp",EDGE,"e424bf75-bb13-4a6a-86d5-e1a57735723f"),sQuery(id+"F0.wireOp",EDGE,"6420f827-5a91-433c-bbc2-09ef0ab5eb27"),sQuery(id+"F0.wireOp",EDGE,"b3587a16-729c-4f39-85b7-c0c805f2fdb1"),sQuery(id+"F0.wireOp",EDGE,"797de20e-a635-4c89-b806-16e3d98188a8"),sQuery(id+"F0.wireOp",EDGE,"336fa35a-780c-4d6c-b28f-c5f3750bd672"),sQuery(id+"F0.wireOp",EDGE,"bee6a76e-9d23-4995-8ab7-8531df7f144d"),sQuery(id+"F0.wireOp",EDGE,"8f4c86da-0b59-45c8-aedc-14b22fc91796"),sQuery(id+"F0.wireOp",EDGE,"985cb4a5-4683-4ae1-a011-8bf5a2fcf6b0"),sQuery(id+"F0.wireOp",EDGE,"17d0b9f7-43bc-4134-8b44-3fec2d6b708a"),sQuery(id+"F0.wireOp",EDGE,"c495664d-2375-4a9b-b6ea-95090bf72f5e"),sQuery(id+"F0.wireOp",EDGE,"bbcf04d4-ccc6-4d92-8d33-48e2bfbee461"),sQuery(id+"F0.wireOp",EDGE,"fac67708-3bdd-47fc-a718-b14ee28ff9e5"),sQuery(id+"F0.wireOp",EDGE,"aebf0e65-0e1a-4b3c-aa39-42e2ca52b193"),sQuery(id+"F0.wireOp",EDGE,"555e4dd1-6230-4988-87b7-8b7dadb2a9d2"),sQuery(id+"F0.wireOp",EDGE,"bf504a83-9dba-40de-84c3-502101af2714"),sQuery(id+"F0.wireOp",EDGE,"fadce42c-8f69-428a-b658-f6f8d6eb353d"),sQuery(id+"F0.wireOp",EDGE,"7c0a4797-3dea-40ed-9219-94c1405a0c12"),sQuery(id+"F0.wireOp",EDGE,"ad761fb6-ce24-4500-a799-3e71ff986c9b"),sQuery(id+"F0.wireOp",EDGE,"8f94daf9-1a92-4f2f-a168-fe1e2849e0a4"),sQuery(id+"F0.wireOp",EDGE,"4d29fdcd-854b-4467-9f86-8ef238888501"),sQuery(id+"F0.wireOp",EDGE,"a315fe7d-6266-49d0-af4c-74ab1e241cb3"),sQuery(id+"F0.wireOp",EDGE,"247d7d3b-696a-4077-b4b9-907c1b9ea7b7"),sQuery(id+"F0.wireOp",EDGE,"a0d54748-be99-4639-9743-a2de1cc90493"),sQuery(id+"F0.wireOp",EDGE,"e27e79a7-379b-44be-b6d4-06a7fab5db17"),sQuery(id+"F0.wireOp",EDGE,"6dbe1323-1ff3-459e-aa4a-0a2cda1b8f69"),sQuery(id+"F0.wireOp",EDGE,"a475f993-d7fe-4669-92dd-6d5099f62343"),sQuery(id+"F0.wireOp",EDGE,"bd2dcd8d-1c13-459b-8b67-5d8b5cd3d02c"),sQuery(id+"F0.wireOp",EDGE,"041a13ff-0f98-47c5-a5a8-7731296a202a"),sQuery(id+"F0.wireOp",EDGE,"efcbeb58-b9e6-434e-aafb-f2caea61a543"),sQuery(id+"F0.wireOp",EDGE,"621733e0-c581-4189-9c70-74d05e258c2e"),sQuery(id+"F0.wireOp",EDGE,"e68780e2-9846-46d1-a978-c555b5663c7c"),sQuery(id+"F0.wireOp",EDGE,"f73636c8-39fc-46c1-b7ba-a055fdd8d873"),sQuery(id+"F0.wireOp",EDGE,"ab133b1c-5c7d-4a15-8c51-87f40838a200"),sQuery(id+"F0.wireOp",EDGE,"246a4357-1727-4672-a319-95a7f0266f2d"),sQuery(id+"F0.wireOp",EDGE,"eeac33ee-0c54-4d82-ac5a-aaf4af6d4639"),sQuery(id+"F0.wireOp",EDGE,"9fb83c6c-2e0c-4495-9731-eca2780b59da"),sQuery(id+"F0.wireOp",EDGE,"61322b04-a650-4460-a93f-15139eef680a"),sQuery(id+"F0.wireOp",EDGE,"5e367480-fc0a-4cdc-b756-9619a975dec3"),sQuery(id+"F0.wireOp",EDGE,"0db463eb-09a4-4666-a842-815b03d0d38a"),sQuery(id+"F0.wireOp",EDGE,"905f70a6-497d-4883-b851-984a48cd9594"),sQuery(id+"F0.wireOp",EDGE,"dcae319a-da14-48e6-8f3c-e7e4bd11bad5"),sQuery(id+"F0.wireOp",EDGE,"2fce2187-f3bf-4338-abfc-758848bb28ee"),sQuery(id+"F0.wireOp",EDGE,"daac7d07-d822-4af9-92ae-f5dd82c6a041"),sQuery(id+"F0.wireOp",EDGE,"bfc088ed-77a6-49ed-9ff5-6c2b191bf0ad"),sQuery(id+"F0.wireOp",EDGE,"40a18498-d793-4027-9fd2-bc3ccb94f5dc"),sQuery(id+"F0.wireOp",EDGE,"87b37e8e-b3de-4061-9f8c-118ea2367425"),sQuery(id+"F0.wireOp",EDGE,"90fa7182-c915-4ae1-8588-5b13e40def36"),sQuery(id+"F0.wireOp",EDGE,"02230e9b-dc09-4a33-bc43-f0e49d2302dc"),sQuery(id+"F0.wireOp",EDGE,"7c3824a4-707c-4506-9c07-735912c535d2"),sQuery(id+"F0.wireOp",EDGE,"e1086339-4cb9-43f9-90aa-d77f84c0848b"),sQuery(id+"F0.wireOp",EDGE,"bc315a90-b46a-464b-998b-0982f1dd3dce"),sQuery(id+"F0.wireOp",EDGE,"54fc364b-1d5c-4734-839d-b2f6629a5a9c"),sQuery(id+"F0.wireOp",EDGE,"9e58e7e8-f3a6-4c14-abd9-63bccd610232"),sQuery(id+"F0.wireOp",EDGE,"b75b6e71-ab25-435c-b27a-96416875fef1"),sQuery(id+"F0.wireOp",EDGE,"33467386-7da1-4466-bac2-f063697ec0b0"),sQuery(id+"F0.wireOp",EDGE,"b40c37fc-8aa1-4597-9746-30cd3e7d9b24"),sQuery(id+"F0.wireOp",EDGE,"10870c8b-1772-4d2e-9b59-b64ad3106769"),sQuery(id+"F0.wireOp",EDGE,"b0f8336b-e4bd-4490-a9e6-976f2b7efe03"),sQuery(id+"F0.wireOp",EDGE,"1d57452c-5c0c-4054-9787-53f14be4ba52"),sQuery(id+"F0.wireOp",EDGE,"981288f3-b602-4186-ba49-b4ca6516d8d0"),sQuery(id+"F0.wireOp",EDGE,"3fae167c-06ad-4a0f-af93-932dc7f78fef"),sQuery(id+"F0.wireOp",EDGE,"6b817f3a-36be-450b-98c3-ee377c88008c"),sQuery(id+"F0.wireOp",EDGE,"e2075037-c5f5-408b-b9b8-b54b826ff48b"),sQuery(id+"F0.wireOp",EDGE,"d9e548c8-4fac-4dc1-9b26-770d64c4879c"),sQuery(id+"F0.wireOp",EDGE,"a208ac86-6e06-4d92-8d05-e1a57909a583"),sQuery(id+"F0.wireOp",EDGE,"5ab40081-5f11-40f6-b732-8a577d8852ca"),sQuery(id+"F0.wireOp",EDGE,"2b70d11d-5cb1-49ae-b429-7ac6262d9197"),sQuery(id+"F0.wireOp",EDGE,"17fa6ffb-fa94-4b00-a7f4-9b1ad321c381"),sQuery(id+"F0.wireOp",EDGE,"c598b84b-5f5f-4626-98f8-06b77259816f"),sQuery(id+"F0.wireOp",EDGE,"c42d389f-64a8-4e29-90ba-ad465b36c984"),sQuery(id+"F0.wireOp",EDGE,"6e76dcc9-8371-482c-b232-ecdc5d38dd5c"),sQuery(id+"F0.wireOp",EDGE,"61f5f20c-9c7e-4924-8642-d61aa6e6b6c3"),sQuery(id+"F0.wireOp",EDGE,"3e5b592b-86f2-4085-bb26-c21ce9f47295"),sQuery(id+"F0.wireOp",EDGE,"c77b56ee-1232-4b49-a01a-3e8a0768b101"),sQuery(id+"F0.wireOp",EDGE,"6bbec194-7ee8-4028-8a82-41026d6588f5"),sQuery(id+"F0.wireOp",EDGE,"be482f2f-9668-427e-acbe-cb45d5bfdaf2"),sQuery(id+"F0.wireOp",EDGE,"7c1635c5-ac3d-4faa-b7b0-b20362e751bb"),sQuery(id+"F0.wireOp",EDGE,"f5b7f320-62eb-4dbc-81c8-7a892fd5ed62"),sQuery(id+"F0.wireOp",EDGE,"03a4be1c-a707-4b0a-84fe-652fcd27591b"),sQuery(id+"F0.wireOp",EDGE,"578034fe-3c99-47ec-8eea-244122fb2900"),sQuery(id+"F0.wireOp",EDGE,"dc8f4cf5-a8dc-42df-b8c6-1c061cc03ccb"),sQuery(id+"F0.wireOp",EDGE,"4ecca4ca-5acd-4e26-b545-397786b4a4d8"),sQuery(id+"F0.wireOp",EDGE,"01868341-dcd4-4d86-9f69-6aa016659bce"),sQuery(id+"F0.wireOp",EDGE,"082c0d23-307c-426c-a5fd-40aaf1ed85fe"),sQuery(id+"F0.wireOp",EDGE,"bd8de719-41a1-4bd0-8081-9c1217f6791c"),sQuery(id+"F0.wireOp",EDGE,"006f0c99-338c-4f36-b08f-c77e49a0fbad"),sQuery(id+"F0.wireOp",EDGE,"c6bfb2f8-91ac-4f7d-96ed-f06fe387df6e"),sQuery(id+"F0.wireOp",EDGE,"17ee62eb-b815-428a-b96c-02ce3f13adcb"),sQuery(id+"F0.wireOp",EDGE,"e2444381-855a-4f0f-b36b-fa641b87d2d9"),sQuery(id+"F0.wireOp",EDGE,"cefcb511-22d9-4a09-8e68-20cc47fd51b8"),sQuery(id+"F0.wireOp",EDGE,"1b4dc11c-ad53-41b3-9f2b-c9ab2159d558"),sQuery(id+"F0.wireOp",EDGE,"22eee332-1fd1-4251-85cd-418106cf4375"),sQuery(id+"F0.wireOp",EDGE,"84f580c0-643a-4f0a-9138-4e82baa37bac"),sQuery(id+"F0.wireOp",EDGE,"2086a38c-e74c-4a06-b99b-f26b8d01a979"),sQuery(id+"F0.wireOp",EDGE,"d83b5a14-96ed-4fac-8959-51fcf7670e97"),sQuery(id+"F0.wireOp",EDGE,"2c74cf45-521b-4012-a9bf-3b6af9be1117"),sQuery(id+"F0.wireOp",EDGE,"ec506c91-6b42-4a2e-b46e-7c65f90ec31b"),sQuery(id+"F0.wireOp",EDGE,"3211954a-1ccd-4666-9e85-f34d62337c7a"),sQuery(id+"F0.wireOp",EDGE,"a3f67027-3a5e-4afe-b728-b5c4fa98ced0"),sQuery(id+"F0.wireOp",EDGE,"5d943437-c8fc-4969-be62-097ac526ded0"),sQuery(id+"F0.wireOp",EDGE,"06eaccc8-6e93-4f7e-8cfb-ee9c0d61cdc3"),sQuery(id+"F0.wireOp",EDGE,"120e285d-05a4-47e4-8683-9851670f8bb2"),sQuery(id+"F0.wireOp",EDGE,"bf81dcde-89c3-4c8c-8c75-b117a7b5e3d3"),sQuery(id+"F0.wireOp",EDGE,"12e0389e-09b0-48ee-a7f9-ef9ff7f71945"),sQuery(id+"F0.wireOp",EDGE,"51ad4ef6-65b6-46bc-b885-fdb47c514399"),sQuery(id+"F0.wireOp",EDGE,"38302d2c-e7fa-42bb-8c2c-be1136b57425"),sQuery(id+"F0.wireOp",EDGE,"aae20131-0b01-4595-b766-2af5648bae41"),sQuery(id+"F0.wireOp",EDGE,"ff5e1e80-4d6d-4328-a7e5-09995feede13"),sQuery(id+"F0.wireOp",EDGE,"02f12ae7-4dac-4e05-baab-76bbc31f51d9"),sQuery(id+"F0.wireOp",EDGE,"c2b7a8aa-d6f4-4ac0-9869-cc6bc6c287bc"),sQuery(id+"F0.wireOp",EDGE,"45f12263-a6d9-4ecd-a114-8398d307cda3"),sQuery(id+"F0.wireOp",EDGE,"eb4b2e3f-b314-4eb8-b66d-11d848cd9702"),sQuery(id+"F0.wireOp",EDGE,"d08e2fc3-db97-4518-af14-f57cd42bdb93"),sQuery(id+"F0.wireOp",EDGE,"c62695bf-9d10-4615-8556-b32945b0495b"),sQuery(id+"F0.wireOp",EDGE,"c974918c-ca22-4d76-9fc0-f96eec3cc436"),sQuery(id+"F0.wireOp",EDGE,"739d5020-6a0f-40cd-9f13-bcc5e6579085"),sQuery(id+"F0.wireOp",EDGE,"d4ec54ec-8324-4187-bba3-6aecab79e170"),sQuery(id+"F0.wireOp",EDGE,"306571b7-6b24-4c4c-a1c8-bfbc87d8905f"),sQuery(id+"F0.wireOp",EDGE,"f66ff50e-4ff1-48f0-8e8d-b7cf5b2a040a"),sQuery(id+"F0.wireOp",EDGE,"daf886da-2a84-4116-9424-664d25639f25"),sQuery(id+"F0.wireOp",EDGE,"067ee87a-2aaa-42c3-8fb6-e2e8e96a65df"),sQuery(id+"F0.wireOp",EDGE,"ddc883ec-767f-41b6-97ba-04dab902a0f4"),sQuery(id+"F0.wireOp",EDGE,"6abd8343-adbf-41c6-bb61-28074b4141f7"),sQuery(id+"F0.wireOp",EDGE,"303af2a4-8efc-4f4f-8ef3-d8f9148a8597"),sQuery(id+"F0.wireOp",EDGE,"9414ef44-f5ad-4d2e-a9d7-60932f4a20b1"),sQuery(id+"F0.wireOp",EDGE,"a0eeebb4-cc0f-4106-8cb1-e05a2e0a416f"),sQuery(id+"F0.wireOp",EDGE,"833a10bb-8592-4c3c-aee3-bfd569ec0f1e"),sQuery(id+"F0.wireOp",EDGE,"d0e442e8-2bba-4cf9-ab30-0e0386a8b8c2"),sQuery(id+"F0.wireOp",EDGE,"f987d9c6-208e-44db-b218-8dae03262d6f"),sQuery(id+"F0.wireOp",EDGE,"a26ca596-7ea9-4bee-a4df-367a95f3e545"),sQuery(id+"F0.wireOp",EDGE,"a5779ebb-c89d-4458-a00c-c9e01f5b5973"),sQuery(id+"F0.wireOp",EDGE,"f21783b2-21b3-468f-8d5d-5263caad2514"),sQuery(id+"F0.wireOp",EDGE,"edba20ce-ecb9-41bd-8226-28e95ef654d1"),sQuery(id+"F0.wireOp",EDGE,"a622b662-2178-4b95-ae14-f0ed84f39c17"),sQuery(id+"F0.wireOp",EDGE,"73587eb3-d81d-4fa9-aa56-62cfa1226ee6"),sQuery(id+"F0.wireOp",EDGE,"9a12fa1e-3112-4fb3-adbb-7adcbcf8620f"),sQuery(id+"F0.wireOp",EDGE,"103ca987-9e5f-43ff-aa0a-574345280784"),sQuery(id+"F0.wireOp",EDGE,"9bd448d9-35ad-43e2-ac07-9bb9ad8870f2"),sQuery(id+"F0.wireOp",EDGE,"2ffa967b-18d4-412e-a01b-3b78a495819e"),sQuery(id+"F0.wireOp",EDGE,"50512464-5ca0-4e4d-9ae7-1cc1055f42f2"),sQuery(id+"F0.wireOp",EDGE,"c461c4d4-4af2-42d4-948b-4ec19580dc35"),sQuery(id+"F0.wireOp",EDGE,"ecb23eb1-81de-4115-9db0-b2c109522bad"),sQuery(id+"F0.wireOp",EDGE,"4c41dc37-22eb-489d-a716-cc0c36f39e95"),sQuery(id+"F0.wireOp",EDGE,"78542c54-9d7a-4f83-a58d-da9691bdaca0"),sQuery(id+"F0.wireOp",EDGE,"6dbbe76f-bf3e-4459-9c72-c7ecb79f2599"),sQuery(id+"F0.wireOp",EDGE,"d2964659-1095-4c41-a85d-04ecb1e67d22"),sQuery(id+"F0.wireOp",EDGE,"be7ebe09-106f-435e-9153-6aa01453df74"),sQuery(id+"F0.wireOp",EDGE,"1c04703e-f2a3-4c8c-ae07-315639060602"),sQuery(id+"F0.wireOp",EDGE,"bb0df9f3-41ec-4b74-ae8c-d248db3bbda1"),sQuery(id+"F0.wireOp",EDGE,"a4d25204-afd0-4585-8e65-b7bdd4d03f70"),sQuery(id+"F0.wireOp",EDGE,"dd3ddbf8-632f-40d4-bba2-cd38dc60813c"),sQuery(id+"F0.wireOp",EDGE,"f82e9a7c-f7cf-4e8e-a293-8f428050ee04"),sQuery(id+"F0.wireOp",EDGE,"1d33b62b-690b-4d89-a4f2-b31df673149d"),sQuery(id+"F0.wireOp",EDGE,"1c9a8537-1b75-4561-8014-5d0839793d83"),sQuery(id+"F0.wireOp",EDGE,"7da6752e-0130-4427-b37a-f870623fd533"),sQuery(id+"F0.wireOp",EDGE,"3b50b7bf-802d-4722-b69f-b634c0ebe5fd"),sQuery(id+"F0.wireOp",EDGE,"509ff239-90b6-4fbe-bb57-96526ffbb594"),sQuery(id+"F0.wireOp",EDGE,"180e4fda-fba7-4278-9c24-33e623ce9905"),sQuery(id+"F0.wireOp",EDGE,"5920d0c8-b25e-4683-9891-726beeda9f14"),sQuery(id+"F0.wireOp",EDGE,"abb53ec4-693b-4cd8-8f90-21607318ac32"),sQuery(id+"F0.wireOp",EDGE,"813c9ebf-de40-4e0c-8072-1ce01e70ffae"),sQuery(id+"F0.wireOp",EDGE,"b26c0b99-29b3-4a19-abc5-54117a970742"),sQuery(id+"F0.wireOp",EDGE,"a5e9c79b-3b52-4ba9-b521-4fd20c288a4b"),sQuery(id+"F0.wireOp",EDGE,"d593f28c-d403-4033-af98-9880a669a0ee"),sQuery(id+"F0.wireOp",EDGE,"ad8c2ee1-1e38-4b18-b284-f762253671aa"),sQuery(id+"F0.wireOp",EDGE,"07aa20d9-5bd4-4cae-ac57-1fae0daa92e8"),sQuery(id+"F0.wireOp",EDGE,"d565bab9-d083-4930-9dc6-341856c6dcaf"),sQuery(id+"F0.wireOp",EDGE,"2738d55d-88fc-4993-8ec1-37b5a04e9b08"),sQuery(id+"F0.wireOp",EDGE,"05dced37-4d0f-41bf-8a2d-c997782e87b9"),sQuery(id+"F0.wireOp",EDGE,"4d017246-123a-4de1-a35e-6b362acbbedb"),sQuery(id+"F0.wireOp",EDGE,"37e57022-df8f-4a31-bc96-a8043f81fc3f"),sQuery(id+"F0.wireOp",EDGE,"7123fb36-b773-4292-8fcd-0f0684e2f7f6"),sQuery(id+"F0.wireOp",EDGE,"aa0e7ec4-3259-498c-b15d-b162ee01d909"),sQuery(id+"F0.wireOp",EDGE,"f394ea13-b473-4e84-ae02-2efceabd8e74"),sQuery(id+"F0.wireOp",EDGE,"34b7ddd7-5b87-432e-b0b2-8a4cecb90ba6"),sQuery(id+"F0.wireOp",EDGE,"86ca4e61-c620-4993-9e47-07488580a3c8"),sQuery(id+"F0.wireOp",EDGE,"f85c54f4-142e-4dc0-8ec6-8fc11b01442e"),sQuery(id+"F0.wireOp",EDGE,"43d2117f-53fe-44c9-885d-8f9cb5c2990c"),sQuery(id+"F0.wireOp",EDGE,"485bfe38-7d02-4abe-acaf-2e8422fab976"),sQuery(id+"F0.wireOp",EDGE,"4ad0de0c-3400-43fa-8625-8bf83bad5eba"),sQuery(id+"F0.wireOp",EDGE,"c9e7e1b8-322b-4c7c-8131-a25f5d484d37"),sQuery(id+"F0.wireOp",EDGE,"5f31f1f6-d40e-4c76-871f-efbf29229a10"),sQuery(id+"F0.wireOp",EDGE,"2341f378-6e8a-4808-bdda-5107740a4e72"),sQuery(id+"F0.wireOp",EDGE,"70fe7bf2-e18c-4a39-8663-7adb9fa09552"),sQuery(id+"F0.wireOp",EDGE,"3f01cd6a-3bf0-4465-b004-29128bb7135e"),sQuery(id+"F0.wireOp",EDGE,"c3540aa0-e260-4d56-98ac-be03f425b991"),sQuery(id+"F0.wireOp",EDGE,"0c9aeb50-b92f-42b1-a69e-a05d9f1eef4b"),sQuery(id+"F0.wireOp",EDGE,"fa91054d-bcef-47a6-8191-f95e63a7ac50"),sQuery(id+"F0.wireOp",EDGE,"7f7d0cc8-3f6c-4f55-98b7-40bdad5a5afc"),sQuery(id+"F0.wireOp",EDGE,"fda22a44-1e0c-4b5e-9f56-731edba39066"),sQuery(id+"F0.wireOp",EDGE,"8c888383-5152-4466-85ac-be87ccfda324"),sQuery(id+"F0.wireOp",EDGE,"3f7d6ee0-d9af-44ae-8c14-3c3c63bc35cd"),sQuery(id+"F0.wireOp",EDGE,"a11b762e-5c35-4478-b634-c0bde5372c59"),sQuery(id+"F0.wireOp",EDGE,"4ef27dc0-3f8a-4abf-bc82-3e658e9b4576"),sQuery(id+"F0.wireOp",EDGE,"ff7e588e-b80d-4494-b928-8aead235ba6b"),sQuery(id+"F0.wireOp",EDGE,"2f726558-5d46-44a5-8890-013a8af2fb6d"),sQuery(id+"F0.wireOp",EDGE,"4da7e619-5ec9-4c30-9fa9-5e8f818b586c"),sQuery(id+"F0.wireOp",EDGE,"fcb5bf59-f724-40bf-a93c-df29265e678e"),sQuery(id+"F0.wireOp",EDGE,"ebd3fb46-ade7-45fe-a8b2-4135c87953cc"),sQuery(id+"F0.wireOp",EDGE,"56209d7f-2321-400e-b666-842f0e323caf"),sQuery(id+"F0.wireOp",EDGE,"25070fa3-85a9-410d-a013-5a2437b870fd"),sQuery(id+"F0.wireOp",EDGE,"f10a09fe-5d46-4890-8871-337437fb93b1"),sQuery(id+"F0.wireOp",EDGE,"4bc09a70-5109-48c9-801e-a94224323d17"),sQuery(id+"F0.wireOp",EDGE,"bedb624d-55d7-49c3-a1e0-22580057bb39"),sQuery(id+"F0.wireOp",EDGE,"0ff46ae1-5ded-439e-b620-fa5599d96111"),sQuery(id+"F0.wireOp",EDGE,"746c5437-ba77-4817-9a45-636baa4d7b89"),sQuery(id+"F0.wireOp",EDGE,"4e907761-c308-486b-9933-48f3b43f4659"),sQuery(id+"F0.wireOp",EDGE,"c96bf18e-c1b0-4b95-ba17-1090479d2ea4"),sQuery(id+"F0.wireOp",EDGE,"190744f1-0e0c-43b1-8c51-d393dd3d4bf0"),sQuery(id+"F0.wireOp",EDGE,"8722c152-edc4-4c89-9289-79d72895c7fa"),sQuery(id+"F0.wireOp",EDGE,"3c1c7ed6-fc64-499f-aee9-3418b705639d"),sQuery(id+"F0.wireOp",EDGE,"e2badb26-cb38-44ca-bc58-92e3de63b6f8"),sQuery(id+"F0.wireOp",EDGE,"2ccd0fef-846d-485e-804d-85fdd7b21415"),sQuery(id+"F0.wireOp",EDGE,"85cf3f22-8d95-46a4-b412-cc8e0c5a1e7a"),sQuery(id+"F0.wireOp",EDGE,"36c562ca-cf81-40b6-8890-c98833280bba"),sQuery(id+"F0.wireOp",EDGE,"e0cb2875-ac02-492d-b256-83296656fbeb"),sQuery(id+"F0.wireOp",EDGE,"02052b0a-9100-4e6c-8e1d-81c2f94f8ffa"),sQuery(id+"F0.wireOp",EDGE,"42df54ce-8481-4a71-8046-98704643b0b8"),sQuery(id+"F0.wireOp",EDGE,"7d6679e0-59e7-45b7-9956-405c4ffd710a"),sQuery(id+"F0.wireOp",EDGE,"fe945fd7-80c7-4a7e-93bf-5150c6aec338"),sQuery(id+"F0.wireOp",EDGE,"1dcfdb14-3700-4d18-a8f8-4ecdd2d41f12"),sQuery(id+"F0.wireOp",EDGE,"705f835e-1fbe-4103-b21d-6b115d2ce59e"),sQuery(id+"F0.wireOp",EDGE,"1242c965-2a33-4cf4-b701-2917b13ae1b8"),sQuery(id+"F0.wireOp",EDGE,"a5eeb873-3ee8-44b6-92a4-21f573f1c98c"),sQuery(id+"F0.wireOp",EDGE,"2d139e89-6815-4495-b2ea-2cbbc5575223"),sQuery(id+"F0.wireOp",EDGE,"aa6f62da-9d95-44b1-b52b-a1dff2773bd8"),sQuery(id+"F0.wireOp",EDGE,"75387c55-516f-4644-8b3b-9b516fb984a2"),sQuery(id+"F0.wireOp",EDGE,"ddf068c2-fc09-4641-afa0-0f5eaafe47ec"),sQuery(id+"F0.wireOp",EDGE,"3fdf4c86-ea1b-4bb5-99ec-3044a5813809"),sQuery(id+"F0.wireOp",EDGE,"5dbeab65-f886-48b0-9603-43f0bd103a7a"),sQuery(id+"F0.wireOp",EDGE,"bbd39671-8956-48ac-a72d-beded71640e3"),sQuery(id+"F0.wireOp",EDGE,"e77ea1f8-953c-47da-b36d-ca7a301c01ec"),sQuery(id+"F0.wireOp",EDGE,"8748b016-ffa4-4c71-88e1-d567d17d5198"),sQuery(id+"F0.wireOp",EDGE,"d3885277-1971-4b19-9ac9-64ab6c618bc0"),sQuery(id+"F0.wireOp",EDGE,"1d5b33b2-dc5e-4819-8418-4f5d255eada3"),sQuery(id+"F0.wireOp",EDGE,"53c6b902-1589-40b8-a2a8-924550e61899"),sQuery(id+"F0.wireOp",EDGE,"a4db1815-eabd-4298-8b98-d81d9f414654"),sQuery(id+"F0.wireOp",EDGE,"7ccf15cb-d623-48c6-836d-0b64923c78d9"),sQuery(id+"F0.wireOp",EDGE,"f71362ce-a68a-4497-bfb9-c90ba9a9a06d"),sQuery(id+"F0.wireOp",EDGE,"f5f496dc-b8cc-4076-94d0-883d7f4b94be"),sQuery(id+"F0.wireOp",EDGE,"3263564a-85b9-4823-bd02-bd909b4da241"),sQuery(id+"F0.wireOp",EDGE,"dfa4bfc6-23ff-482a-a434-893fba50a0aa"),sQuery(id+"F0.wireOp",EDGE,"b9215695-43ae-4451-99d5-ffe407fba4aa"),sQuery(id+"F0.wireOp",EDGE,"473c03a6-dac4-4c92-a095-a18eac8fe6a6"),sQuery(id+"F0.wireOp",EDGE,"cc3ff233-c542-49b7-b684-f947dfd8172b"),sQuery(id+"F0.wireOp",EDGE,"064e2064-593c-4fc2-921b-2133a0986bff"),sQuery(id+"F0.wireOp",EDGE,"396f3095-e9ca-42c8-af0d-c1332b2e9ef9"),sQuery(id+"F0.wireOp",EDGE,"02fbb41d-a8d0-4158-aa86-64ef3c6d3f14"),sQuery(id+"F0.wireOp",EDGE,"518c1aec-a62b-465e-a6a8-a967ccc4b83a"),sQuery(id+"F0.wireOp",EDGE,"c7a2f402-6181-4b7b-8d39-9280429ff77b"),sQuery(id+"F0.wireOp",EDGE,"e06369f8-15d1-44c5-a9a6-487333b74079"),sQuery(id+"F0.wireOp",EDGE,"26e4f6d5-62c8-4aa5-8607-ad2b8a46218f"),sQuery(id+"F0.wireOp",EDGE,"bdb62519-c26f-4ca3-baef-fd5674aaa98a"),sQuery(id+"F0.wireOp",EDGE,"971deac8-02f9-4881-b096-68b0ed0d4ef7"),sQuery(id+"F0.wireOp",EDGE,"b3f6c54e-5ba1-4c9b-ab06-ff887e18d623"),sQuery(id+"F0.wireOp",EDGE,"bc4118e7-aed3-4703-bd36-447b393dc447"),sQuery(id+"F0.wireOp",EDGE,"b6e16d75-1139-4565-a286-e25bf0e1bcdf"),sQuery(id+"F0.wireOp",EDGE,"178e5208-0863-4cd4-91e8-2138fb17df43"),sQuery(id+"F0.wireOp",EDGE,"242c819c-d2d4-4f54-b000-3f41bc7bb28f"),sQuery(id+"F0.wireOp",EDGE,"aa0c8438-6628-4c13-985f-6c061554a2b8"),sQuery(id+"F0.wireOp",EDGE,"1d5657ee-30c5-40a6-b1f7-e46671814f9d"),sQuery(id+"F0.wireOp",EDGE,"89862b55-cfd9-41c4-8538-90352b786acf"),sQuery(id+"F0.wireOp",EDGE,"6d4d03d1-366e-4660-a0cd-9d8c123db2be"),sQuery(id+"F0.wireOp",EDGE,"c7f4da4b-8bf6-4229-b33b-0c2485b95d48"),sQuery(id+"F0.wireOp",EDGE,"6d885470-fe4d-471c-95d8-4ec8cfa82da0"),sQuery(id+"F0.wireOp",EDGE,"70f1da3a-ddbb-403f-9bf6-b954922d633b"),sQuery(id+"F0.wireOp",EDGE,"42f39b82-c81f-4697-95fb-0b881859a8a2"),sQuery(id+"F0.wireOp",EDGE,"feea9f10-177f-45ef-a5df-3751a5c51f57"),sQuery(id+"F0.wireOp",EDGE,"2b39117d-e2b6-4d35-b755-85c4c1d22e1d"),sQuery(id+"F0.wireOp",EDGE,"ae0a4542-48c9-469c-99b3-d2f52b71f71f"),sQuery(id+"F0.wireOp",EDGE,"72595a4a-4346-4881-bee9-ca404737387e"),sQuery(id+"F0.wireOp",EDGE,"14b5bf1a-39dc-40ed-8199-11cb1830c68e"),sQuery(id+"F0.wireOp",EDGE,"0bfe0592-e2e8-4af9-80f1-74eddb094739"),sQuery(id+"F0.wireOp",EDGE,"33585b95-de89-4a61-bb0b-ac5138497490"),sQuery(id+"F0.wireOp",EDGE,"894fff80-6bd1-4132-98f4-3cb2a154478e"),sQuery(id+"F0.wireOp",EDGE,"a9a1f528-d001-478a-bc5e-ea06366b1f05"),sQuery(id+"F0.wireOp",EDGE,"b5cf05b1-a568-4638-9b13-410cc4bc705c"),sQuery(id+"F0.wireOp",EDGE,"575f58e5-487a-4d60-baf1-e0db31fd321a"),sQuery(id+"F0.wireOp",EDGE,"f3a809c4-9690-428d-8479-f2fa9284ce6b"),sQuery(id+"F0.wireOp",EDGE,"d1e57e56-9c87-4890-8112-93c7570c70d7"),sQuery(id+"F0.wireOp",EDGE,"349ce66a-3db0-49cb-96e9-97a6d89fbc4d"),sQuery(id+"F0.wireOp",EDGE,"5c9da6b2-d180-497b-b97e-deabef8640d3"),sQuery(id+"F0.wireOp",EDGE,"2f043225-655c-442f-9d8f-b6a2f70d4b03"),sQuery(id+"F0.wireOp",EDGE,"94c5ddf2-0c98-4712-bc72-b26255c7299f"),sQuery(id+"F0.wireOp",EDGE,"2dc2b231-bbb2-44d1-98ad-6d2b5150722c"),sQuery(id+"F0.wireOp",EDGE,"13ad8273-b4b0-4d43-8538-38813206fd37"),sQuery(id+"F0.wireOp",EDGE,"8e789429-8ed4-4dff-93cc-045b934299c7"),sQuery(id+"F0.wireOp",EDGE,"f83dc63d-c536-418d-8ff6-15ed4a67131c"),sQuery(id+"F0.wireOp",EDGE,"545a6082-df20-4000-9aec-469e0704e975"),sQuery(id+"F0.wireOp",EDGE,"6d43a2d7-c5d1-4781-8dd1-de1db427477f"),sQuery(id+"F0.wireOp",EDGE,"43346fda-c566-488d-bb9f-6b789724eb50"),sQuery(id+"F0.wireOp",EDGE,"3e33d1c3-4071-42e1-9b79-df7bd7c71772"),sQuery(id+"F0.wireOp",EDGE,"b48248fd-b1ae-40b5-9e05-179f10cb075e"),sQuery(id+"F0.wireOp",EDGE,"5c7ebee7-e2b9-43e7-a82d-2389181e45b6"),sQuery(id+"F0.wireOp",EDGE,"404b9876-64bd-4bbc-90bf-2fc5da104a34"),sQuery(id+"F0.wireOp",EDGE,"06ebbb02-787e-4143-ae9c-e3cbd7a8c154"),sQuery(id+"F0.wireOp",EDGE,"821b92c1-2619-49da-9b0d-ba297cd6e38f"),sQuery(id+"F0.wireOp",EDGE,"844f7900-f3e8-45c8-8f9f-ec53237987de"),sQuery(id+"F0.wireOp",EDGE,"84eae196-ac68-4b45-815c-071479414627"),sQuery(id+"F0.wireOp",EDGE,"38ef94d1-dd75-4327-8098-016537463e24"),sQuery(id+"F0.wireOp",EDGE,"3c68abc3-dbc1-41cd-95bc-adec34724420"),sQuery(id+"F0.wireOp",EDGE,"175ec536-30cf-41bd-a682-57c7ab263180"),sQuery(id+"F0.wireOp",EDGE,"03bf834c-4b32-4328-b738-e017deda3571"),sQuery(id+"F0.wireOp",EDGE,"ebb97727-067f-473b-9b10-5fa6536e91a5"),sQuery(id+"F0.wireOp",EDGE,"fd163ead-baf0-4f25-a181-ac9c4aeace96"),sQuery(id+"F0.wireOp",EDGE,"05110ed8-dca7-4657-bdfc-32fd2defdcdb"),sQuery(id+"F0.wireOp",EDGE,"eb66f918-b69f-4904-8110-244684e40e99"),sQuery(id+"F0.wireOp",EDGE,"1f50ed4f-aa0d-4214-b223-064127cfafa5"),sQuery(id+"F0.wireOp",EDGE,"0d0165e5-049c-4ae0-8c6d-8400a7fc5d8b"),sQuery(id+"F0.wireOp",EDGE,"d9807aa4-4b74-4160-a8e8-c54f11348bec"),sQuery(id+"F0.wireOp",EDGE,"81bfc8a4-15dd-4bbc-a8de-7a6c49e89916"),sQuery(id+"F0.wireOp",EDGE,"d66dc645-2368-40f7-becf-0aa6712a8649"),sQuery(id+"F0.wireOp",EDGE,"b352bede-2f15-479d-83fd-bc3384d0b56c"),sQuery(id+"F0.wireOp",EDGE,"8a19aa2d-6d55-4ce0-97c0-baceea353766"),sQuery(id+"F0.wireOp",EDGE,"5f8e2f8c-074f-427b-973f-8d3ac7b5bbe8"),sQuery(id+"F0.wireOp",EDGE,"292625e9-1ce5-46a4-904c-f6854a7df383"),sQuery(id+"F0.wireOp",EDGE,"93cafe31-8154-4f90-bb1d-95a543f886ac"),sQuery(id+"F0.wireOp",EDGE,"9d6a5dd0-845d-4112-9f54-ebe0abe60735"),sQuery(id+"F0.wireOp",EDGE,"8a4db5ef-2743-479f-8098-9e3fcaae686a"),sQuery(id+"F0.wireOp",EDGE,"ca465e90-126a-4816-9119-d4150e6154a3"),sQuery(id+"F0.wireOp",EDGE,"E0"),sQuery(id+"F0.wireOp",EDGE,"af9dac12-ede5-4d6b-b329-3218d4e3a3d9.trimOffspring"),sQuery(id+"F0.wireOp",EDGE,"58ee0f98-cb6d-42ad-9831-0537edf5bdb0.trimOffspring"),sQuery(id+"F0.wireOp",EDGE,"117cccf0-6e4c-4dd9-9ce8-7d0eb2480f0d.trimOffspring"),sQuery(id+"F0.wireOp",EDGE,"bcfa5d6f-fb86-4086-82b3-a3f57acfab9d.trimOffspring"),sQuery(id+"F0.wireOp",EDGE,"a21dbb20-baf5-48e9-95c0-79a72f1e8c1b.trimOffspring"),sQuery(id+"F0.wireOp",EDGE,"e45c49fc-26fb-4fd0-8f63-7eae6f12a87e.trimOffspring"),sQuery(id+"F0.wireOp",EDGE,"b814ad12-1d71-4b28-b985-c27c8c5e389f.trimOffspring"),sQuery(id+"F0.wireOp",EDGE,"2c71e4f5-3aaf-49a7-9cd9-7906c17fc5b6.trimOffspring"),sQuery(id+"F0.wireOp",EDGE,"2e0ebafb-e982-4014-ab51-e9b40ec535c4.trimOffspring"),sQuery(id+"F0.wireOp",EDGE,"ffa78a0e-e73a-4c7c-a233-faf7876c79e0.trimOffspring"),sQuery(id+"F0.wireOp",EDGE,"5ae34624-9dc0-4140-9c26-527617327f6f.trimOffspring"),sQuery(id+"F0.wireOp",EDGE,"f635a409-f61b-4649-9e31-d42e7781e6f4.trimOffspring"),sQuery(id+"F0.wireOp",EDGE,"07e56e10-4129-4a8e-825d-56220bd91938.trimOffspring"),sQuery(id+"F0.wireOp",EDGE,"6bba4f67-e4ba-4e85-94e1-08bcb743ed3f.trimOffspring"),sQuery(id+"F0.wireOp",EDGE,"5826d8d4-b774-450b-9d76-56fb2635cf42.trimOffspring"),sQuery(id+"F0.wireOp",EDGE,"d3ac0e20-25c0-4450-adcd-7930d79a125d.trimOffspring"),sQuery(id+"F0.wireOp",EDGE,"460eded8-94ea-42c9-bb5c-95c891dcb47a.trimOffspring"),sQuery(id+"F0.wireOp",EDGE,"6bf81d76-93cb-4871-b2e8-8002e1628139.trimOffspring"),sQuery(id+"F0.wireOp",EDGE,"6b65a889-62aa-4a71-aefc-0fdc80f9fbd7.trimOffspring"),sQuery(id+"F0.wireOp",EDGE,"492cef29-5c9f-43bb-9a21-f4b26ab4c56d.trimOffspring"),sQuery(id+"F0.wireOp",EDGE,"ec42e2a7-4c47-4e2f-8ead-93cad2025480.trimOffspring"),sQuery(id+"F0.wireOp",EDGE,"a26ede43-7a92-4ef9-9b65-5d6345ae6e2d.trimOffspring"),sQuery(id+"F0.wireOp",EDGE,"74509194-0070-41ec-8664-167cdb64098b.trimOffspring"),sQuery(id+"F0.wireOp",EDGE,"356a243f-46d5-4ba5-b8e6-9c60b8afb371.trimOffspring"),sQuery(id+"F0.wireOp",EDGE,"44432cc4-0e61-452d-8d9f-c2c31a2a2b76.trimOffspring"),sQuery(id+"F0.wireOp",EDGE,"083761ce-7f6a-4772-a0b6-42da9d9a583c.trimOffspring"),sQuery(id+"F0.wireOp",EDGE,"76966a8d-6096-4b7e-843c-87f34c569aca.trimOffspring"),sQuery(id+"F0.wireOp",EDGE,"fdc08ff0-62e3-4f0b-8448-a5e6ce257c64.trimOffspring"),sQuery(id+"F0.wireOp",EDGE,"0763c2a9-43d9-4018-9a8d-0e270b08ccc4"),sQuery(id+"F0.wireOp",EDGE,"adbb0289-b1bd-468f-a573-d0a6248d6679"),sQuery(id+"F0.wireOp",EDGE,"e802149e-0d3e-4a98-83d7-5df97ce44949.trimOffspring"),sQuery(id+"F0.wireOp",EDGE,"E1"),sQuery(id+"F0.wireOp",EDGE,"E2"),sQuery(id+"F0.wireOp",EDGE,"E3"),sQuery(id+"F0.wireOp",EDGE,"E4"),sQuery(id+"F0.wireOp",EDGE,"EA74iWvD-8oKk-ivYR-DS7W-3RoOPZgJlXoF"),sQuery(id+"F0.wireOp",EDGE,"OAE0uyU3-7MVm-HVLp-ilHf-uihLfXUpzug4")])],"isStart":false});
            var sketch = newSketch(context, id + "F2", { "sketchPlane" : qUnion([Q0])});
            skPoint(sketch, "E1253.center", {"position": v(0, 0) * mm});
            skCircle(sketch, "E1254.0", {"center": v(0, 0) * mm, "radius": 57.15 * mm, "construction": true});
            skCircle(sketch, "E1255.0", {"center": v(0, -50.8) * mm, "radius": 1.59 * mm});
            skCircle(sketch, "E1256.0", {"center": v(0, 50.8) * mm, "radius": 1.59 * mm});
            skCircle(sketch, "E1257.0", {"center": v(50.8, 0) * mm, "radius": 1.59 * mm});
            skCircle(sketch, "E1258.0", {"center": v(-50.8, 0) * mm, "radius": 1.59 * mm});
            skCircle(sketch, "E1259.0", {"center": v(0, 6.35) * mm, "radius": 1.59 * mm});
            skCircle(sketch, "E1260.0", {"center": v(0, -6.35) * mm, "radius": 1.59 * mm});
            skLineSegment(sketch, "E1261", {"start": v(-32.58, 3.38) * mm, "end": v(-30.04, 3.3) * mm});
            skLineSegment(sketch, "E1262", {"start": v(-30.04, 3.3) * mm, "end": v(-30.18, -1.6) * mm});
            skLineSegment(sketch, "E1263", {"start": v(-32.72, -1.53) * mm, "end": v(-30.18, -1.6) * mm});
            skLineSegment(sketch, "E1264", {"start": v(-32.58, 3.38) * mm, "end": v(-32.72, -1.53) * mm});
            skLineSegment(sketch, "E1265.1.0", {"start": v(-32.57, -3.47) * mm, "end": v(-31.69, -8.3) * mm});
            skLineSegment(sketch, "E1265.1.1", {"start": v(-31.69, -8.3) * mm, "end": v(-29.19, -7.85) * mm});
            skLineSegment(sketch, "E1265.1.2", {"start": v(-30.08, -3) * mm, "end": v(-29.19, -7.85) * mm});
            skLineSegment(sketch, "E1265.1.3", {"start": v(-32.57, -3.47) * mm, "end": v(-30.08, -3) * mm});
            skLineSegment(sketch, "E1265.2.0", {"start": v(-31.14, -10.16) * mm, "end": v(-29.27, -14.71) * mm});
            skLineSegment(sketch, "E1265.2.1", {"start": v(-29.27, -14.71) * mm, "end": v(-26.92, -13.74) * mm});
            skLineSegment(sketch, "E1265.2.2", {"start": v(-28.8, -9.2) * mm, "end": v(-26.92, -13.74) * mm});
            skLineSegment(sketch, "E1265.2.3", {"start": v(-31.14, -10.16) * mm, "end": v(-28.8, -9.2) * mm});
            skLineSegment(sketch, "E1265.3.0", {"start": v(-28.35, -16.42) * mm, "end": v(-25.57, -20.48) * mm});
            skLineSegment(sketch, "E1265.3.1", {"start": v(-25.57, -20.48) * mm, "end": v(-23.47, -19.04) * mm});
            skLineSegment(sketch, "E1265.3.2", {"start": v(-26.25, -14.98) * mm, "end": v(-23.47, -19.04) * mm});
            skLineSegment(sketch, "E1265.3.3", {"start": v(-28.35, -16.42) * mm, "end": v(-26.25, -14.98) * mm});
            skLineSegment(sketch, "E1265.4.0", {"start": v(-24.32, -21.95) * mm, "end": v(-20.76, -25.34) * mm});
            skLineSegment(sketch, "E1265.4.1", {"start": v(-20.76, -25.34) * mm, "end": v(-19, -23.5) * mm});
            skLineSegment(sketch, "E1265.4.2", {"start": v(-22.56, -20.11) * mm, "end": v(-19, -23.5) * mm});
            skLineSegment(sketch, "E1265.4.3", {"start": v(-24.32, -21.95) * mm, "end": v(-22.56, -20.11) * mm});
            skLineSegment(sketch, "E1265.5.0", {"start": v(-19.22, -26.53) * mm, "end": v(-15.03, -29.1) * mm});
            skLineSegment(sketch, "E1265.5.1", {"start": v(-15.03, -29.1) * mm, "end": v(-13.7, -26.94) * mm});
            skLineSegment(sketch, "E1265.5.2", {"start": v(-17.89, -24.36) * mm, "end": v(-13.7, -26.94) * mm});
            skLineSegment(sketch, "E1265.5.3", {"start": v(-19.22, -26.53) * mm, "end": v(-17.89, -24.36) * mm});
            skLineSegment(sketch, "E1265.6.0", {"start": v(-13.28, -29.94) * mm, "end": v(-8.65, -31.6) * mm});
            skLineSegment(sketch, "E1265.6.1", {"start": v(-8.65, -31.6) * mm, "end": v(-7.8, -29.2) * mm});
            skLineSegment(sketch, "E1265.6.2", {"start": v(-12.43, -27.55) * mm, "end": v(-7.8, -29.2) * mm});
            skLineSegment(sketch, "E1265.6.3", {"start": v(-13.28, -29.94) * mm, "end": v(-12.43, -27.55) * mm});
            skLineSegment(sketch, "E1265.7.0", {"start": v(-6.77, -32.05) * mm, "end": v(-1.9, -32.7) * mm});
            skLineSegment(sketch, "E1265.7.1", {"start": v(-1.9, -32.7) * mm, "end": v(-1.56, -30.19) * mm});
            skLineSegment(sketch, "E1265.7.2", {"start": v(-6.43, -29.53) * mm, "end": v(-1.56, -30.19) * mm});
            skLineSegment(sketch, "E1265.7.3", {"start": v(-6.77, -32.05) * mm, "end": v(-6.43, -29.53) * mm});
            skLineSegment(sketch, "E1265.8.0", {"start": v(0.04, -32.76) * mm, "end": v(4.95, -32.38) * mm});
            skLineSegment(sketch, "E1265.8.1", {"start": v(4.95, -32.38) * mm, "end": v(4.75, -29.85) * mm});
            skLineSegment(sketch, "E1265.8.2", {"start": v(-0.15, -30.23) * mm, "end": v(4.75, -29.85) * mm});
            skLineSegment(sketch, "E1265.8.3", {"start": v(0.04, -32.76) * mm, "end": v(-0.15, -30.23) * mm});
            skLineSegment(sketch, "E1265.9.0", {"start": v(6.85, -32.03) * mm, "end": v(11.57, -30.65) * mm});
            skLineSegment(sketch, "E1265.9.1", {"start": v(11.57, -30.65) * mm, "end": v(10.85, -28.2) * mm});
            skLineSegment(sketch, "E1265.9.2", {"start": v(6.14, -29.6) * mm, "end": v(10.85, -28.2) * mm});
            skLineSegment(sketch, "E1265.9.3", {"start": v(6.85, -32.03) * mm, "end": v(6.14, -29.6) * mm});
            skLineSegment(sketch, "E1265.10.0", {"start": v(13.36, -29.9) * mm, "end": v(17.7, -27.57) * mm});
            skLineSegment(sketch, "E1265.10.1", {"start": v(17.7, -27.57) * mm, "end": v(16.48, -25.34) * mm});
            skLineSegment(sketch, "E1265.10.2", {"start": v(12.16, -27.67) * mm, "end": v(16.48, -25.34) * mm});
            skLineSegment(sketch, "E1265.10.3", {"start": v(13.36, -29.9) * mm, "end": v(12.16, -27.67) * mm});
            skLineSegment(sketch, "E1265.11.0", {"start": v(19.3, -26.48) * mm, "end": v(23.04, -23.3) * mm});
            skLineSegment(sketch, "E1265.11.1", {"start": v(23.04, -23.3) * mm, "end": v(21.4, -21.36) * mm});
            skLineSegment(sketch, "E1265.11.2", {"start": v(17.64, -24.54) * mm, "end": v(21.4, -21.36) * mm});
            skLineSegment(sketch, "E1265.11.3", {"start": v(19.3, -26.48) * mm, "end": v(17.64, -24.54) * mm});
            skLineSegment(sketch, "E1265.12.0", {"start": v(24.37, -21.89) * mm, "end": v(27.38, -18) * mm});
            skLineSegment(sketch, "E1265.12.1", {"start": v(27.38, -18) * mm, "end": v(25.36, -16.44) * mm});
            skLineSegment(sketch, "E1265.12.2", {"start": v(22.36, -20.34) * mm, "end": v(25.36, -16.44) * mm});
            skLineSegment(sketch, "E1265.12.3", {"start": v(24.37, -21.89) * mm, "end": v(22.36, -20.34) * mm});
            skLineSegment(sketch, "E1265.13.0", {"start": v(28.4, -16.34) * mm, "end": v(30.52, -11.9) * mm});
            skLineSegment(sketch, "E1265.13.1", {"start": v(30.52, -11.9) * mm, "end": v(28.23, -10.8) * mm});
            skLineSegment(sketch, "E1265.13.2", {"start": v(26.1, -15.24) * mm, "end": v(28.23, -10.8) * mm});
            skLineSegment(sketch, "E1265.13.3", {"start": v(28.4, -16.34) * mm, "end": v(26.1, -15.24) * mm});
            skLineSegment(sketch, "E1265.14.0", {"start": v(31.17, -10.08) * mm, "end": v(32.33, -5.3) * mm});
            skLineSegment(sketch, "E1265.14.1", {"start": v(32.33, -5.3) * mm, "end": v(29.86, -4.7) * mm});
            skLineSegment(sketch, "E1265.14.2", {"start": v(28.7, -9.48) * mm, "end": v(29.86, -4.7) * mm});
            skLineSegment(sketch, "E1265.14.3", {"start": v(31.17, -10.08) * mm, "end": v(28.7, -9.48) * mm});
            skLineSegment(sketch, "E1265.15.0", {"start": v(32.58, -3.38) * mm, "end": v(32.72, 1.53) * mm});
            skLineSegment(sketch, "E1265.15.1", {"start": v(32.72, 1.53) * mm, "end": v(30.18, 1.6) * mm});
            skLineSegment(sketch, "E1265.15.2", {"start": v(30.04, -3.3) * mm, "end": v(30.18, 1.6) * mm});
            skLineSegment(sketch, "E1265.15.3", {"start": v(32.58, -3.38) * mm, "end": v(30.04, -3.3) * mm});
            skLineSegment(sketch, "E1265.16.0", {"start": v(32.57, 3.47) * mm, "end": v(31.69, 8.3) * mm});
            skLineSegment(sketch, "E1265.16.1", {"start": v(31.69, 8.3) * mm, "end": v(29.19, 7.85) * mm});
            skLineSegment(sketch, "E1265.16.2", {"start": v(30.08, 3) * mm, "end": v(29.19, 7.85) * mm});
            skLineSegment(sketch, "E1265.16.3", {"start": v(32.57, 3.47) * mm, "end": v(30.08, 3) * mm});
            skLineSegment(sketch, "E1265.17.0", {"start": v(31.14, 10.16) * mm, "end": v(29.27, 14.71) * mm});
            skLineSegment(sketch, "E1265.17.1", {"start": v(29.27, 14.71) * mm, "end": v(26.92, 13.74) * mm});
            skLineSegment(sketch, "E1265.17.2", {"start": v(28.8, 9.2) * mm, "end": v(26.92, 13.74) * mm});
            skLineSegment(sketch, "E1265.17.3", {"start": v(31.14, 10.16) * mm, "end": v(28.8, 9.2) * mm});
            skLineSegment(sketch, "E1265.18.0", {"start": v(28.35, 16.42) * mm, "end": v(25.57, 20.48) * mm});
            skLineSegment(sketch, "E1265.18.1", {"start": v(25.57, 20.48) * mm, "end": v(23.47, 19.04) * mm});
            skLineSegment(sketch, "E1265.18.2", {"start": v(26.25, 14.98) * mm, "end": v(23.47, 19.04) * mm});
            skLineSegment(sketch, "E1265.18.3", {"start": v(28.35, 16.42) * mm, "end": v(26.25, 14.98) * mm});
            skLineSegment(sketch, "E1265.19.0", {"start": v(24.32, 21.95) * mm, "end": v(20.76, 25.34) * mm});
            skLineSegment(sketch, "E1265.19.1", {"start": v(20.76, 25.34) * mm, "end": v(19, 23.5) * mm});
            skLineSegment(sketch, "E1265.19.2", {"start": v(22.56, 20.11) * mm, "end": v(19, 23.5) * mm});
            skLineSegment(sketch, "E1265.19.3", {"start": v(24.32, 21.95) * mm, "end": v(22.56, 20.11) * mm});
            skLineSegment(sketch, "E1265.20.0", {"start": v(19.22, 26.53) * mm, "end": v(15.03, 29.1) * mm});
            skLineSegment(sketch, "E1265.20.1", {"start": v(15.03, 29.1) * mm, "end": v(13.7, 26.94) * mm});
            skLineSegment(sketch, "E1265.20.2", {"start": v(17.89, 24.36) * mm, "end": v(13.7, 26.94) * mm});
            skLineSegment(sketch, "E1265.20.3", {"start": v(19.22, 26.53) * mm, "end": v(17.89, 24.36) * mm});
            skLineSegment(sketch, "E1265.21.0", {"start": v(13.28, 29.94) * mm, "end": v(8.65, 31.6) * mm});
            skLineSegment(sketch, "E1265.21.1", {"start": v(8.65, 31.6) * mm, "end": v(7.8, 29.2) * mm});
            skLineSegment(sketch, "E1265.21.2", {"start": v(12.43, 27.55) * mm, "end": v(7.8, 29.2) * mm});
            skLineSegment(sketch, "E1265.21.3", {"start": v(13.28, 29.94) * mm, "end": v(12.43, 27.55) * mm});
            skLineSegment(sketch, "E1265.22.0", {"start": v(6.77, 32.05) * mm, "end": v(1.9, 32.7) * mm});
            skLineSegment(sketch, "E1265.22.1", {"start": v(1.9, 32.7) * mm, "end": v(1.56, 30.19) * mm});
            skLineSegment(sketch, "E1265.22.2", {"start": v(6.43, 29.53) * mm, "end": v(1.56, 30.19) * mm});
            skLineSegment(sketch, "E1265.22.3", {"start": v(6.77, 32.05) * mm, "end": v(6.43, 29.53) * mm});
            skLineSegment(sketch, "E1265.23.0", {"start": v(-0.04, 32.76) * mm, "end": v(-4.95, 32.38) * mm});
            skLineSegment(sketch, "E1265.23.1", {"start": v(-4.95, 32.38) * mm, "end": v(-4.75, 29.85) * mm});
            skLineSegment(sketch, "E1265.23.2", {"start": v(0.15, 30.23) * mm, "end": v(-4.75, 29.85) * mm});
            skLineSegment(sketch, "E1265.23.3", {"start": v(-0.04, 32.76) * mm, "end": v(0.15, 30.23) * mm});
            skLineSegment(sketch, "E1265.24.0", {"start": v(-6.85, 32.03) * mm, "end": v(-11.57, 30.65) * mm});
            skLineSegment(sketch, "E1265.24.1", {"start": v(-11.57, 30.65) * mm, "end": v(-10.85, 28.2) * mm});
            skLineSegment(sketch, "E1265.24.2", {"start": v(-6.14, 29.6) * mm, "end": v(-10.85, 28.2) * mm});
            skLineSegment(sketch, "E1265.24.3", {"start": v(-6.85, 32.03) * mm, "end": v(-6.14, 29.6) * mm});
            skLineSegment(sketch, "E1265.25.0", {"start": v(-13.36, 29.9) * mm, "end": v(-17.7, 27.57) * mm});
            skLineSegment(sketch, "E1265.25.1", {"start": v(-17.7, 27.57) * mm, "end": v(-16.48, 25.34) * mm});
            skLineSegment(sketch, "E1265.25.2", {"start": v(-12.16, 27.67) * mm, "end": v(-16.48, 25.34) * mm});
            skLineSegment(sketch, "E1265.25.3", {"start": v(-13.36, 29.9) * mm, "end": v(-12.16, 27.67) * mm});
            skLineSegment(sketch, "E1265.26.0", {"start": v(-19.3, 26.48) * mm, "end": v(-23.04, 23.3) * mm});
            skLineSegment(sketch, "E1265.26.1", {"start": v(-23.04, 23.3) * mm, "end": v(-21.4, 21.36) * mm});
            skLineSegment(sketch, "E1265.26.2", {"start": v(-17.64, 24.54) * mm, "end": v(-21.4, 21.36) * mm});
            skLineSegment(sketch, "E1265.26.3", {"start": v(-19.3, 26.48) * mm, "end": v(-17.64, 24.54) * mm});
            skLineSegment(sketch, "E1265.27.0", {"start": v(-24.37, 21.89) * mm, "end": v(-27.38, 18) * mm});
            skLineSegment(sketch, "E1265.27.1", {"start": v(-27.38, 18) * mm, "end": v(-25.36, 16.44) * mm});
            skLineSegment(sketch, "E1265.27.2", {"start": v(-22.36, 20.34) * mm, "end": v(-25.36, 16.44) * mm});
            skLineSegment(sketch, "E1265.27.3", {"start": v(-24.37, 21.89) * mm, "end": v(-22.36, 20.34) * mm});
            skLineSegment(sketch, "E1265.28.0", {"start": v(-28.4, 16.34) * mm, "end": v(-30.52, 11.9) * mm});
            skLineSegment(sketch, "E1265.28.1", {"start": v(-30.52, 11.9) * mm, "end": v(-28.23, 10.8) * mm});
            skLineSegment(sketch, "E1265.28.2", {"start": v(-26.1, 15.24) * mm, "end": v(-28.23, 10.8) * mm});
            skLineSegment(sketch, "E1265.28.3", {"start": v(-28.4, 16.34) * mm, "end": v(-26.1, 15.24) * mm});
            skLineSegment(sketch, "E1265.29.0", {"start": v(-31.17, 10.08) * mm, "end": v(-32.33, 5.3) * mm});
            skLineSegment(sketch, "E1265.29.1", {"start": v(-32.33, 5.3) * mm, "end": v(-29.86, 4.7) * mm});
            skLineSegment(sketch, "E1265.29.2", {"start": v(-28.7, 9.48) * mm, "end": v(-29.86, 4.7) * mm});
            skLineSegment(sketch, "E1265.29.3", {"start": v(-31.17, 10.08) * mm, "end": v(-28.7, 9.48) * mm});
            skLineSegment(sketch, "E1266", {"start": v(-15.51, -0.35) * mm, "end": v(-15.46, -1.28) * mm});
            skLineSegment(sketch, "E1267", {"start": v(-15.51, -0.35) * mm, "end": v(-15.56, 0.54) * mm});
            skLineSegment(sketch, "E1268", {"start": v(-15.46, -1.28) * mm, "end": v(-15.42, -2.17) * mm});
            skLineSegment(sketch, "E1269", {"start": v(-15.56, 0.54) * mm, "end": v(-18.1, 0.4) * mm});
            skLineSegment(sketch, "E1270", {"start": v(-15.42, -2.17) * mm, "end": v(-17.95, -2.3) * mm});
            skLineSegment(sketch, "E1271", {"start": v(-17.95, -2.3) * mm, "end": v(-18.1, 0.4) * mm});
            skLineSegment(sketch, "E1272.1.0", {"start": v(-17.08, -5.98) * mm, "end": v(-17.78, -3.36) * mm});
            skLineSegment(sketch, "E1272.1.1", {"start": v(-14.63, -5.33) * mm, "end": v(-17.08, -5.98) * mm});
            skLineSegment(sketch, "E1272.1.2", {"start": v(-15.33, -2.7) * mm, "end": v(-17.78, -3.36) * mm});
            skLineSegment(sketch, "E1272.1.3", {"start": v(-15.1, -3.57) * mm, "end": v(-15.33, -2.7) * mm});
            skLineSegment(sketch, "E1272.1.4", {"start": v(-15.1, -3.57) * mm, "end": v(-14.86, -4.47) * mm});
            skLineSegment(sketch, "E1272.1.5", {"start": v(-14.86, -4.47) * mm, "end": v(-14.63, -5.33) * mm});
            skLineSegment(sketch, "E1272.2.0", {"start": v(-15.47, -9.4) * mm, "end": v(-16.7, -6.99) * mm});
            skLineSegment(sketch, "E1272.2.1", {"start": v(-13.2, -8.25) * mm, "end": v(-15.47, -9.4) * mm});
            skLineSegment(sketch, "E1272.2.2", {"start": v(-14.43, -5.84) * mm, "end": v(-16.7, -6.99) * mm});
            skLineSegment(sketch, "E1272.2.3", {"start": v(-14.03, -6.63) * mm, "end": v(-14.43, -5.84) * mm});
            skLineSegment(sketch, "E1272.2.4", {"start": v(-14.03, -6.63) * mm, "end": v(-13.6, -7.46) * mm});
            skLineSegment(sketch, "E1272.2.5", {"start": v(-13.6, -7.46) * mm, "end": v(-13.2, -8.25) * mm});
            skLineSegment(sketch, "E1272.3.0", {"start": v(-13.17, -12.41) * mm, "end": v(-14.88, -10.3) * mm});
            skLineSegment(sketch, "E1272.3.1", {"start": v(-11.2, -10.82) * mm, "end": v(-13.17, -12.41) * mm});
            skLineSegment(sketch, "E1272.3.2", {"start": v(-12.9, -8.7) * mm, "end": v(-14.88, -10.3) * mm});
            skLineSegment(sketch, "E1272.3.3", {"start": v(-12.34, -9.4) * mm, "end": v(-12.9, -8.7) * mm});
            skLineSegment(sketch, "E1272.3.4", {"start": v(-12.34, -9.4) * mm, "end": v(-11.76, -10.13) * mm});
            skLineSegment(sketch, "E1272.3.5", {"start": v(-11.76, -10.13) * mm, "end": v(-11.2, -10.82) * mm});
            skLineSegment(sketch, "E1272.4.0", {"start": v(-10.3, -14.88) * mm, "end": v(-12.4, -13.17) * mm});
            skLineSegment(sketch, "E1272.4.1", {"start": v(-8.7, -12.9) * mm, "end": v(-10.3, -14.88) * mm});
            skLineSegment(sketch, "E1272.4.2", {"start": v(-10.81, -11.2) * mm, "end": v(-12.4, -13.17) * mm});
            skLineSegment(sketch, "E1272.4.3", {"start": v(-10.12, -11.76) * mm, "end": v(-10.81, -11.2) * mm});
            skLineSegment(sketch, "E1272.4.4", {"start": v(-10.12, -11.76) * mm, "end": v(-9.4, -12.35) * mm});
            skLineSegment(sketch, "E1272.4.5", {"start": v(-9.4, -12.35) * mm, "end": v(-8.7, -12.9) * mm});
            skLineSegment(sketch, "E1272.5.0", {"start": v(-6.98, -16.7) * mm, "end": v(-9.4, -15.47) * mm});
            skLineSegment(sketch, "E1272.5.1", {"start": v(-5.83, -14.44) * mm, "end": v(-6.98, -16.7) * mm});
            skLineSegment(sketch, "E1272.5.2", {"start": v(-8.25, -13.2) * mm, "end": v(-9.4, -15.47) * mm});
            skLineSegment(sketch, "E1272.5.3", {"start": v(-7.45, -13.6) * mm, "end": v(-8.25, -13.2) * mm});
            skLineSegment(sketch, "E1272.5.4", {"start": v(-7.45, -13.6) * mm, "end": v(-6.62, -14.03) * mm});
            skLineSegment(sketch, "E1272.5.5", {"start": v(-6.62, -14.03) * mm, "end": v(-5.83, -14.44) * mm});
            skLineSegment(sketch, "E1272.6.0", {"start": v(-3.36, -17.79) * mm, "end": v(-5.98, -17.08) * mm});
            skLineSegment(sketch, "E1272.6.1", {"start": v(-2.7, -15.33) * mm, "end": v(-3.36, -17.79) * mm});
            skLineSegment(sketch, "E1272.6.2", {"start": v(-5.32, -14.63) * mm, "end": v(-5.98, -17.08) * mm});
            skLineSegment(sketch, "E1272.6.3", {"start": v(-4.46, -14.86) * mm, "end": v(-5.32, -14.63) * mm});
            skLineSegment(sketch, "E1272.6.4", {"start": v(-4.46, -14.86) * mm, "end": v(-3.56, -15.1) * mm});
            skLineSegment(sketch, "E1272.6.5", {"start": v(-3.56, -15.1) * mm, "end": v(-2.7, -15.33) * mm});
            skLineSegment(sketch, "E1272.7.0", {"start": v(0.41, -18.1) * mm, "end": v(-2.3, -17.95) * mm});
            skLineSegment(sketch, "E1272.7.1", {"start": v(0.55, -15.56) * mm, "end": v(0.41, -18.1) * mm});
            skLineSegment(sketch, "E1272.7.2", {"start": v(-2.16, -15.42) * mm, "end": v(-2.3, -17.95) * mm});
            skLineSegment(sketch, "E1272.7.3", {"start": v(-1.27, -15.46) * mm, "end": v(-2.16, -15.42) * mm});
            skLineSegment(sketch, "E1272.7.4", {"start": v(-1.27, -15.46) * mm, "end": v(-0.34, -15.51) * mm});
            skLineSegment(sketch, "E1272.7.5", {"start": v(-0.34, -15.51) * mm, "end": v(0.55, -15.56) * mm});
            skLineSegment(sketch, "E1272.8.0", {"start": v(4.17, -17.61) * mm, "end": v(1.49, -18.04) * mm});
            skLineSegment(sketch, "E1272.8.1", {"start": v(3.77, -15.1) * mm, "end": v(4.17, -17.61) * mm});
            skLineSegment(sketch, "E1272.8.2", {"start": v(1.09, -15.53) * mm, "end": v(1.49, -18.04) * mm});
            skLineSegment(sketch, "E1272.8.3", {"start": v(1.97, -15.39) * mm, "end": v(1.09, -15.53) * mm});
            skLineSegment(sketch, "E1272.8.4", {"start": v(1.97, -15.39) * mm, "end": v(2.9, -15.24) * mm});
            skLineSegment(sketch, "E1272.8.5", {"start": v(2.9, -15.24) * mm, "end": v(3.77, -15.1) * mm});
            skLineSegment(sketch, "E1272.9.0", {"start": v(7.74, -16.36) * mm, "end": v(5.2, -17.33) * mm});
            skLineSegment(sketch, "E1272.9.1", {"start": v(6.83, -14) * mm, "end": v(7.74, -16.36) * mm});
            skLineSegment(sketch, "E1272.9.2", {"start": v(4.3, -14.96) * mm, "end": v(5.2, -17.33) * mm});
            skLineSegment(sketch, "E1272.9.3", {"start": v(5.12, -14.64) * mm, "end": v(4.3, -14.96) * mm});
            skLineSegment(sketch, "E1272.9.4", {"start": v(5.12, -14.64) * mm, "end": v(6, -14.3) * mm});
            skLineSegment(sketch, "E1272.9.5", {"start": v(6, -14.3) * mm, "end": v(6.83, -14) * mm});
            skLineSegment(sketch, "E1272.10.0", {"start": v(10.97, -14.4) * mm, "end": v(8.7, -15.87) * mm});
            skLineSegment(sketch, "E1272.10.1", {"start": v(9.59, -12.27) * mm, "end": v(10.97, -14.4) * mm});
            skLineSegment(sketch, "E1272.10.2", {"start": v(7.31, -13.74) * mm, "end": v(8.7, -15.87) * mm});
            skLineSegment(sketch, "E1272.10.3", {"start": v(8.06, -13.26) * mm, "end": v(7.31, -13.74) * mm});
            skLineSegment(sketch, "E1272.10.4", {"start": v(8.06, -13.26) * mm, "end": v(8.84, -12.75) * mm});
            skLineSegment(sketch, "E1272.10.5", {"start": v(8.84, -12.75) * mm, "end": v(9.59, -12.27) * mm});
            skLineSegment(sketch, "E1272.11.0", {"start": v(13.72, -11.8) * mm, "end": v(11.8, -13.72) * mm});
            skLineSegment(sketch, "E1272.11.1", {"start": v(11.93, -10) * mm, "end": v(13.72, -11.8) * mm});
            skLineSegment(sketch, "E1272.11.2", {"start": v(10, -11.92) * mm, "end": v(11.8, -13.72) * mm});
            skLineSegment(sketch, "E1272.11.3", {"start": v(10.64, -11.3) * mm, "end": v(10, -11.92) * mm});
            skLineSegment(sketch, "E1272.11.4", {"start": v(10.64, -11.3) * mm, "end": v(11.3, -10.63) * mm});
            skLineSegment(sketch, "E1272.11.5", {"start": v(11.3, -10.63) * mm, "end": v(11.93, -10) * mm});
            skLineSegment(sketch, "E1272.12.0", {"start": v(15.88, -8.7) * mm, "end": v(14.4, -10.96) * mm});
            skLineSegment(sketch, "E1272.12.1", {"start": v(13.75, -7.3) * mm, "end": v(15.88, -8.7) * mm});
            skLineSegment(sketch, "E1272.12.2", {"start": v(12.27, -9.58) * mm, "end": v(14.4, -10.96) * mm});
            skLineSegment(sketch, "E1272.12.3", {"start": v(12.75, -8.84) * mm, "end": v(12.27, -9.58) * mm});
            skLineSegment(sketch, "E1272.12.4", {"start": v(12.75, -8.84) * mm, "end": v(13.26, -8.05) * mm});
            skLineSegment(sketch, "E1272.12.5", {"start": v(13.26, -8.05) * mm, "end": v(13.75, -7.3) * mm});
            skLineSegment(sketch, "E1272.13.0", {"start": v(17.34, -5.2) * mm, "end": v(16.36, -7.73) * mm});
            skLineSegment(sketch, "E1272.13.1", {"start": v(14.97, -4.29) * mm, "end": v(17.34, -5.2) * mm});
            skLineSegment(sketch, "E1272.13.2", {"start": v(14, -6.82) * mm, "end": v(16.36, -7.73) * mm});
            skLineSegment(sketch, "E1272.13.3", {"start": v(14.31, -6) * mm, "end": v(14, -6.82) * mm});
            skLineSegment(sketch, "E1272.13.4", {"start": v(14.31, -6) * mm, "end": v(14.65, -5.12) * mm});
            skLineSegment(sketch, "E1272.13.5", {"start": v(14.65, -5.12) * mm, "end": v(14.97, -4.29) * mm});
            skLineSegment(sketch, "E1272.14.0", {"start": v(18.04, -1.48) * mm, "end": v(17.61, -4.16) * mm});
            skLineSegment(sketch, "E1272.14.1", {"start": v(15.53, -1.08) * mm, "end": v(18.04, -1.48) * mm});
            skLineSegment(sketch, "E1272.14.2", {"start": v(15.1, -3.76) * mm, "end": v(17.61, -4.16) * mm});
            skLineSegment(sketch, "E1272.14.3", {"start": v(15.24, -2.88) * mm, "end": v(15.1, -3.76) * mm});
            skLineSegment(sketch, "E1272.14.4", {"start": v(15.24, -2.88) * mm, "end": v(15.4, -1.96) * mm});
            skLineSegment(sketch, "E1272.14.5", {"start": v(15.4, -1.96) * mm, "end": v(15.53, -1.08) * mm});
            skLineSegment(sketch, "E1272.15.0", {"start": v(17.95, 2.3) * mm, "end": v(18.1, -0.4) * mm});
            skLineSegment(sketch, "E1272.15.1", {"start": v(15.42, 2.17) * mm, "end": v(17.95, 2.3) * mm});
            skLineSegment(sketch, "E1272.15.2", {"start": v(15.56, -0.54) * mm, "end": v(18.1, -0.4) * mm});
            skLineSegment(sketch, "E1272.15.3", {"start": v(15.51, 0.35) * mm, "end": v(15.56, -0.54) * mm});
            skLineSegment(sketch, "E1272.15.4", {"start": v(15.51, 0.35) * mm, "end": v(15.46, 1.28) * mm});
            skLineSegment(sketch, "E1272.15.5", {"start": v(15.46, 1.28) * mm, "end": v(15.42, 2.17) * mm});
            skLineSegment(sketch, "E1272.16.0", {"start": v(17.08, 5.98) * mm, "end": v(17.78, 3.36) * mm});
            skLineSegment(sketch, "E1272.16.1", {"start": v(14.63, 5.33) * mm, "end": v(17.08, 5.98) * mm});
            skLineSegment(sketch, "E1272.16.2", {"start": v(15.33, 2.7) * mm, "end": v(17.78, 3.36) * mm});
            skLineSegment(sketch, "E1272.16.3", {"start": v(15.1, 3.57) * mm, "end": v(15.33, 2.7) * mm});
            skLineSegment(sketch, "E1272.16.4", {"start": v(15.1, 3.57) * mm, "end": v(14.86, 4.47) * mm});
            skLineSegment(sketch, "E1272.16.5", {"start": v(14.86, 4.47) * mm, "end": v(14.63, 5.33) * mm});
            skLineSegment(sketch, "E1272.17.0", {"start": v(15.47, 9.4) * mm, "end": v(16.7, 6.99) * mm});
            skLineSegment(sketch, "E1272.17.1", {"start": v(13.2, 8.25) * mm, "end": v(15.47, 9.4) * mm});
            skLineSegment(sketch, "E1272.17.2", {"start": v(14.43, 5.84) * mm, "end": v(16.7, 6.99) * mm});
            skLineSegment(sketch, "E1272.17.3", {"start": v(14.03, 6.63) * mm, "end": v(14.43, 5.84) * mm});
            skLineSegment(sketch, "E1272.17.4", {"start": v(14.03, 6.63) * mm, "end": v(13.6, 7.46) * mm});
            skLineSegment(sketch, "E1272.17.5", {"start": v(13.6, 7.46) * mm, "end": v(13.2, 8.25) * mm});
            skLineSegment(sketch, "E1272.18.0", {"start": v(13.17, 12.41) * mm, "end": v(14.88, 10.3) * mm});
            skLineSegment(sketch, "E1272.18.1", {"start": v(11.2, 10.82) * mm, "end": v(13.17, 12.41) * mm});
            skLineSegment(sketch, "E1272.18.2", {"start": v(12.9, 8.7) * mm, "end": v(14.88, 10.3) * mm});
            skLineSegment(sketch, "E1272.18.3", {"start": v(12.34, 9.4) * mm, "end": v(12.9, 8.7) * mm});
            skLineSegment(sketch, "E1272.18.4", {"start": v(12.34, 9.4) * mm, "end": v(11.76, 10.13) * mm});
            skLineSegment(sketch, "E1272.18.5", {"start": v(11.76, 10.13) * mm, "end": v(11.2, 10.82) * mm});
            skLineSegment(sketch, "E1272.19.0", {"start": v(10.3, 14.88) * mm, "end": v(12.4, 13.17) * mm});
            skLineSegment(sketch, "E1272.19.1", {"start": v(8.7, 12.9) * mm, "end": v(10.3, 14.88) * mm});
            skLineSegment(sketch, "E1272.19.2", {"start": v(10.81, 11.2) * mm, "end": v(12.4, 13.17) * mm});
            skLineSegment(sketch, "E1272.19.3", {"start": v(10.12, 11.76) * mm, "end": v(10.81, 11.2) * mm});
            skLineSegment(sketch, "E1272.19.4", {"start": v(10.12, 11.76) * mm, "end": v(9.4, 12.35) * mm});
            skLineSegment(sketch, "E1272.19.5", {"start": v(9.4, 12.35) * mm, "end": v(8.7, 12.9) * mm});
            skLineSegment(sketch, "E1272.20.0", {"start": v(6.98, 16.7) * mm, "end": v(9.4, 15.47) * mm});
            skLineSegment(sketch, "E1272.20.1", {"start": v(5.83, 14.44) * mm, "end": v(6.98, 16.7) * mm});
            skLineSegment(sketch, "E1272.20.2", {"start": v(8.25, 13.2) * mm, "end": v(9.4, 15.47) * mm});
            skLineSegment(sketch, "E1272.20.3", {"start": v(7.45, 13.6) * mm, "end": v(8.25, 13.2) * mm});
            skLineSegment(sketch, "E1272.20.4", {"start": v(7.45, 13.6) * mm, "end": v(6.62, 14.03) * mm});
            skLineSegment(sketch, "E1272.20.5", {"start": v(6.62, 14.03) * mm, "end": v(5.83, 14.44) * mm});
            skLineSegment(sketch, "E1272.21.0", {"start": v(3.36, 17.79) * mm, "end": v(5.98, 17.08) * mm});
            skLineSegment(sketch, "E1272.21.1", {"start": v(2.7, 15.33) * mm, "end": v(3.36, 17.79) * mm});
            skLineSegment(sketch, "E1272.21.2", {"start": v(5.32, 14.63) * mm, "end": v(5.98, 17.08) * mm});
            skLineSegment(sketch, "E1272.21.3", {"start": v(4.46, 14.86) * mm, "end": v(5.32, 14.63) * mm});
            skLineSegment(sketch, "E1272.21.4", {"start": v(4.46, 14.86) * mm, "end": v(3.56, 15.1) * mm});
            skLineSegment(sketch, "E1272.21.5", {"start": v(3.56, 15.1) * mm, "end": v(2.7, 15.33) * mm});
            skLineSegment(sketch, "E1272.22.0", {"start": v(-0.41, 18.1) * mm, "end": v(2.3, 17.95) * mm});
            skLineSegment(sketch, "E1272.22.1", {"start": v(-0.55, 15.56) * mm, "end": v(-0.41, 18.1) * mm});
            skLineSegment(sketch, "E1272.22.2", {"start": v(2.16, 15.42) * mm, "end": v(2.3, 17.95) * mm});
            skLineSegment(sketch, "E1272.22.3", {"start": v(1.27, 15.46) * mm, "end": v(2.16, 15.42) * mm});
            skLineSegment(sketch, "E1272.22.4", {"start": v(1.27, 15.46) * mm, "end": v(0.34, 15.51) * mm});
            skLineSegment(sketch, "E1272.22.5", {"start": v(0.34, 15.51) * mm, "end": v(-0.55, 15.56) * mm});
            skLineSegment(sketch, "E1272.23.0", {"start": v(-4.17, 17.61) * mm, "end": v(-1.49, 18.04) * mm});
            skLineSegment(sketch, "E1272.23.1", {"start": v(-3.77, 15.1) * mm, "end": v(-4.17, 17.61) * mm});
            skLineSegment(sketch, "E1272.23.2", {"start": v(-1.09, 15.53) * mm, "end": v(-1.49, 18.04) * mm});
            skLineSegment(sketch, "E1272.23.3", {"start": v(-1.97, 15.39) * mm, "end": v(-1.09, 15.53) * mm});
            skLineSegment(sketch, "E1272.23.4", {"start": v(-1.97, 15.39) * mm, "end": v(-2.9, 15.24) * mm});
            skLineSegment(sketch, "E1272.23.5", {"start": v(-2.9, 15.24) * mm, "end": v(-3.77, 15.1) * mm});
            skLineSegment(sketch, "E1272.24.0", {"start": v(-7.74, 16.36) * mm, "end": v(-5.2, 17.33) * mm});
            skLineSegment(sketch, "E1272.24.1", {"start": v(-6.83, 14) * mm, "end": v(-7.74, 16.36) * mm});
            skLineSegment(sketch, "E1272.24.2", {"start": v(-4.3, 14.96) * mm, "end": v(-5.2, 17.33) * mm});
            skLineSegment(sketch, "E1272.24.3", {"start": v(-5.12, 14.64) * mm, "end": v(-4.3, 14.96) * mm});
            skLineSegment(sketch, "E1272.24.4", {"start": v(-5.12, 14.64) * mm, "end": v(-6, 14.3) * mm});
            skLineSegment(sketch, "E1272.24.5", {"start": v(-6, 14.3) * mm, "end": v(-6.83, 14) * mm});
            skLineSegment(sketch, "E1272.25.0", {"start": v(-10.97, 14.4) * mm, "end": v(-8.7, 15.87) * mm});
            skLineSegment(sketch, "E1272.25.1", {"start": v(-9.59, 12.27) * mm, "end": v(-10.97, 14.4) * mm});
            skLineSegment(sketch, "E1272.25.2", {"start": v(-7.31, 13.74) * mm, "end": v(-8.7, 15.87) * mm});
            skLineSegment(sketch, "E1272.25.3", {"start": v(-8.06, 13.26) * mm, "end": v(-7.31, 13.74) * mm});
            skLineSegment(sketch, "E1272.25.4", {"start": v(-8.06, 13.26) * mm, "end": v(-8.84, 12.75) * mm});
            skLineSegment(sketch, "E1272.25.5", {"start": v(-8.84, 12.75) * mm, "end": v(-9.59, 12.27) * mm});
            skLineSegment(sketch, "E1272.26.0", {"start": v(-13.72, 11.8) * mm, "end": v(-11.8, 13.72) * mm});
            skLineSegment(sketch, "E1272.26.1", {"start": v(-11.93, 10) * mm, "end": v(-13.72, 11.8) * mm});
            skLineSegment(sketch, "E1272.26.2", {"start": v(-10, 11.92) * mm, "end": v(-11.8, 13.72) * mm});
            skLineSegment(sketch, "E1272.26.3", {"start": v(-10.64, 11.3) * mm, "end": v(-10, 11.92) * mm});
            skLineSegment(sketch, "E1272.26.4", {"start": v(-10.64, 11.3) * mm, "end": v(-11.3, 10.63) * mm});
            skLineSegment(sketch, "E1272.26.5", {"start": v(-11.3, 10.63) * mm, "end": v(-11.93, 10) * mm});
            skLineSegment(sketch, "E1272.27.0", {"start": v(-15.88, 8.7) * mm, "end": v(-14.4, 10.96) * mm});
            skLineSegment(sketch, "E1272.27.1", {"start": v(-13.75, 7.3) * mm, "end": v(-15.88, 8.7) * mm});
            skLineSegment(sketch, "E1272.27.2", {"start": v(-12.27, 9.58) * mm, "end": v(-14.4, 10.96) * mm});
            skLineSegment(sketch, "E1272.27.3", {"start": v(-12.75, 8.84) * mm, "end": v(-12.27, 9.58) * mm});
            skLineSegment(sketch, "E1272.27.4", {"start": v(-12.75, 8.84) * mm, "end": v(-13.26, 8.05) * mm});
            skLineSegment(sketch, "E1272.27.5", {"start": v(-13.26, 8.05) * mm, "end": v(-13.75, 7.3) * mm});
            skLineSegment(sketch, "E1272.28.0", {"start": v(-17.34, 5.2) * mm, "end": v(-16.36, 7.73) * mm});
            skLineSegment(sketch, "E1272.28.1", {"start": v(-14.97, 4.29) * mm, "end": v(-17.34, 5.2) * mm});
            skLineSegment(sketch, "E1272.28.2", {"start": v(-14, 6.82) * mm, "end": v(-16.36, 7.73) * mm});
            skLineSegment(sketch, "E1272.28.3", {"start": v(-14.31, 6) * mm, "end": v(-14, 6.82) * mm});
            skLineSegment(sketch, "E1272.28.4", {"start": v(-14.31, 6) * mm, "end": v(-14.65, 5.12) * mm});
            skLineSegment(sketch, "E1272.28.5", {"start": v(-14.65, 5.12) * mm, "end": v(-14.97, 4.29) * mm});
            skLineSegment(sketch, "E1272.29.0", {"start": v(-18.04, 1.48) * mm, "end": v(-17.61, 4.16) * mm});
            skLineSegment(sketch, "E1272.29.1", {"start": v(-15.53, 1.08) * mm, "end": v(-18.04, 1.48) * mm});
            skLineSegment(sketch, "E1272.29.2", {"start": v(-15.1, 3.76) * mm, "end": v(-17.61, 4.16) * mm});
            skLineSegment(sketch, "E1272.29.3", {"start": v(-15.24, 2.88) * mm, "end": v(-15.1, 3.76) * mm});
            skLineSegment(sketch, "E1272.29.4", {"start": v(-15.24, 2.88) * mm, "end": v(-15.4, 1.96) * mm});
            skLineSegment(sketch, "E1272.29.5", {"start": v(-15.4, 1.96) * mm, "end": v(-15.53, 1.08) * mm});
            skCircle(sketch, "E1273.0", {"center": v(0, 0) * mm, "radius": 57.15 * mm});
            skSolve(sketch);
        }
        {
            var Q0;
            Q0 = qSketchRegion(id + "F2", true);
            extrude(context, id + "F3", {"entities" : qUnion([Q0]), "depth" : 1.52 * mm});
        }
        {
            var Q0;
            Q0=makeQuery(id+"F1.opExtrude","CAP_FACE",FACE,{"disambiguationData":[OSD([sQuery(id+"F0.wireOp",EDGE,"a0ee4e53-7b65-4cc6-b097-e980374bba51"),sQuery(id+"F0.wireOp",EDGE,"28782ac0-7b0e-4891-8199-3a4f1225c46d"),sQuery(id+"F0.wireOp",EDGE,"43ffe4ab-a3be-41a3-bc0c-c6412107e32e"),sQuery(id+"F0.wireOp",EDGE,"dc48e744-2bf8-4d28-8ee7-cce8e2fb5321"),sQuery(id+"F0.wireOp",EDGE,"bf8fdbad-5b4a-41a4-b04b-4c9f6464a9db"),sQuery(id+"F0.wireOp",EDGE,"c0fb4448-2790-4191-9f6e-ebd55608eed1"),sQuery(id+"F0.wireOp",EDGE,"93d0b0e8-c43c-4f3d-a24c-1e9478296678"),sQuery(id+"F0.wireOp",EDGE,"7697e389-9dc3-460e-a292-7d678f4f1f46"),sQuery(id+"F0.wireOp",EDGE,"813d6692-cfe2-4671-8476-199ab0adf0d9"),sQuery(id+"F0.wireOp",EDGE,"7046412e-9f64-4fbd-a4c4-bef392f06694"),sQuery(id+"F0.wireOp",EDGE,"675f2f7f-5611-4529-bcab-d7c1451cd4fa"),sQuery(id+"F0.wireOp",EDGE,"d182c7ab-291f-44e7-a90d-3923d8b53343"),sQuery(id+"F0.wireOp",EDGE,"936cdbd5-7158-42f7-b2bc-9502d12045dd"),sQuery(id+"F0.wireOp",EDGE,"5752c7da-8fc2-4d80-9823-127daa68e405"),sQuery(id+"F0.wireOp",EDGE,"4bcbabae-024d-4715-a612-e5412e92e144"),sQuery(id+"F0.wireOp",EDGE,"0fc41205-7475-48f9-bf52-c23a16a363bf"),sQuery(id+"F0.wireOp",EDGE,"f1db7064-d933-4c26-99cf-68692b19b403"),sQuery(id+"F0.wireOp",EDGE,"0ec743de-02d6-41bf-b949-6e33cf799153"),sQuery(id+"F0.wireOp",EDGE,"deed504f-6629-4c3e-b731-5790958551cc"),sQuery(id+"F0.wireOp",EDGE,"9a4cfbdf-9131-4cb8-b0cc-ffaa8761dad6"),sQuery(id+"F0.wireOp",EDGE,"7d4f937e-aba7-4631-bb69-18a2a736b779"),sQuery(id+"F0.wireOp",EDGE,"99003f90-dbef-4bbf-a855-fc3390bd2bda"),sQuery(id+"F0.wireOp",EDGE,"698dfc52-a86a-49ff-ad8f-042d98267aa1"),sQuery(id+"F0.wireOp",EDGE,"26a38619-e418-4834-bf8f-41458db517ca"),sQuery(id+"F0.wireOp",EDGE,"99986c6a-a6f3-4f5e-bfa0-b9f2e2ee64ed"),sQuery(id+"F0.wireOp",EDGE,"927d7d57-56ba-42a1-be55-3bb78293e291"),sQuery(id+"F0.wireOp",EDGE,"917b3803-a639-43a1-b0b1-d80f0c2bfdf7"),sQuery(id+"F0.wireOp",EDGE,"fac2830c-de90-4a53-83eb-ba410fa5ca71"),sQuery(id+"F0.wireOp",EDGE,"b911d83d-b9a1-4f01-b092-ce727761331b"),sQuery(id+"F0.wireOp",EDGE,"1a262198-34e3-445f-bcdb-42479f9a2192"),sQuery(id+"F0.wireOp",EDGE,"fde727ea-d3f2-4d38-a1d9-f9d9e8608d47"),sQuery(id+"F0.wireOp",EDGE,"7dba479d-2e9f-4ea1-be82-347138dca80f"),sQuery(id+"F0.wireOp",EDGE,"bb5bd3ef-d1c4-42b3-b515-f442d456ab7f"),sQuery(id+"F0.wireOp",EDGE,"49241490-21fc-4964-bb50-688fcb6a107a"),sQuery(id+"F0.wireOp",EDGE,"7bad562f-b72e-4cbc-b13e-860ad0cf9277"),sQuery(id+"F0.wireOp",EDGE,"01a38179-a4ec-4c18-81b7-e22eaecd6366"),sQuery(id+"F0.wireOp",EDGE,"5800b559-6ef2-4f17-b4a8-af959ec671b9"),sQuery(id+"F0.wireOp",EDGE,"4d956042-3511-4874-b9bb-0d4904a742e4"),sQuery(id+"F0.wireOp",EDGE,"c6bcc5a0-b07b-43b9-84d6-51167e28eca0"),sQuery(id+"F0.wireOp",EDGE,"025251d3-07ff-4811-aadc-cf0b2832a614"),sQuery(id+"F0.wireOp",EDGE,"844a8369-a0e8-48f8-ad11-e99884c9d341"),sQuery(id+"F0.wireOp",EDGE,"4305cde0-a5c6-406d-bf74-c08e412d9c01"),sQuery(id+"F0.wireOp",EDGE,"f626a75d-f29d-4dae-b1ed-059d04aca0bb"),sQuery(id+"F0.wireOp",EDGE,"3167a2a2-c5cd-48e4-a576-9c03de96c99d"),sQuery(id+"F0.wireOp",EDGE,"4c9d0dfe-649b-45d2-89bb-e6e2d6144dd4"),sQuery(id+"F0.wireOp",EDGE,"93b8ff5d-ef36-4af5-bf9f-a9f03e630389"),sQuery(id+"F0.wireOp",EDGE,"1885d607-f4dd-4d4e-9b3a-c26a6558c21a"),sQuery(id+"F0.wireOp",EDGE,"fd400388-1826-4c05-92b3-6777b2abc366"),sQuery(id+"F0.wireOp",EDGE,"1cb44d1c-5766-421b-8fef-6cd898336a52"),sQuery(id+"F0.wireOp",EDGE,"a0bcb158-6438-4e12-8a33-a74f335f686b"),sQuery(id+"F0.wireOp",EDGE,"f4bf6fd0-f838-4daa-8398-16fb0174a711"),sQuery(id+"F0.wireOp",EDGE,"d8b35c5f-17c5-4792-9456-c95466667781"),sQuery(id+"F0.wireOp",EDGE,"bfe3515a-151a-421e-82ba-14c4ed01c104"),sQuery(id+"F0.wireOp",EDGE,"ea735a5d-e4a1-4bf0-bc4f-da954ba21756"),sQuery(id+"F0.wireOp",EDGE,"6f267e62-032a-41a0-a47b-0e38db9726c5"),sQuery(id+"F0.wireOp",EDGE,"f3c7efec-2d04-4889-8a84-6e23f8f453a8"),sQuery(id+"F0.wireOp",EDGE,"935b57b8-2ce8-4740-be8f-4c69f6861abc"),sQuery(id+"F0.wireOp",EDGE,"6a37a2fe-1895-4ddd-9acb-bb1008877e29"),sQuery(id+"F0.wireOp",EDGE,"945a5a56-fe4d-47f2-b0aa-3f664f46c8ce"),sQuery(id+"F0.wireOp",EDGE,"ccc36d2f-104f-4017-afb7-f5c232ead2b3"),sQuery(id+"F0.wireOp",EDGE,"74861551-2099-47a1-b3e9-b461e7654287"),sQuery(id+"F0.wireOp",EDGE,"94141ea7-f131-4d6c-9b24-91e97f046ca4"),sQuery(id+"F0.wireOp",EDGE,"6bf83433-f798-478b-ae11-3d14ff05e5f3"),sQuery(id+"F0.wireOp",EDGE,"b96ffd9e-08be-4fa3-b3c1-3a31803a5b98"),sQuery(id+"F0.wireOp",EDGE,"b988f938-0f38-4c7c-9c95-ba21683367cf"),sQuery(id+"F0.wireOp",EDGE,"7f481302-255c-4ead-abc0-9a86e5c75a6c"),sQuery(id+"F0.wireOp",EDGE,"65df0fc2-c32a-402a-83f0-ffb7ead4d9e1"),sQuery(id+"F0.wireOp",EDGE,"1c83dd0f-eeec-4aea-b55d-64ac17ef288b"),sQuery(id+"F0.wireOp",EDGE,"61e7d2f3-8aa3-42f8-be86-1ebe91e02449"),sQuery(id+"F0.wireOp",EDGE,"1f13731c-77a8-4b15-afb5-967201fed954"),sQuery(id+"F0.wireOp",EDGE,"5e3f37b1-bafc-4778-bd7b-9a8112a22db5"),sQuery(id+"F0.wireOp",EDGE,"ee869f63-584a-43a4-9dac-c7bd6a02345a"),sQuery(id+"F0.wireOp",EDGE,"334b3f0f-87ad-43a5-99e9-5ab06b61060d"),sQuery(id+"F0.wireOp",EDGE,"d1695426-a1c5-49ca-b27d-0470f6942fc0"),sQuery(id+"F0.wireOp",EDGE,"1e6db00c-971b-48e3-ad57-b6839dfbcd10"),sQuery(id+"F0.wireOp",EDGE,"6a7fc925-6b68-49f6-a060-aab8e61d80bf"),sQuery(id+"F0.wireOp",EDGE,"a6a50006-6686-43d2-bde7-6996d55a3639"),sQuery(id+"F0.wireOp",EDGE,"47551230-7048-47fa-a27b-3174c446d38c"),sQuery(id+"F0.wireOp",EDGE,"39de9ed5-567b-445e-8a33-ec328456a919"),sQuery(id+"F0.wireOp",EDGE,"616ab9ce-760f-49aa-853c-4c71a6d32f52"),sQuery(id+"F0.wireOp",EDGE,"d46438af-8e10-4ec2-aeb9-396b9f5ef0fe"),sQuery(id+"F0.wireOp",EDGE,"3e4c557b-6bb7-4f54-913b-6ffc9c01923e"),sQuery(id+"F0.wireOp",EDGE,"0561e19c-cec4-463e-b3ca-e07bc53f99fc"),sQuery(id+"F0.wireOp",EDGE,"4f69e275-a90f-42cb-b993-f32d5310bdc2"),sQuery(id+"F0.wireOp",EDGE,"3dceb406-efe1-4fba-b68b-f4750cb478c0"),sQuery(id+"F0.wireOp",EDGE,"6d6b4f68-d82c-4b13-8153-59f03dd766ce"),sQuery(id+"F0.wireOp",EDGE,"3f3f2b81-7944-401d-9760-aefb5adfbdd2"),sQuery(id+"F0.wireOp",EDGE,"6a281107-5eec-4b71-ad6d-7e9851cda6ff"),sQuery(id+"F0.wireOp",EDGE,"24290a7b-1717-49d8-9f8a-11d0b35eb97d"),sQuery(id+"F0.wireOp",EDGE,"96a33a07-8776-4d87-b4cf-5df261abaafc"),sQuery(id+"F0.wireOp",EDGE,"8a754f7d-a2d3-47ec-990a-456960389fdb"),sQuery(id+"F0.wireOp",EDGE,"8a121ea7-0a02-4e91-95be-be751a87abd7"),sQuery(id+"F0.wireOp",EDGE,"ac0b32c6-eb4e-4305-a7e9-c8758a3032db"),sQuery(id+"F0.wireOp",EDGE,"48be6210-4467-4e76-a565-52944eaa5ab4"),sQuery(id+"F0.wireOp",EDGE,"f3841175-05c6-4537-9ebc-bb7576f38844"),sQuery(id+"F0.wireOp",EDGE,"738a4f83-c68a-44fa-856f-3313b712e321"),sQuery(id+"F0.wireOp",EDGE,"8a3c3ad5-7bb9-49ef-9e64-89cea8360ec9"),sQuery(id+"F0.wireOp",EDGE,"3491ef82-f81f-47aa-9efb-fda760c1ba90"),sQuery(id+"F0.wireOp",EDGE,"b0dbeffd-962d-437e-8301-d083e651ea96"),sQuery(id+"F0.wireOp",EDGE,"7bf541af-1cc3-4389-9f99-8affcc4cc06c"),sQuery(id+"F0.wireOp",EDGE,"0f7e6a36-3e6f-4214-8028-9673e23972dd"),sQuery(id+"F0.wireOp",EDGE,"1051ff0f-ef06-47de-ae6e-bbc6304fbfe4"),sQuery(id+"F0.wireOp",EDGE,"2fbf7309-9164-4e4f-b9bc-b90a2e9caa85"),sQuery(id+"F0.wireOp",EDGE,"7bc15c66-0dc6-4fac-9768-d519c7ab8e01"),sQuery(id+"F0.wireOp",EDGE,"f89ba450-3f42-4a19-9785-9c63077fbecb"),sQuery(id+"F0.wireOp",EDGE,"f0963e65-d15b-411e-a95d-49595ba11381"),sQuery(id+"F0.wireOp",EDGE,"1cab81b3-c50b-4e54-bc86-fe5adeff3f4b"),sQuery(id+"F0.wireOp",EDGE,"ac90957a-8136-4a52-99a4-20d8dc54c0fe"),sQuery(id+"F0.wireOp",EDGE,"99f6fa74-8db8-4dd4-9b0c-bfc228d54919"),sQuery(id+"F0.wireOp",EDGE,"d24a3037-63b1-4bde-bc79-7d3fa0d842d3"),sQuery(id+"F0.wireOp",EDGE,"be0ccf9b-9d53-44ad-a3f3-f56c6fdb8398"),sQuery(id+"F0.wireOp",EDGE,"bc538cb2-a427-4704-98b9-65cf2e40820e"),sQuery(id+"F0.wireOp",EDGE,"67486f26-85ba-468f-9cc7-064031b3d75f"),sQuery(id+"F0.wireOp",EDGE,"d1dffca6-a7ca-4465-8ccb-c4d17aeb9077"),sQuery(id+"F0.wireOp",EDGE,"7e919344-1e24-4dd2-bd49-eba118f65d2a"),sQuery(id+"F0.wireOp",EDGE,"13939587-63b0-4985-862b-05d1727cb0af"),sQuery(id+"F0.wireOp",EDGE,"c9fe85e5-755c-4665-ab19-45b6f299e369"),sQuery(id+"F0.wireOp",EDGE,"55a9b869-b362-4b86-b916-68e6c489148d"),sQuery(id+"F0.wireOp",EDGE,"6545422e-9b5f-4873-baf5-974d8a0efad4"),sQuery(id+"F0.wireOp",EDGE,"727e534f-723d-4cc8-84ba-b8d9cfeec071"),sQuery(id+"F0.wireOp",EDGE,"f736439a-afd7-4208-b50a-6dac63be6444"),sQuery(id+"F0.wireOp",EDGE,"e569db09-d282-4a18-9ea9-5d8b2509e23b"),sQuery(id+"F0.wireOp",EDGE,"c94a5938-bd95-4965-a3ba-1913b3aa616f"),sQuery(id+"F0.wireOp",EDGE,"43c68e4c-06b6-4df6-92bc-0e52d15587dd"),sQuery(id+"F0.wireOp",EDGE,"aa297102-daa2-4c0c-ae3a-dd2766206041"),sQuery(id+"F0.wireOp",EDGE,"e7ba9a92-ab4d-46b9-9cca-dc062a8327d1"),sQuery(id+"F0.wireOp",EDGE,"847797e3-3dc9-4971-a848-5569514e7d3c"),sQuery(id+"F0.wireOp",EDGE,"4a320543-99b8-4cf0-bd54-5048a3986884"),sQuery(id+"F0.wireOp",EDGE,"07d6b457-bec7-4bff-b681-0b815d9fe15b"),sQuery(id+"F0.wireOp",EDGE,"c88c16c9-fe87-43de-9813-2d066290cedc"),sQuery(id+"F0.wireOp",EDGE,"1b731034-9c0b-4618-90ef-f5c08baf83c6"),sQuery(id+"F0.wireOp",EDGE,"d5efd0d0-26f2-40de-91e4-a2bdaf0fe06e"),sQuery(id+"F0.wireOp",EDGE,"de69d900-2932-4f84-a5c7-088718f9f242"),sQuery(id+"F0.wireOp",EDGE,"d7a1f0f2-0789-4291-9e79-99522084d9cf"),sQuery(id+"F0.wireOp",EDGE,"aa1a97d6-9360-4391-a3a3-865fd1dd5ae6"),sQuery(id+"F0.wireOp",EDGE,"fb98d708-de0e-4a1a-a63b-dcd059c045cd"),sQuery(id+"F0.wireOp",EDGE,"72f19fba-b03f-47d7-8e86-5aa40006db50"),sQuery(id+"F0.wireOp",EDGE,"16949400-9a0a-479a-b9a8-33db09345c5f"),sQuery(id+"F0.wireOp",EDGE,"7831d9a0-3a9c-447f-935d-1a59c5772436"),sQuery(id+"F0.wireOp",EDGE,"d9304da9-ae36-40fe-9ca2-7891bcdbf2ff"),sQuery(id+"F0.wireOp",EDGE,"7d689b09-a038-49bc-9104-e336cca6a260"),sQuery(id+"F0.wireOp",EDGE,"4dcb15a3-c703-48f5-a823-e4f10e41e73f"),sQuery(id+"F0.wireOp",EDGE,"438c4aff-c944-435f-954c-eff83fbdb4b5"),sQuery(id+"F0.wireOp",EDGE,"d8df2163-25a3-42db-82f8-d0909a75f245"),sQuery(id+"F0.wireOp",EDGE,"ea785a37-a159-4036-853a-24a4ba050102"),sQuery(id+"F0.wireOp",EDGE,"e424bf75-bb13-4a6a-86d5-e1a57735723f"),sQuery(id+"F0.wireOp",EDGE,"6420f827-5a91-433c-bbc2-09ef0ab5eb27"),sQuery(id+"F0.wireOp",EDGE,"b3587a16-729c-4f39-85b7-c0c805f2fdb1"),sQuery(id+"F0.wireOp",EDGE,"797de20e-a635-4c89-b806-16e3d98188a8"),sQuery(id+"F0.wireOp",EDGE,"336fa35a-780c-4d6c-b28f-c5f3750bd672"),sQuery(id+"F0.wireOp",EDGE,"bee6a76e-9d23-4995-8ab7-8531df7f144d"),sQuery(id+"F0.wireOp",EDGE,"8f4c86da-0b59-45c8-aedc-14b22fc91796"),sQuery(id+"F0.wireOp",EDGE,"985cb4a5-4683-4ae1-a011-8bf5a2fcf6b0"),sQuery(id+"F0.wireOp",EDGE,"17d0b9f7-43bc-4134-8b44-3fec2d6b708a"),sQuery(id+"F0.wireOp",EDGE,"c495664d-2375-4a9b-b6ea-95090bf72f5e"),sQuery(id+"F0.wireOp",EDGE,"bbcf04d4-ccc6-4d92-8d33-48e2bfbee461"),sQuery(id+"F0.wireOp",EDGE,"fac67708-3bdd-47fc-a718-b14ee28ff9e5"),sQuery(id+"F0.wireOp",EDGE,"aebf0e65-0e1a-4b3c-aa39-42e2ca52b193"),sQuery(id+"F0.wireOp",EDGE,"555e4dd1-6230-4988-87b7-8b7dadb2a9d2"),sQuery(id+"F0.wireOp",EDGE,"bf504a83-9dba-40de-84c3-502101af2714"),sQuery(id+"F0.wireOp",EDGE,"fadce42c-8f69-428a-b658-f6f8d6eb353d"),sQuery(id+"F0.wireOp",EDGE,"7c0a4797-3dea-40ed-9219-94c1405a0c12"),sQuery(id+"F0.wireOp",EDGE,"ad761fb6-ce24-4500-a799-3e71ff986c9b"),sQuery(id+"F0.wireOp",EDGE,"8f94daf9-1a92-4f2f-a168-fe1e2849e0a4"),sQuery(id+"F0.wireOp",EDGE,"4d29fdcd-854b-4467-9f86-8ef238888501"),sQuery(id+"F0.wireOp",EDGE,"a315fe7d-6266-49d0-af4c-74ab1e241cb3"),sQuery(id+"F0.wireOp",EDGE,"247d7d3b-696a-4077-b4b9-907c1b9ea7b7"),sQuery(id+"F0.wireOp",EDGE,"a0d54748-be99-4639-9743-a2de1cc90493"),sQuery(id+"F0.wireOp",EDGE,"e27e79a7-379b-44be-b6d4-06a7fab5db17"),sQuery(id+"F0.wireOp",EDGE,"6dbe1323-1ff3-459e-aa4a-0a2cda1b8f69"),sQuery(id+"F0.wireOp",EDGE,"a475f993-d7fe-4669-92dd-6d5099f62343"),sQuery(id+"F0.wireOp",EDGE,"bd2dcd8d-1c13-459b-8b67-5d8b5cd3d02c"),sQuery(id+"F0.wireOp",EDGE,"041a13ff-0f98-47c5-a5a8-7731296a202a"),sQuery(id+"F0.wireOp",EDGE,"efcbeb58-b9e6-434e-aafb-f2caea61a543"),sQuery(id+"F0.wireOp",EDGE,"621733e0-c581-4189-9c70-74d05e258c2e"),sQuery(id+"F0.wireOp",EDGE,"e68780e2-9846-46d1-a978-c555b5663c7c"),sQuery(id+"F0.wireOp",EDGE,"f73636c8-39fc-46c1-b7ba-a055fdd8d873"),sQuery(id+"F0.wireOp",EDGE,"ab133b1c-5c7d-4a15-8c51-87f40838a200"),sQuery(id+"F0.wireOp",EDGE,"246a4357-1727-4672-a319-95a7f0266f2d"),sQuery(id+"F0.wireOp",EDGE,"eeac33ee-0c54-4d82-ac5a-aaf4af6d4639"),sQuery(id+"F0.wireOp",EDGE,"9fb83c6c-2e0c-4495-9731-eca2780b59da"),sQuery(id+"F0.wireOp",EDGE,"61322b04-a650-4460-a93f-15139eef680a"),sQuery(id+"F0.wireOp",EDGE,"5e367480-fc0a-4cdc-b756-9619a975dec3"),sQuery(id+"F0.wireOp",EDGE,"0db463eb-09a4-4666-a842-815b03d0d38a"),sQuery(id+"F0.wireOp",EDGE,"905f70a6-497d-4883-b851-984a48cd9594"),sQuery(id+"F0.wireOp",EDGE,"dcae319a-da14-48e6-8f3c-e7e4bd11bad5"),sQuery(id+"F0.wireOp",EDGE,"2fce2187-f3bf-4338-abfc-758848bb28ee"),sQuery(id+"F0.wireOp",EDGE,"daac7d07-d822-4af9-92ae-f5dd82c6a041"),sQuery(id+"F0.wireOp",EDGE,"bfc088ed-77a6-49ed-9ff5-6c2b191bf0ad"),sQuery(id+"F0.wireOp",EDGE,"40a18498-d793-4027-9fd2-bc3ccb94f5dc"),sQuery(id+"F0.wireOp",EDGE,"87b37e8e-b3de-4061-9f8c-118ea2367425"),sQuery(id+"F0.wireOp",EDGE,"90fa7182-c915-4ae1-8588-5b13e40def36"),sQuery(id+"F0.wireOp",EDGE,"02230e9b-dc09-4a33-bc43-f0e49d2302dc"),sQuery(id+"F0.wireOp",EDGE,"7c3824a4-707c-4506-9c07-735912c535d2"),sQuery(id+"F0.wireOp",EDGE,"e1086339-4cb9-43f9-90aa-d77f84c0848b"),sQuery(id+"F0.wireOp",EDGE,"bc315a90-b46a-464b-998b-0982f1dd3dce"),sQuery(id+"F0.wireOp",EDGE,"54fc364b-1d5c-4734-839d-b2f6629a5a9c"),sQuery(id+"F0.wireOp",EDGE,"9e58e7e8-f3a6-4c14-abd9-63bccd610232"),sQuery(id+"F0.wireOp",EDGE,"b75b6e71-ab25-435c-b27a-96416875fef1"),sQuery(id+"F0.wireOp",EDGE,"33467386-7da1-4466-bac2-f063697ec0b0"),sQuery(id+"F0.wireOp",EDGE,"b40c37fc-8aa1-4597-9746-30cd3e7d9b24"),sQuery(id+"F0.wireOp",EDGE,"10870c8b-1772-4d2e-9b59-b64ad3106769"),sQuery(id+"F0.wireOp",EDGE,"b0f8336b-e4bd-4490-a9e6-976f2b7efe03"),sQuery(id+"F0.wireOp",EDGE,"1d57452c-5c0c-4054-9787-53f14be4ba52"),sQuery(id+"F0.wireOp",EDGE,"981288f3-b602-4186-ba49-b4ca6516d8d0"),sQuery(id+"F0.wireOp",EDGE,"3fae167c-06ad-4a0f-af93-932dc7f78fef"),sQuery(id+"F0.wireOp",EDGE,"6b817f3a-36be-450b-98c3-ee377c88008c"),sQuery(id+"F0.wireOp",EDGE,"e2075037-c5f5-408b-b9b8-b54b826ff48b"),sQuery(id+"F0.wireOp",EDGE,"d9e548c8-4fac-4dc1-9b26-770d64c4879c"),sQuery(id+"F0.wireOp",EDGE,"a208ac86-6e06-4d92-8d05-e1a57909a583"),sQuery(id+"F0.wireOp",EDGE,"5ab40081-5f11-40f6-b732-8a577d8852ca"),sQuery(id+"F0.wireOp",EDGE,"2b70d11d-5cb1-49ae-b429-7ac6262d9197"),sQuery(id+"F0.wireOp",EDGE,"17fa6ffb-fa94-4b00-a7f4-9b1ad321c381"),sQuery(id+"F0.wireOp",EDGE,"c598b84b-5f5f-4626-98f8-06b77259816f"),sQuery(id+"F0.wireOp",EDGE,"c42d389f-64a8-4e29-90ba-ad465b36c984"),sQuery(id+"F0.wireOp",EDGE,"6e76dcc9-8371-482c-b232-ecdc5d38dd5c"),sQuery(id+"F0.wireOp",EDGE,"61f5f20c-9c7e-4924-8642-d61aa6e6b6c3"),sQuery(id+"F0.wireOp",EDGE,"3e5b592b-86f2-4085-bb26-c21ce9f47295"),sQuery(id+"F0.wireOp",EDGE,"c77b56ee-1232-4b49-a01a-3e8a0768b101"),sQuery(id+"F0.wireOp",EDGE,"6bbec194-7ee8-4028-8a82-41026d6588f5"),sQuery(id+"F0.wireOp",EDGE,"be482f2f-9668-427e-acbe-cb45d5bfdaf2"),sQuery(id+"F0.wireOp",EDGE,"7c1635c5-ac3d-4faa-b7b0-b20362e751bb"),sQuery(id+"F0.wireOp",EDGE,"f5b7f320-62eb-4dbc-81c8-7a892fd5ed62"),sQuery(id+"F0.wireOp",EDGE,"03a4be1c-a707-4b0a-84fe-652fcd27591b"),sQuery(id+"F0.wireOp",EDGE,"578034fe-3c99-47ec-8eea-244122fb2900"),sQuery(id+"F0.wireOp",EDGE,"dc8f4cf5-a8dc-42df-b8c6-1c061cc03ccb"),sQuery(id+"F0.wireOp",EDGE,"4ecca4ca-5acd-4e26-b545-397786b4a4d8"),sQuery(id+"F0.wireOp",EDGE,"01868341-dcd4-4d86-9f69-6aa016659bce"),sQuery(id+"F0.wireOp",EDGE,"082c0d23-307c-426c-a5fd-40aaf1ed85fe"),sQuery(id+"F0.wireOp",EDGE,"bd8de719-41a1-4bd0-8081-9c1217f6791c"),sQuery(id+"F0.wireOp",EDGE,"006f0c99-338c-4f36-b08f-c77e49a0fbad"),sQuery(id+"F0.wireOp",EDGE,"c6bfb2f8-91ac-4f7d-96ed-f06fe387df6e"),sQuery(id+"F0.wireOp",EDGE,"17ee62eb-b815-428a-b96c-02ce3f13adcb"),sQuery(id+"F0.wireOp",EDGE,"e2444381-855a-4f0f-b36b-fa641b87d2d9"),sQuery(id+"F0.wireOp",EDGE,"cefcb511-22d9-4a09-8e68-20cc47fd51b8"),sQuery(id+"F0.wireOp",EDGE,"1b4dc11c-ad53-41b3-9f2b-c9ab2159d558"),sQuery(id+"F0.wireOp",EDGE,"22eee332-1fd1-4251-85cd-418106cf4375"),sQuery(id+"F0.wireOp",EDGE,"84f580c0-643a-4f0a-9138-4e82baa37bac"),sQuery(id+"F0.wireOp",EDGE,"2086a38c-e74c-4a06-b99b-f26b8d01a979"),sQuery(id+"F0.wireOp",EDGE,"d83b5a14-96ed-4fac-8959-51fcf7670e97"),sQuery(id+"F0.wireOp",EDGE,"2c74cf45-521b-4012-a9bf-3b6af9be1117"),sQuery(id+"F0.wireOp",EDGE,"ec506c91-6b42-4a2e-b46e-7c65f90ec31b"),sQuery(id+"F0.wireOp",EDGE,"3211954a-1ccd-4666-9e85-f34d62337c7a"),sQuery(id+"F0.wireOp",EDGE,"a3f67027-3a5e-4afe-b728-b5c4fa98ced0"),sQuery(id+"F0.wireOp",EDGE,"5d943437-c8fc-4969-be62-097ac526ded0"),sQuery(id+"F0.wireOp",EDGE,"06eaccc8-6e93-4f7e-8cfb-ee9c0d61cdc3"),sQuery(id+"F0.wireOp",EDGE,"120e285d-05a4-47e4-8683-9851670f8bb2"),sQuery(id+"F0.wireOp",EDGE,"bf81dcde-89c3-4c8c-8c75-b117a7b5e3d3"),sQuery(id+"F0.wireOp",EDGE,"12e0389e-09b0-48ee-a7f9-ef9ff7f71945"),sQuery(id+"F0.wireOp",EDGE,"51ad4ef6-65b6-46bc-b885-fdb47c514399"),sQuery(id+"F0.wireOp",EDGE,"38302d2c-e7fa-42bb-8c2c-be1136b57425"),sQuery(id+"F0.wireOp",EDGE,"aae20131-0b01-4595-b766-2af5648bae41"),sQuery(id+"F0.wireOp",EDGE,"ff5e1e80-4d6d-4328-a7e5-09995feede13"),sQuery(id+"F0.wireOp",EDGE,"02f12ae7-4dac-4e05-baab-76bbc31f51d9"),sQuery(id+"F0.wireOp",EDGE,"c2b7a8aa-d6f4-4ac0-9869-cc6bc6c287bc"),sQuery(id+"F0.wireOp",EDGE,"45f12263-a6d9-4ecd-a114-8398d307cda3"),sQuery(id+"F0.wireOp",EDGE,"eb4b2e3f-b314-4eb8-b66d-11d848cd9702"),sQuery(id+"F0.wireOp",EDGE,"d08e2fc3-db97-4518-af14-f57cd42bdb93"),sQuery(id+"F0.wireOp",EDGE,"c62695bf-9d10-4615-8556-b32945b0495b"),sQuery(id+"F0.wireOp",EDGE,"c974918c-ca22-4d76-9fc0-f96eec3cc436"),sQuery(id+"F0.wireOp",EDGE,"739d5020-6a0f-40cd-9f13-bcc5e6579085"),sQuery(id+"F0.wireOp",EDGE,"d4ec54ec-8324-4187-bba3-6aecab79e170"),sQuery(id+"F0.wireOp",EDGE,"306571b7-6b24-4c4c-a1c8-bfbc87d8905f"),sQuery(id+"F0.wireOp",EDGE,"f66ff50e-4ff1-48f0-8e8d-b7cf5b2a040a"),sQuery(id+"F0.wireOp",EDGE,"daf886da-2a84-4116-9424-664d25639f25"),sQuery(id+"F0.wireOp",EDGE,"067ee87a-2aaa-42c3-8fb6-e2e8e96a65df"),sQuery(id+"F0.wireOp",EDGE,"ddc883ec-767f-41b6-97ba-04dab902a0f4"),sQuery(id+"F0.wireOp",EDGE,"6abd8343-adbf-41c6-bb61-28074b4141f7"),sQuery(id+"F0.wireOp",EDGE,"303af2a4-8efc-4f4f-8ef3-d8f9148a8597"),sQuery(id+"F0.wireOp",EDGE,"9414ef44-f5ad-4d2e-a9d7-60932f4a20b1"),sQuery(id+"F0.wireOp",EDGE,"a0eeebb4-cc0f-4106-8cb1-e05a2e0a416f"),sQuery(id+"F0.wireOp",EDGE,"833a10bb-8592-4c3c-aee3-bfd569ec0f1e"),sQuery(id+"F0.wireOp",EDGE,"d0e442e8-2bba-4cf9-ab30-0e0386a8b8c2"),sQuery(id+"F0.wireOp",EDGE,"f987d9c6-208e-44db-b218-8dae03262d6f"),sQuery(id+"F0.wireOp",EDGE,"a26ca596-7ea9-4bee-a4df-367a95f3e545"),sQuery(id+"F0.wireOp",EDGE,"a5779ebb-c89d-4458-a00c-c9e01f5b5973"),sQuery(id+"F0.wireOp",EDGE,"f21783b2-21b3-468f-8d5d-5263caad2514"),sQuery(id+"F0.wireOp",EDGE,"edba20ce-ecb9-41bd-8226-28e95ef654d1"),sQuery(id+"F0.wireOp",EDGE,"a622b662-2178-4b95-ae14-f0ed84f39c17"),sQuery(id+"F0.wireOp",EDGE,"73587eb3-d81d-4fa9-aa56-62cfa1226ee6"),sQuery(id+"F0.wireOp",EDGE,"9a12fa1e-3112-4fb3-adbb-7adcbcf8620f"),sQuery(id+"F0.wireOp",EDGE,"103ca987-9e5f-43ff-aa0a-574345280784"),sQuery(id+"F0.wireOp",EDGE,"9bd448d9-35ad-43e2-ac07-9bb9ad8870f2"),sQuery(id+"F0.wireOp",EDGE,"2ffa967b-18d4-412e-a01b-3b78a495819e"),sQuery(id+"F0.wireOp",EDGE,"50512464-5ca0-4e4d-9ae7-1cc1055f42f2"),sQuery(id+"F0.wireOp",EDGE,"c461c4d4-4af2-42d4-948b-4ec19580dc35"),sQuery(id+"F0.wireOp",EDGE,"ecb23eb1-81de-4115-9db0-b2c109522bad"),sQuery(id+"F0.wireOp",EDGE,"4c41dc37-22eb-489d-a716-cc0c36f39e95"),sQuery(id+"F0.wireOp",EDGE,"78542c54-9d7a-4f83-a58d-da9691bdaca0"),sQuery(id+"F0.wireOp",EDGE,"6dbbe76f-bf3e-4459-9c72-c7ecb79f2599"),sQuery(id+"F0.wireOp",EDGE,"d2964659-1095-4c41-a85d-04ecb1e67d22"),sQuery(id+"F0.wireOp",EDGE,"be7ebe09-106f-435e-9153-6aa01453df74"),sQuery(id+"F0.wireOp",EDGE,"1c04703e-f2a3-4c8c-ae07-315639060602"),sQuery(id+"F0.wireOp",EDGE,"bb0df9f3-41ec-4b74-ae8c-d248db3bbda1"),sQuery(id+"F0.wireOp",EDGE,"a4d25204-afd0-4585-8e65-b7bdd4d03f70"),sQuery(id+"F0.wireOp",EDGE,"dd3ddbf8-632f-40d4-bba2-cd38dc60813c"),sQuery(id+"F0.wireOp",EDGE,"f82e9a7c-f7cf-4e8e-a293-8f428050ee04"),sQuery(id+"F0.wireOp",EDGE,"1d33b62b-690b-4d89-a4f2-b31df673149d"),sQuery(id+"F0.wireOp",EDGE,"1c9a8537-1b75-4561-8014-5d0839793d83"),sQuery(id+"F0.wireOp",EDGE,"7da6752e-0130-4427-b37a-f870623fd533"),sQuery(id+"F0.wireOp",EDGE,"3b50b7bf-802d-4722-b69f-b634c0ebe5fd"),sQuery(id+"F0.wireOp",EDGE,"509ff239-90b6-4fbe-bb57-96526ffbb594"),sQuery(id+"F0.wireOp",EDGE,"180e4fda-fba7-4278-9c24-33e623ce9905"),sQuery(id+"F0.wireOp",EDGE,"5920d0c8-b25e-4683-9891-726beeda9f14"),sQuery(id+"F0.wireOp",EDGE,"abb53ec4-693b-4cd8-8f90-21607318ac32"),sQuery(id+"F0.wireOp",EDGE,"813c9ebf-de40-4e0c-8072-1ce01e70ffae"),sQuery(id+"F0.wireOp",EDGE,"b26c0b99-29b3-4a19-abc5-54117a970742"),sQuery(id+"F0.wireOp",EDGE,"a5e9c79b-3b52-4ba9-b521-4fd20c288a4b"),sQuery(id+"F0.wireOp",EDGE,"d593f28c-d403-4033-af98-9880a669a0ee"),sQuery(id+"F0.wireOp",EDGE,"ad8c2ee1-1e38-4b18-b284-f762253671aa"),sQuery(id+"F0.wireOp",EDGE,"07aa20d9-5bd4-4cae-ac57-1fae0daa92e8"),sQuery(id+"F0.wireOp",EDGE,"d565bab9-d083-4930-9dc6-341856c6dcaf"),sQuery(id+"F0.wireOp",EDGE,"2738d55d-88fc-4993-8ec1-37b5a04e9b08"),sQuery(id+"F0.wireOp",EDGE,"05dced37-4d0f-41bf-8a2d-c997782e87b9"),sQuery(id+"F0.wireOp",EDGE,"4d017246-123a-4de1-a35e-6b362acbbedb"),sQuery(id+"F0.wireOp",EDGE,"37e57022-df8f-4a31-bc96-a8043f81fc3f"),sQuery(id+"F0.wireOp",EDGE,"7123fb36-b773-4292-8fcd-0f0684e2f7f6"),sQuery(id+"F0.wireOp",EDGE,"aa0e7ec4-3259-498c-b15d-b162ee01d909"),sQuery(id+"F0.wireOp",EDGE,"f394ea13-b473-4e84-ae02-2efceabd8e74"),sQuery(id+"F0.wireOp",EDGE,"34b7ddd7-5b87-432e-b0b2-8a4cecb90ba6"),sQuery(id+"F0.wireOp",EDGE,"86ca4e61-c620-4993-9e47-07488580a3c8"),sQuery(id+"F0.wireOp",EDGE,"f85c54f4-142e-4dc0-8ec6-8fc11b01442e"),sQuery(id+"F0.wireOp",EDGE,"43d2117f-53fe-44c9-885d-8f9cb5c2990c"),sQuery(id+"F0.wireOp",EDGE,"485bfe38-7d02-4abe-acaf-2e8422fab976"),sQuery(id+"F0.wireOp",EDGE,"4ad0de0c-3400-43fa-8625-8bf83bad5eba"),sQuery(id+"F0.wireOp",EDGE,"c9e7e1b8-322b-4c7c-8131-a25f5d484d37"),sQuery(id+"F0.wireOp",EDGE,"5f31f1f6-d40e-4c76-871f-efbf29229a10"),sQuery(id+"F0.wireOp",EDGE,"2341f378-6e8a-4808-bdda-5107740a4e72"),sQuery(id+"F0.wireOp",EDGE,"70fe7bf2-e18c-4a39-8663-7adb9fa09552"),sQuery(id+"F0.wireOp",EDGE,"3f01cd6a-3bf0-4465-b004-29128bb7135e"),sQuery(id+"F0.wireOp",EDGE,"c3540aa0-e260-4d56-98ac-be03f425b991"),sQuery(id+"F0.wireOp",EDGE,"0c9aeb50-b92f-42b1-a69e-a05d9f1eef4b"),sQuery(id+"F0.wireOp",EDGE,"fa91054d-bcef-47a6-8191-f95e63a7ac50"),sQuery(id+"F0.wireOp",EDGE,"7f7d0cc8-3f6c-4f55-98b7-40bdad5a5afc"),sQuery(id+"F0.wireOp",EDGE,"fda22a44-1e0c-4b5e-9f56-731edba39066"),sQuery(id+"F0.wireOp",EDGE,"8c888383-5152-4466-85ac-be87ccfda324"),sQuery(id+"F0.wireOp",EDGE,"3f7d6ee0-d9af-44ae-8c14-3c3c63bc35cd"),sQuery(id+"F0.wireOp",EDGE,"a11b762e-5c35-4478-b634-c0bde5372c59"),sQuery(id+"F0.wireOp",EDGE,"4ef27dc0-3f8a-4abf-bc82-3e658e9b4576"),sQuery(id+"F0.wireOp",EDGE,"ff7e588e-b80d-4494-b928-8aead235ba6b"),sQuery(id+"F0.wireOp",EDGE,"2f726558-5d46-44a5-8890-013a8af2fb6d"),sQuery(id+"F0.wireOp",EDGE,"4da7e619-5ec9-4c30-9fa9-5e8f818b586c"),sQuery(id+"F0.wireOp",EDGE,"fcb5bf59-f724-40bf-a93c-df29265e678e"),sQuery(id+"F0.wireOp",EDGE,"ebd3fb46-ade7-45fe-a8b2-4135c87953cc"),sQuery(id+"F0.wireOp",EDGE,"56209d7f-2321-400e-b666-842f0e323caf"),sQuery(id+"F0.wireOp",EDGE,"25070fa3-85a9-410d-a013-5a2437b870fd"),sQuery(id+"F0.wireOp",EDGE,"f10a09fe-5d46-4890-8871-337437fb93b1"),sQuery(id+"F0.wireOp",EDGE,"4bc09a70-5109-48c9-801e-a94224323d17"),sQuery(id+"F0.wireOp",EDGE,"bedb624d-55d7-49c3-a1e0-22580057bb39"),sQuery(id+"F0.wireOp",EDGE,"0ff46ae1-5ded-439e-b620-fa5599d96111"),sQuery(id+"F0.wireOp",EDGE,"746c5437-ba77-4817-9a45-636baa4d7b89"),sQuery(id+"F0.wireOp",EDGE,"4e907761-c308-486b-9933-48f3b43f4659"),sQuery(id+"F0.wireOp",EDGE,"c96bf18e-c1b0-4b95-ba17-1090479d2ea4"),sQuery(id+"F0.wireOp",EDGE,"190744f1-0e0c-43b1-8c51-d393dd3d4bf0"),sQuery(id+"F0.wireOp",EDGE,"8722c152-edc4-4c89-9289-79d72895c7fa"),sQuery(id+"F0.wireOp",EDGE,"3c1c7ed6-fc64-499f-aee9-3418b705639d"),sQuery(id+"F0.wireOp",EDGE,"e2badb26-cb38-44ca-bc58-92e3de63b6f8"),sQuery(id+"F0.wireOp",EDGE,"2ccd0fef-846d-485e-804d-85fdd7b21415"),sQuery(id+"F0.wireOp",EDGE,"85cf3f22-8d95-46a4-b412-cc8e0c5a1e7a"),sQuery(id+"F0.wireOp",EDGE,"36c562ca-cf81-40b6-8890-c98833280bba"),sQuery(id+"F0.wireOp",EDGE,"e0cb2875-ac02-492d-b256-83296656fbeb"),sQuery(id+"F0.wireOp",EDGE,"02052b0a-9100-4e6c-8e1d-81c2f94f8ffa"),sQuery(id+"F0.wireOp",EDGE,"42df54ce-8481-4a71-8046-98704643b0b8"),sQuery(id+"F0.wireOp",EDGE,"7d6679e0-59e7-45b7-9956-405c4ffd710a"),sQuery(id+"F0.wireOp",EDGE,"fe945fd7-80c7-4a7e-93bf-5150c6aec338"),sQuery(id+"F0.wireOp",EDGE,"1dcfdb14-3700-4d18-a8f8-4ecdd2d41f12"),sQuery(id+"F0.wireOp",EDGE,"705f835e-1fbe-4103-b21d-6b115d2ce59e"),sQuery(id+"F0.wireOp",EDGE,"1242c965-2a33-4cf4-b701-2917b13ae1b8"),sQuery(id+"F0.wireOp",EDGE,"a5eeb873-3ee8-44b6-92a4-21f573f1c98c"),sQuery(id+"F0.wireOp",EDGE,"2d139e89-6815-4495-b2ea-2cbbc5575223"),sQuery(id+"F0.wireOp",EDGE,"aa6f62da-9d95-44b1-b52b-a1dff2773bd8"),sQuery(id+"F0.wireOp",EDGE,"75387c55-516f-4644-8b3b-9b516fb984a2"),sQuery(id+"F0.wireOp",EDGE,"ddf068c2-fc09-4641-afa0-0f5eaafe47ec"),sQuery(id+"F0.wireOp",EDGE,"3fdf4c86-ea1b-4bb5-99ec-3044a5813809"),sQuery(id+"F0.wireOp",EDGE,"5dbeab65-f886-48b0-9603-43f0bd103a7a"),sQuery(id+"F0.wireOp",EDGE,"bbd39671-8956-48ac-a72d-beded71640e3"),sQuery(id+"F0.wireOp",EDGE,"e77ea1f8-953c-47da-b36d-ca7a301c01ec"),sQuery(id+"F0.wireOp",EDGE,"8748b016-ffa4-4c71-88e1-d567d17d5198"),sQuery(id+"F0.wireOp",EDGE,"d3885277-1971-4b19-9ac9-64ab6c618bc0"),sQuery(id+"F0.wireOp",EDGE,"1d5b33b2-dc5e-4819-8418-4f5d255eada3"),sQuery(id+"F0.wireOp",EDGE,"53c6b902-1589-40b8-a2a8-924550e61899"),sQuery(id+"F0.wireOp",EDGE,"a4db1815-eabd-4298-8b98-d81d9f414654"),sQuery(id+"F0.wireOp",EDGE,"7ccf15cb-d623-48c6-836d-0b64923c78d9"),sQuery(id+"F0.wireOp",EDGE,"f71362ce-a68a-4497-bfb9-c90ba9a9a06d"),sQuery(id+"F0.wireOp",EDGE,"f5f496dc-b8cc-4076-94d0-883d7f4b94be"),sQuery(id+"F0.wireOp",EDGE,"3263564a-85b9-4823-bd02-bd909b4da241"),sQuery(id+"F0.wireOp",EDGE,"dfa4bfc6-23ff-482a-a434-893fba50a0aa"),sQuery(id+"F0.wireOp",EDGE,"b9215695-43ae-4451-99d5-ffe407fba4aa"),sQuery(id+"F0.wireOp",EDGE,"473c03a6-dac4-4c92-a095-a18eac8fe6a6"),sQuery(id+"F0.wireOp",EDGE,"cc3ff233-c542-49b7-b684-f947dfd8172b"),sQuery(id+"F0.wireOp",EDGE,"064e2064-593c-4fc2-921b-2133a0986bff"),sQuery(id+"F0.wireOp",EDGE,"396f3095-e9ca-42c8-af0d-c1332b2e9ef9"),sQuery(id+"F0.wireOp",EDGE,"02fbb41d-a8d0-4158-aa86-64ef3c6d3f14"),sQuery(id+"F0.wireOp",EDGE,"518c1aec-a62b-465e-a6a8-a967ccc4b83a"),sQuery(id+"F0.wireOp",EDGE,"c7a2f402-6181-4b7b-8d39-9280429ff77b"),sQuery(id+"F0.wireOp",EDGE,"e06369f8-15d1-44c5-a9a6-487333b74079"),sQuery(id+"F0.wireOp",EDGE,"26e4f6d5-62c8-4aa5-8607-ad2b8a46218f"),sQuery(id+"F0.wireOp",EDGE,"bdb62519-c26f-4ca3-baef-fd5674aaa98a"),sQuery(id+"F0.wireOp",EDGE,"971deac8-02f9-4881-b096-68b0ed0d4ef7"),sQuery(id+"F0.wireOp",EDGE,"b3f6c54e-5ba1-4c9b-ab06-ff887e18d623"),sQuery(id+"F0.wireOp",EDGE,"bc4118e7-aed3-4703-bd36-447b393dc447"),sQuery(id+"F0.wireOp",EDGE,"b6e16d75-1139-4565-a286-e25bf0e1bcdf"),sQuery(id+"F0.wireOp",EDGE,"178e5208-0863-4cd4-91e8-2138fb17df43"),sQuery(id+"F0.wireOp",EDGE,"242c819c-d2d4-4f54-b000-3f41bc7bb28f"),sQuery(id+"F0.wireOp",EDGE,"aa0c8438-6628-4c13-985f-6c061554a2b8"),sQuery(id+"F0.wireOp",EDGE,"1d5657ee-30c5-40a6-b1f7-e46671814f9d"),sQuery(id+"F0.wireOp",EDGE,"89862b55-cfd9-41c4-8538-90352b786acf"),sQuery(id+"F0.wireOp",EDGE,"6d4d03d1-366e-4660-a0cd-9d8c123db2be"),sQuery(id+"F0.wireOp",EDGE,"c7f4da4b-8bf6-4229-b33b-0c2485b95d48"),sQuery(id+"F0.wireOp",EDGE,"6d885470-fe4d-471c-95d8-4ec8cfa82da0"),sQuery(id+"F0.wireOp",EDGE,"70f1da3a-ddbb-403f-9bf6-b954922d633b"),sQuery(id+"F0.wireOp",EDGE,"42f39b82-c81f-4697-95fb-0b881859a8a2"),sQuery(id+"F0.wireOp",EDGE,"feea9f10-177f-45ef-a5df-3751a5c51f57"),sQuery(id+"F0.wireOp",EDGE,"2b39117d-e2b6-4d35-b755-85c4c1d22e1d"),sQuery(id+"F0.wireOp",EDGE,"ae0a4542-48c9-469c-99b3-d2f52b71f71f"),sQuery(id+"F0.wireOp",EDGE,"72595a4a-4346-4881-bee9-ca404737387e"),sQuery(id+"F0.wireOp",EDGE,"14b5bf1a-39dc-40ed-8199-11cb1830c68e"),sQuery(id+"F0.wireOp",EDGE,"0bfe0592-e2e8-4af9-80f1-74eddb094739"),sQuery(id+"F0.wireOp",EDGE,"33585b95-de89-4a61-bb0b-ac5138497490"),sQuery(id+"F0.wireOp",EDGE,"894fff80-6bd1-4132-98f4-3cb2a154478e"),sQuery(id+"F0.wireOp",EDGE,"a9a1f528-d001-478a-bc5e-ea06366b1f05"),sQuery(id+"F0.wireOp",EDGE,"b5cf05b1-a568-4638-9b13-410cc4bc705c"),sQuery(id+"F0.wireOp",EDGE,"575f58e5-487a-4d60-baf1-e0db31fd321a"),sQuery(id+"F0.wireOp",EDGE,"f3a809c4-9690-428d-8479-f2fa9284ce6b"),sQuery(id+"F0.wireOp",EDGE,"d1e57e56-9c87-4890-8112-93c7570c70d7"),sQuery(id+"F0.wireOp",EDGE,"349ce66a-3db0-49cb-96e9-97a6d89fbc4d"),sQuery(id+"F0.wireOp",EDGE,"5c9da6b2-d180-497b-b97e-deabef8640d3"),sQuery(id+"F0.wireOp",EDGE,"2f043225-655c-442f-9d8f-b6a2f70d4b03"),sQuery(id+"F0.wireOp",EDGE,"94c5ddf2-0c98-4712-bc72-b26255c7299f"),sQuery(id+"F0.wireOp",EDGE,"2dc2b231-bbb2-44d1-98ad-6d2b5150722c"),sQuery(id+"F0.wireOp",EDGE,"13ad8273-b4b0-4d43-8538-38813206fd37"),sQuery(id+"F0.wireOp",EDGE,"8e789429-8ed4-4dff-93cc-045b934299c7"),sQuery(id+"F0.wireOp",EDGE,"f83dc63d-c536-418d-8ff6-15ed4a67131c"),sQuery(id+"F0.wireOp",EDGE,"545a6082-df20-4000-9aec-469e0704e975"),sQuery(id+"F0.wireOp",EDGE,"6d43a2d7-c5d1-4781-8dd1-de1db427477f"),sQuery(id+"F0.wireOp",EDGE,"43346fda-c566-488d-bb9f-6b789724eb50"),sQuery(id+"F0.wireOp",EDGE,"3e33d1c3-4071-42e1-9b79-df7bd7c71772"),sQuery(id+"F0.wireOp",EDGE,"b48248fd-b1ae-40b5-9e05-179f10cb075e"),sQuery(id+"F0.wireOp",EDGE,"5c7ebee7-e2b9-43e7-a82d-2389181e45b6"),sQuery(id+"F0.wireOp",EDGE,"404b9876-64bd-4bbc-90bf-2fc5da104a34"),sQuery(id+"F0.wireOp",EDGE,"06ebbb02-787e-4143-ae9c-e3cbd7a8c154"),sQuery(id+"F0.wireOp",EDGE,"821b92c1-2619-49da-9b0d-ba297cd6e38f"),sQuery(id+"F0.wireOp",EDGE,"844f7900-f3e8-45c8-8f9f-ec53237987de"),sQuery(id+"F0.wireOp",EDGE,"84eae196-ac68-4b45-815c-071479414627"),sQuery(id+"F0.wireOp",EDGE,"38ef94d1-dd75-4327-8098-016537463e24"),sQuery(id+"F0.wireOp",EDGE,"3c68abc3-dbc1-41cd-95bc-adec34724420"),sQuery(id+"F0.wireOp",EDGE,"175ec536-30cf-41bd-a682-57c7ab263180"),sQuery(id+"F0.wireOp",EDGE,"03bf834c-4b32-4328-b738-e017deda3571"),sQuery(id+"F0.wireOp",EDGE,"ebb97727-067f-473b-9b10-5fa6536e91a5"),sQuery(id+"F0.wireOp",EDGE,"fd163ead-baf0-4f25-a181-ac9c4aeace96"),sQuery(id+"F0.wireOp",EDGE,"05110ed8-dca7-4657-bdfc-32fd2defdcdb"),sQuery(id+"F0.wireOp",EDGE,"eb66f918-b69f-4904-8110-244684e40e99"),sQuery(id+"F0.wireOp",EDGE,"1f50ed4f-aa0d-4214-b223-064127cfafa5"),sQuery(id+"F0.wireOp",EDGE,"0d0165e5-049c-4ae0-8c6d-8400a7fc5d8b"),sQuery(id+"F0.wireOp",EDGE,"d9807aa4-4b74-4160-a8e8-c54f11348bec"),sQuery(id+"F0.wireOp",EDGE,"81bfc8a4-15dd-4bbc-a8de-7a6c49e89916"),sQuery(id+"F0.wireOp",EDGE,"d66dc645-2368-40f7-becf-0aa6712a8649"),sQuery(id+"F0.wireOp",EDGE,"b352bede-2f15-479d-83fd-bc3384d0b56c"),sQuery(id+"F0.wireOp",EDGE,"8a19aa2d-6d55-4ce0-97c0-baceea353766"),sQuery(id+"F0.wireOp",EDGE,"5f8e2f8c-074f-427b-973f-8d3ac7b5bbe8"),sQuery(id+"F0.wireOp",EDGE,"292625e9-1ce5-46a4-904c-f6854a7df383"),sQuery(id+"F0.wireOp",EDGE,"93cafe31-8154-4f90-bb1d-95a543f886ac"),sQuery(id+"F0.wireOp",EDGE,"9d6a5dd0-845d-4112-9f54-ebe0abe60735"),sQuery(id+"F0.wireOp",EDGE,"8a4db5ef-2743-479f-8098-9e3fcaae686a"),sQuery(id+"F0.wireOp",EDGE,"ca465e90-126a-4816-9119-d4150e6154a3"),sQuery(id+"F0.wireOp",EDGE,"E0"),sQuery(id+"F0.wireOp",EDGE,"af9dac12-ede5-4d6b-b329-3218d4e3a3d9.trimOffspring"),sQuery(id+"F0.wireOp",EDGE,"58ee0f98-cb6d-42ad-9831-0537edf5bdb0.trimOffspring"),sQuery(id+"F0.wireOp",EDGE,"117cccf0-6e4c-4dd9-9ce8-7d0eb2480f0d.trimOffspring"),sQuery(id+"F0.wireOp",EDGE,"bcfa5d6f-fb86-4086-82b3-a3f57acfab9d.trimOffspring"),sQuery(id+"F0.wireOp",EDGE,"a21dbb20-baf5-48e9-95c0-79a72f1e8c1b.trimOffspring"),sQuery(id+"F0.wireOp",EDGE,"e45c49fc-26fb-4fd0-8f63-7eae6f12a87e.trimOffspring"),sQuery(id+"F0.wireOp",EDGE,"b814ad12-1d71-4b28-b985-c27c8c5e389f.trimOffspring"),sQuery(id+"F0.wireOp",EDGE,"2c71e4f5-3aaf-49a7-9cd9-7906c17fc5b6.trimOffspring"),sQuery(id+"F0.wireOp",EDGE,"2e0ebafb-e982-4014-ab51-e9b40ec535c4.trimOffspring"),sQuery(id+"F0.wireOp",EDGE,"ffa78a0e-e73a-4c7c-a233-faf7876c79e0.trimOffspring"),sQuery(id+"F0.wireOp",EDGE,"5ae34624-9dc0-4140-9c26-527617327f6f.trimOffspring"),sQuery(id+"F0.wireOp",EDGE,"f635a409-f61b-4649-9e31-d42e7781e6f4.trimOffspring"),sQuery(id+"F0.wireOp",EDGE,"07e56e10-4129-4a8e-825d-56220bd91938.trimOffspring"),sQuery(id+"F0.wireOp",EDGE,"6bba4f67-e4ba-4e85-94e1-08bcb743ed3f.trimOffspring"),sQuery(id+"F0.wireOp",EDGE,"5826d8d4-b774-450b-9d76-56fb2635cf42.trimOffspring"),sQuery(id+"F0.wireOp",EDGE,"d3ac0e20-25c0-4450-adcd-7930d79a125d.trimOffspring"),sQuery(id+"F0.wireOp",EDGE,"460eded8-94ea-42c9-bb5c-95c891dcb47a.trimOffspring"),sQuery(id+"F0.wireOp",EDGE,"6bf81d76-93cb-4871-b2e8-8002e1628139.trimOffspring"),sQuery(id+"F0.wireOp",EDGE,"6b65a889-62aa-4a71-aefc-0fdc80f9fbd7.trimOffspring"),sQuery(id+"F0.wireOp",EDGE,"492cef29-5c9f-43bb-9a21-f4b26ab4c56d.trimOffspring"),sQuery(id+"F0.wireOp",EDGE,"ec42e2a7-4c47-4e2f-8ead-93cad2025480.trimOffspring"),sQuery(id+"F0.wireOp",EDGE,"a26ede43-7a92-4ef9-9b65-5d6345ae6e2d.trimOffspring"),sQuery(id+"F0.wireOp",EDGE,"74509194-0070-41ec-8664-167cdb64098b.trimOffspring"),sQuery(id+"F0.wireOp",EDGE,"356a243f-46d5-4ba5-b8e6-9c60b8afb371.trimOffspring"),sQuery(id+"F0.wireOp",EDGE,"44432cc4-0e61-452d-8d9f-c2c31a2a2b76.trimOffspring"),sQuery(id+"F0.wireOp",EDGE,"083761ce-7f6a-4772-a0b6-42da9d9a583c.trimOffspring"),sQuery(id+"F0.wireOp",EDGE,"76966a8d-6096-4b7e-843c-87f34c569aca.trimOffspring"),sQuery(id+"F0.wireOp",EDGE,"fdc08ff0-62e3-4f0b-8448-a5e6ce257c64.trimOffspring"),sQuery(id+"F0.wireOp",EDGE,"0763c2a9-43d9-4018-9a8d-0e270b08ccc4"),sQuery(id+"F0.wireOp",EDGE,"adbb0289-b1bd-468f-a573-d0a6248d6679"),sQuery(id+"F0.wireOp",EDGE,"e802149e-0d3e-4a98-83d7-5df97ce44949.trimOffspring"),sQuery(id+"F0.wireOp",EDGE,"E1"),sQuery(id+"F0.wireOp",EDGE,"E2"),sQuery(id+"F0.wireOp",EDGE,"E3"),sQuery(id+"F0.wireOp",EDGE,"E4"),sQuery(id+"F0.wireOp",EDGE,"EA74iWvD-8oKk-ivYR-DS7W-3RoOPZgJlXoF"),sQuery(id+"F0.wireOp",EDGE,"OAE0uyU3-7MVm-HVLp-ilHf-uihLfXUpzug4")])],"isStart":true});
            var sketch = newSketch(context, id + "F4", { "sketchPlane" : qUnion([Q0])});
            skCircle(sketch, "E1274.0", {"center": v(0, 0) * mm, "radius": 57.15 * mm});
            skCircle(sketch, "E1275.0", {"center": v(0, 50.8) * mm, "radius": 1.59 * mm});
            skCircle(sketch, "E1276.0", {"center": v(-50.8, 0) * mm, "radius": 1.59 * mm});
            skCircle(sketch, "E1277.0", {"center": v(0, -50.8) * mm, "radius": 1.59 * mm});
            skCircle(sketch, "E1278.0", {"center": v(50.8, 0) * mm, "radius": 1.59 * mm});
            skCircle(sketch, "E1279", {"center": v(0, 0) * mm, "radius": 31.95 * mm});
            skSolve(sketch);
        }
        {
            var Q0;
            Q0 = qSketchRegion(id + "F4", true);
            extrude(context, id + "F5", {"entities" : qUnion([Q0]), "operationType" : NewBodyOperationType.ADD, "depth" : 1.52 * mm});
        }
    });
